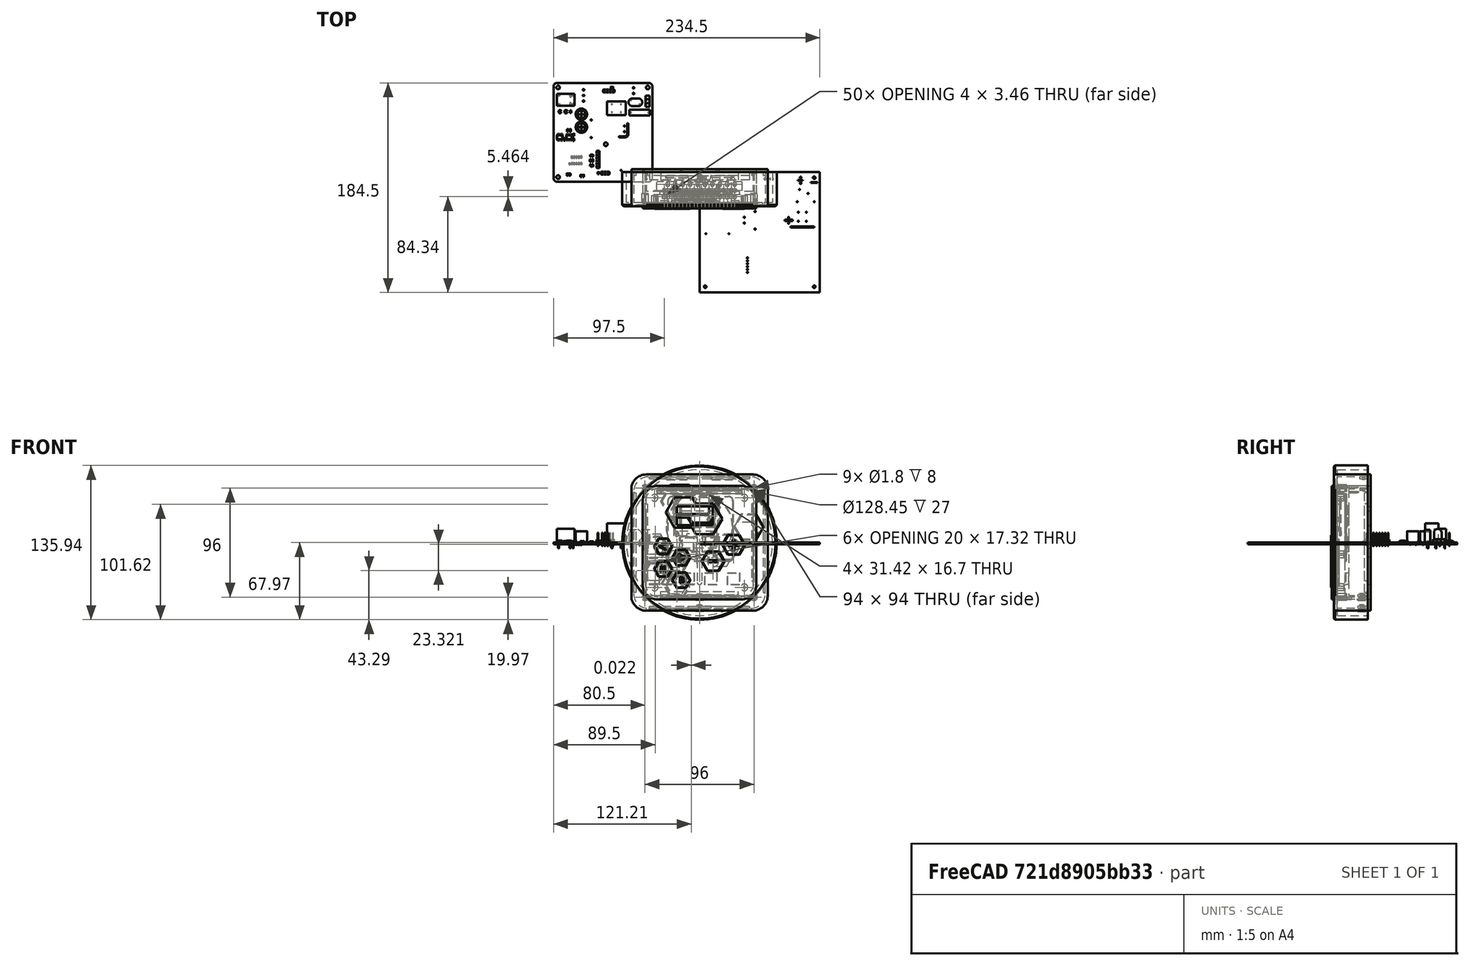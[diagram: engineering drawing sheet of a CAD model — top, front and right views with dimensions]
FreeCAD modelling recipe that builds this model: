
FCSTD DOCUMENT  (FreeCAD 0.18R4 (GitTag))
Label: esp-thermostat
License: All rights reserved
LicenseURL: http://en.wikipedia.org/wiki/All_rights_reserved
objects: Sketcher::SketchObject×72, Part::Feature×48, PartDesign::Pad×45, PartDesign::Pocket×31, PartDesign::Body×14, App::Part×13, PartDesign::Chamfer×12, Mesh::Feature×8, PartDesign::Fillet×6, Part::Part2DObjectPython×6, PartDesign::CoordinateSystem×2, PartDesign::LinearPattern×2, PartDesign::Plane×1
note: 315 computed .brp shape members not serialized (recipe doc carries the construction recipe); baked Part::Feature solids carry a one-line shape summary decoded from their .brp

FEATURE [Sketcher::SketchObject] Sketch  label="Face Sketch"
  MapMode = 5
  Placement = pos=(0,0,0) rot=(1,0,0;1.5708rad)
  Support = -> [XZ_Plane]
  expr: Constraints[21] = 31.42 / 2
  sketch-geometry (48):
    g0: LineSegment StartX=-50 StartY=50 StartZ=0 EndX=50 EndY=50 EndZ=0
    g1: LineSegment StartX=50 StartY=50 StartZ=0 EndX=50 EndY=-50 EndZ=0
    g2: LineSegment StartX=50 StartY=-50 StartZ=0 EndX=-50 EndY=-50 EndZ=0
    g3: LineSegment StartX=-50 StartY=-50 StartZ=0 EndX=-50 EndY=50 EndZ=0
    g4: LineSegment StartX=-15.71 StartY=15 StartZ=0 EndX=15.71 EndY=15 EndZ=0
    g5: LineSegment StartX=15.71 StartY=15 StartZ=0 EndX=15.71 EndY=31.7 EndZ=0
    g6: LineSegment StartX=15.71 StartY=31.7 StartZ=0 EndX=-15.71 EndY=31.7 EndZ=0
    g7: LineSegment StartX=-15.71 StartY=31.7 StartZ=0 EndX=-15.71 EndY=15 EndZ=0
    g8: LineSegment StartX=-16.71 StartY=5 StartZ=0 EndX=-2.71 EndY=5 EndZ=0
    g9: LineSegment StartX=-2.71 StartY=5 StartZ=0 EndX=-2.71 EndY=-8 EndZ=0
    g10: LineSegment StartX=2.71 StartY=5 StartZ=0 EndX=16.71 EndY=5 EndZ=0
    g11: LineSegment StartX=16.71 StartY=5 StartZ=0 EndX=16.71 EndY=2.5 EndZ=0
    g12: LineSegment StartX=4.71 StartY=-8 StartZ=0 EndX=2.71 EndY=-8 EndZ=0
    g13: LineSegment StartX=2.71 StartY=-8 StartZ=0 EndX=2.71 EndY=5 EndZ=0
    g14: LineSegment StartX=-35 StartY=-27 StartZ=0 EndX=-25 EndY=-27 EndZ=0
    g15: LineSegment StartX=-25 StartY=-27 StartZ=0 EndX=-25 EndY=-37 EndZ=0
    g16: LineSegment StartX=-25 StartY=-37 StartZ=0 EndX=-35 EndY=-37 EndZ=0
    g17: LineSegment StartX=-35 StartY=-37 StartZ=0 EndX=-35 EndY=-27 EndZ=0
    g18: LineSegment StartX=-15 StartY=-27 StartZ=0 EndX=-5 EndY=-27 EndZ=0
    g19: LineSegment StartX=-5 StartY=-27 StartZ=0 EndX=-5 EndY=-37 EndZ=0
    g20: LineSegment StartX=-5 StartY=-37 StartZ=0 EndX=-15 EndY=-37 EndZ=0
    g21: LineSegment StartX=-15 StartY=-37 StartZ=0 EndX=-15 EndY=-27 EndZ=0
    g22: LineSegment StartX=5 StartY=-27 StartZ=0 EndX=15 EndY=-27 EndZ=0
    g23: LineSegment StartX=15 StartY=-27 StartZ=0 EndX=15 EndY=-37 EndZ=0
    g24: LineSegment StartX=15 StartY=-37 StartZ=0 EndX=5 EndY=-37 EndZ=0
    g25: LineSegment StartX=5 StartY=-37 StartZ=0 EndX=5 EndY=-27 EndZ=0
    g26: LineSegment StartX=25 StartY=-27 StartZ=0 EndX=35 EndY=-27 EndZ=0
    g27: LineSegment StartX=35 StartY=-27 StartZ=0 EndX=35 EndY=-37 EndZ=0
    g28: LineSegment StartX=35 StartY=-37 StartZ=0 EndX=25 EndY=-37 EndZ=0
    g29: LineSegment StartX=25 StartY=-37 StartZ=0 EndX=25 EndY=-27 EndZ=0
    g30: LineSegment [constr] StartX=-18 StartY=39.7 StartZ=0 EndX=18 EndY=39.7 EndZ=0
    g31: LineSegment [constr] StartX=18 StartY=39.7 StartZ=0 EndX=18 EndY=6 EndZ=0
    g32: LineSegment [constr] StartX=18 StartY=6 StartZ=0 EndX=-18 EndY=6 EndZ=0
    g33: LineSegment [constr] StartX=-18 StartY=6 StartZ=0 EndX=-18 EndY=39.7 EndZ=0
    g34: LineSegment StartX=-16.71 StartY=5 StartZ=0 EndX=-16.71 EndY=2.5 EndZ=0
    g35: LineSegment StartX=-2.71 StartY=-8 StartZ=0 EndX=-4.71 EndY=-8 EndZ=0
    g36: Circle [constr] CenterX=-16.71 CenterY=2.5 CenterZ=0 NormalX=0 NormalY=0 NormalZ=1 AngleXU=0 Radius=1
    g37: Circle [constr] CenterX=-14.99 CenterY=-4.5 CenterZ=0 NormalX=0 NormalY=0 NormalZ=1 AngleXU=0 Radius=1
    g38: Circle [constr] CenterX=-4.71 CenterY=-8 CenterZ=0 NormalX=0 NormalY=0 NormalZ=1 AngleXU=0 Radius=1
    g39: BSplineCurve PolesCount=3 KnotsCount=2 Degree=2 IsPeriodic=0
    g40: GeomPoint [constr] X=-16.71 Y=2.5 Z=0
    g41: GeomPoint [constr] X=-4.71 Y=-8 Z=0
    g42: Circle [constr] CenterX=4.71 CenterY=-8 CenterZ=0 NormalX=0 NormalY=0 NormalZ=1 AngleXU=0 Radius=2
    g43: Circle [constr] CenterX=14.99 CenterY=-4.5 CenterZ=0 NormalX=0 NormalY=0 NormalZ=1 AngleXU=0 Radius=2
    g44: Circle [constr] CenterX=16.71 CenterY=2.5 CenterZ=0 NormalX=0 NormalY=0 NormalZ=1 AngleXU=0 Radius=2
    g45: BSplineCurve PolesCount=3 KnotsCount=2 Degree=2 IsPeriodic=0
    g46: GeomPoint [constr] X=4.71 Y=-8 Z=0
    g47: GeomPoint [constr] X=16.71 Y=2.5 Z=0
  constraints (133):
    c: Coincident(g0,g1)
    c: Coincident(g1,g2)
    c: Coincident(g2,g3)
    c: Coincident(g3,g0)
    c: Horizontal(g0)
    c: Horizontal(g2)
    c: Vertical(g1)
    c: Vertical(g3)
    c: Equal(g0,g1)
    c: Symmetric(g0,g1,g-1)
    c: DistanceX(g0,g0) = 100
    c: Coincident(g4,g5)
    c: Coincident(g5,g6)
    c: Coincident(g6,g7)
    c: Coincident(g7,g4)
    c: Horizontal(g4)
    c: Horizontal(g6)
    c: Vertical(g5)
    c: Vertical(g7)
    c: DistanceX(g6,g6) = 31.42
    c: DistanceY(g7,g7) = 16.7
    c: DistanceX(g6,g-1) = 15.71
    c: Coincident(g8,g9)
    c: Horizontal(g8)
    c: Vertical(g9)
    c: Coincident(g10,g11)
    c: Coincident(g12,g13)
    c: Coincident(g13,g10)
    c: Horizontal(g10)
    c: Horizontal(g12)
    c: Vertical(g11)
    c: DistanceX(g8,g8) = 14
    c: Coincident(g14,g15)
    c: Coincident(g15,g16)
    c: Coincident(g16,g17)
    c: Coincident(g17,g14)
    c: Horizontal(g14)
    c: Horizontal(g16)
    c: Vertical(g15)
    c: Vertical(g17)
    c: Coincident(g18,g19)
    c: Coincident(g19,g20)
    c: Coincident(g20,g21)
    c: Coincident(g21,g18)
    c: Horizontal(g18)
    c: Horizontal(g20)
    c: Vertical(g19)
    c: Vertical(g21)
    c: Coincident(g22,g23)
    c: Coincident(g23,g24)
    c: Coincident(g24,g25)
    c: Coincident(g25,g22)
    c: Horizontal(g22)
    c: Horizontal(g24)
    c: Vertical(g23)
    c: Vertical(g25)
    c: Coincident(g26,g27)
    c: Coincident(g27,g28)
    c: Coincident(g28,g29)
    c: Coincident(g29,g26)
    c: Horizontal(g26)
    c: Horizontal(g28)
    c: Vertical(g27)
    c: Vertical(g29)
    c: Equal(g14,g15)
    c: Equal(g15,g18)
    c: Equal(g18,g19)
    c: Equal(g19,g22)
    c: Equal(g22,g23)
    c: Equal(g23,g26)
    c: Equal(g26,g27)
    c: DistanceY(g-1,g9) = -8
    c: DistanceY(g-1,g12) = -8
    c: DistanceY(g14,g18) = 0
    c: DistanceY(g22,g18) = 0
    c: DistanceY(g22,g26) = 0
    c: DistanceX(g14,g18) = 10
    c: DistanceX(g18,g22) = 10
    c: DistanceX(g22,g26) = 10
    c: DistanceX(g18,g-1) = 5
    c: DistanceY(g22,g-1) = 27
    c: DistanceY(g-1,g4) = 15
    c: Coincident(g30,g31)
    c: Coincident(g31,g32)
    c: Coincident(g32,g33)
    c: Coincident(g33,g30)
    c: Horizontal(g30)
    c: Horizontal(g32)
    c: Vertical(g31)
    c: Vertical(g33)
    c: DistanceX(g30,g30) = 36
    c: DistanceX(g30,g6) = 2.29
    c: DistanceY(g6,g30) = 8
    c: DistanceX(g14,g14) = 10
    c: DistanceY(g9,g8) = 13
    c: Equal(g8,g10)
    c: Equal(g9,g13)
    c: Coincident(g34,g8)
    c: Vertical(g34)
    c: Coincident(g35,g9)
    c: Horizontal(g35)
    c: Equal(g34,g11)
    c: Equal(g35,g12)
    c: DistanceX(g8,g4) = 1
    c: DistanceX(g4,g10) = 1
    c: DistanceY(g31,g31) = 33.7
    c: Coincident(g39,g34)
    c: Radius(g36) = 1
    c: Equal(g36,g37)
    c: Equal(g36,g38)
    c: Coincident(g39,g35)
    c: InternalAlignment(g36,g39)
    c: InternalAlignment(g37,g39)
    c: InternalAlignment(g38,g39)
    c: InternalAlignment(g40,g39)
    c: InternalAlignment(g41,g39)
    c: DistanceX(g34,g37) = 1.72
    c: DistanceY(g35,g37) = 3.5
    c: DistanceY(g34,g34) = 2.5
    c: DistanceX(g35,g35) = 2
    c: Parallel(g13,g9)
    c: Coincident(g45,g12)
    c: Radius(g42) = 2
    c: Equal(g42,g43)
    c: Equal(g42,g44)
    c: Coincident(g45,g11)
    c: InternalAlignment(g42,g45)
    c: InternalAlignment(g43,g45)
    c: InternalAlignment(g44,g45)
    c: InternalAlignment(g46,g45)
    c: InternalAlignment(g47,g45)
    c: DistanceX(g43,g11) = 1.72
    c: DistanceY(g12,g43) = 3.5
FEATURE [PartDesign::Pad] Pad  label="Body Pad"
  Length = 20
  Length2 = 100
  Placement = pos=(0,0,0) rot=(1,0,0;1.5708rad)
  Profile = -> Sketch
  Type = 0
FEATURE [Sketcher::SketchObject] Sketch002  label="Inside Sketch"
  MapMode = 5
  Placement = pos=(0,0,0) rot=(-1,0,0;1.5708rad)
  sketch-geometry (4):
    g0: LineSegment StartX=-47 StartY=47 StartZ=0 EndX=47 EndY=47 EndZ=0
    g1: LineSegment StartX=47 StartY=47 StartZ=0 EndX=47 EndY=-47 EndZ=0
    g2: LineSegment StartX=47 StartY=-47 StartZ=0 EndX=-47 EndY=-47 EndZ=0
    g3: LineSegment StartX=-47 StartY=-47 StartZ=0 EndX=-47 EndY=47 EndZ=0
  constraints (9):
    c: Coincident(g0,g1)
    c: Coincident(g1,g2)
    c: Coincident(g2,g3)
    c: Coincident(g3,g0)
    c: Horizontal(g0)
    c: Horizontal(g2)
    c: Vertical(g1)
    c: Vertical(g3)
    c: Symmetric(g0,g1,g-1)
FEATURE [PartDesign::Pocket] Pocket001  label="Inside Pocket"
  BaseFeature = -> Pad
  Length = 5
  Length2 = 100
  Offset = -3
  Placement = pos=(0,0,0) rot=(1,0,0;1.5708rad)
  Profile = -> Sketch002
  Type = 2
FEATURE [Sketcher::SketchObject] Sketch008  label="Face Circle Sketch"
  MapMode = 5
  Placement = pos=(0,-20,0) rot=(1,0,0;1.5708rad)
  Support = -> [Pocket001]
  sketch-geometry (1):
    g0: Circle CenterX=0 CenterY=14 CenterZ=0 NormalX=0 NormalY=0 NormalZ=1 AngleXU=0 Radius=29
  constraints (3):
    c: PointOnObject(g0,g-2)
    c: Radius(g0) = 29
    c: DistanceY(g-1,g0) = 14
FEATURE [PartDesign::Pocket] Pocket  label="Face Circle Pocket"
  BaseFeature = -> Pocket001
  Length = 1
  Length2 = 100
  Placement = pos=(0,0,0) rot=(1,0,0;1.5708rad)
  Profile = -> Sketch008
  Type = 0
FEATURE [PartDesign::Fillet] Fillet  label="Edge Fillet"
  Base = -> Pocket [Face6,Face3,Face1,Face2]
  BaseFeature = -> Pocket
  Placement = pos=(0,0,0) rot=(1,0,0;1.5708rad)
  Radius = 2.6
FEATURE [PartDesign::Chamfer] Chamfer  label="Minus Button Chamfer"
  Base = -> Fillet [Edge136,Edge135,Edge134,Edge138,Edge137]
  BaseFeature = -> Fillet
  Placement = pos=(0,0,0) rot=(1,0,0;1.5708rad)
  Size = 0.5
FEATURE [PartDesign::Chamfer] Chamfer001  label="Plus Button Chamfer"
  Base = -> Chamfer [Edge8,Edge7,Edge11,Edge10,Edge9]
  BaseFeature = -> Chamfer
  Placement = pos=(0,0,0) rot=(1,0,0;1.5708rad)
  Size = 0.5
FEATURE [PartDesign::Chamfer] Chamfer002  label="Display Chamfer"
  Base = -> Chamfer001 [Edge12,Edge15,Edge14,Edge13]
  BaseFeature = -> Chamfer001
  Placement = pos=(0,0,0) rot=(1,0,0;1.5708rad)
  Size = 1.5
FEATURE [PartDesign::Chamfer] Chamfer003  label="Circle Chamfer"
  Base = -> Chamfer002 [Edge45]
  BaseFeature = -> Chamfer002
  Placement = pos=(0,0,0) rot=(1,0,0;1.5708rad)
  Size = 0.4
FEATURE [PartDesign::Chamfer] Chamfer004  label="Auxiliary Buttons Chamfer"
  Base = -> Chamfer003 [Edge37,Edge36,Edge38,Edge39,Edge28,Edge29,Edge31,Edge30,Edge26,Edge24,Edge25,Edge27,Edge34,Edge32,Edge33,Edge35]
  BaseFeature = -> Chamfer003
  Placement = pos=(0,0,0) rot=(1,0,0;1.5708rad)
  Size = 0.5
FEATURE [PartDesign::Body] Body  label="Housing"
  Group = -> [Sketch,Pad,Sketch002,Pocket001,Pocket,Sketch008,Fillet,Chamfer,Chamfer001,Chamfer002,Chamfer003,Chamfer004]
  Origin = -> Origin
  Tip = -> Chamfer004
FEATURE [Sketcher::SketchObject] Sketch010  label="Face Sketch001"
  MapMode = 5
  Placement = pos=(0,0,0) rot=(1,0,0;1.5708rad)
  Support = -> [XZ_Plane001]
  expr: Constraints[21] = 31.42 / 2
  sketch-geometry (40):
    g0: LineSegment StartX=-50 StartY=50 StartZ=0 EndX=50 EndY=50 EndZ=0
    g1: LineSegment StartX=50 StartY=50 StartZ=0 EndX=50 EndY=-50 EndZ=0
    g2: LineSegment StartX=50 StartY=-50 StartZ=0 EndX=-50 EndY=-50 EndZ=0
    g3: LineSegment StartX=-50 StartY=-50 StartZ=0 EndX=-50 EndY=50 EndZ=0
    g4: LineSegment StartX=-15.71 StartY=15 StartZ=0 EndX=15.71 EndY=15 EndZ=0
    g5: LineSegment StartX=15.71 StartY=15 StartZ=0 EndX=15.71 EndY=31.7 EndZ=0
    g6: LineSegment StartX=15.71 StartY=31.7 StartZ=0 EndX=-15.71 EndY=31.7 EndZ=0
    g7: LineSegment StartX=-15.71 StartY=31.7 StartZ=0 EndX=-15.71 EndY=15 EndZ=0
    g8: LineSegment StartX=-17.21 StartY=4 StartZ=0 EndX=-5.21 EndY=4 EndZ=0
    g9: LineSegment StartX=-5.21 StartY=4 StartZ=0 EndX=-5.21 EndY=-8 EndZ=0
    g10: LineSegment StartX=5.21 StartY=4 StartZ=0 EndX=17.21 EndY=4 EndZ=0
    g11: LineSegment StartX=17.21 StartY=4 StartZ=0 EndX=17.21 EndY=1.5 EndZ=0
    g12: LineSegment StartX=7.21 StartY=-8 StartZ=0 EndX=5.21 EndY=-8 EndZ=0
    g13: LineSegment StartX=5.21 StartY=-8 StartZ=0 EndX=5.21 EndY=4 EndZ=0
    g14: LineSegment StartX=-35 StartY=-27 StartZ=0 EndX=-25 EndY=-27 EndZ=0
    g15: LineSegment StartX=-25 StartY=-27 StartZ=0 EndX=-25 EndY=-37 EndZ=0
    g16: LineSegment StartX=-25 StartY=-37 StartZ=0 EndX=-35 EndY=-37 EndZ=0
    g17: LineSegment StartX=-35 StartY=-37 StartZ=0 EndX=-35 EndY=-27 EndZ=0
    g18: LineSegment StartX=-15 StartY=-27 StartZ=0 EndX=-5 EndY=-27 EndZ=0
    g19: LineSegment StartX=-5 StartY=-27 StartZ=0 EndX=-5 EndY=-37 EndZ=0
    g20: LineSegment StartX=-5 StartY=-37 StartZ=0 EndX=-15 EndY=-37 EndZ=0
    g21: LineSegment StartX=-15 StartY=-37 StartZ=0 EndX=-15 EndY=-27 EndZ=0
    g22: LineSegment StartX=5 StartY=-27 StartZ=0 EndX=15 EndY=-27 EndZ=0
    g23: LineSegment StartX=15 StartY=-27 StartZ=0 EndX=15 EndY=-37 EndZ=0
    g24: LineSegment StartX=15 StartY=-37 StartZ=0 EndX=5 EndY=-37 EndZ=0
    g25: LineSegment StartX=5 StartY=-37 StartZ=0 EndX=5 EndY=-27 EndZ=0
    g26: LineSegment StartX=25 StartY=-27 StartZ=0 EndX=35 EndY=-27 EndZ=0
    g27: LineSegment StartX=35 StartY=-27 StartZ=0 EndX=35 EndY=-37 EndZ=0
    g28: LineSegment StartX=35 StartY=-37 StartZ=0 EndX=25 EndY=-37 EndZ=0
    g29: LineSegment StartX=25 StartY=-37 StartZ=0 EndX=25 EndY=-27 EndZ=0
    g30: LineSegment [constr] StartX=-18 StartY=39.7 StartZ=0 EndX=18 EndY=39.7 EndZ=0
    g31: LineSegment [constr] StartX=18 StartY=39.7 StartZ=0 EndX=18 EndY=6 EndZ=0
    g32: LineSegment [constr] StartX=18 StartY=6 StartZ=0 EndX=-18 EndY=6 EndZ=0
    g33: LineSegment [constr] StartX=-18 StartY=6 StartZ=0 EndX=-18 EndY=39.7 EndZ=0
    g34: LineSegment StartX=-17.21 StartY=4 StartZ=0 EndX=-17.21 EndY=1.5 EndZ=0
    g35: LineSegment StartX=-5.21 StartY=-8 StartZ=0 EndX=-7.21 EndY=-8 EndZ=0
    g36: LineSegment StartX=-7.21 StartY=-8 StartZ=0 EndX=-17.21 EndY=-8 EndZ=0
    g37: LineSegment StartX=-17.21 StartY=1.5 StartZ=0 EndX=-17.21 EndY=-8 EndZ=0
    g38: LineSegment StartX=7.21 StartY=-8 StartZ=0 EndX=17.21 EndY=-8 EndZ=0
    g39: LineSegment StartX=17.21 StartY=1.5 StartZ=0 EndX=17.21 EndY=-8 EndZ=0
  constraints (119):
    c: Coincident(g0,g1)
    c: Coincident(g1,g2)
    c: Coincident(g2,g3)
    c: Coincident(g3,g0)
    c: Horizontal(g0)
    c: Horizontal(g2)
    c: Vertical(g1)
    c: Vertical(g3)
    c: Equal(g0,g1)
    c: Symmetric(g0,g1,g-1)
    c: DistanceX(g0,g0) = 100
    c: Coincident(g4,g5)
    c: Coincident(g5,g6)
    c: Coincident(g6,g7)
    c: Coincident(g7,g4)
    c: Horizontal(g4)
    c: Horizontal(g6)
    c: Vertical(g5)
    c: Vertical(g7)
    c: DistanceX(g6,g6) = 31.42
    c: DistanceY(g7,g7) = 16.7
    c: DistanceX(g6,g-1) = 15.71
    c: Coincident(g8,g9)
    c: Horizontal(g8)
    c: Vertical(g9)
    c: Coincident(g10,g11)
    c: Coincident(g12,g13)
    c: Coincident(g13,g10)
    c: Horizontal(g10)
    c: Horizontal(g12)
    c: Vertical(g11)
    c: DistanceX(g8,g8) = 12
    c: Coincident(g14,g15)
    c: Coincident(g15,g16)
    c: Coincident(g16,g17)
    c: Coincident(g17,g14)
    c: Horizontal(g14)
    c: Horizontal(g16)
    c: Vertical(g15)
    c: Vertical(g17)
    c: Coincident(g18,g19)
    c: Coincident(g19,g20)
    c: Coincident(g20,g21)
    c: Coincident(g21,g18)
    c: Horizontal(g18)
    c: Horizontal(g20)
    c: Vertical(g19)
    c: Vertical(g21)
    c: Coincident(g22,g23)
    c: Coincident(g23,g24)
    c: Coincident(g24,g25)
    c: Coincident(g25,g22)
    c: Horizontal(g22)
    c: Horizontal(g24)
    c: Vertical(g23)
    c: Vertical(g25)
    c: Coincident(g26,g27)
    c: Coincident(g27,g28)
    c: Coincident(g28,g29)
    c: Coincident(g29,g26)
    c: Horizontal(g26)
    c: Horizontal(g28)
    c: Vertical(g27)
    c: Vertical(g29)
    c: Equal(g14,g15)
    c: Equal(g15,g18)
    c: Equal(g18,g19)
    c: Equal(g19,g22)
    c: Equal(g22,g23)
    c: Equal(g23,g26)
    c: Equal(g26,g27)
    c: DistanceY(g-1,g9) = -8
    c: DistanceY(g-1,g12) = -8
    c: DistanceY(g14,g18) = 0
    c: DistanceY(g22,g18) = 0
    c: DistanceY(g22,g26) = 0
    c: DistanceX(g14,g18) = 10
    c: DistanceX(g18,g22) = 10
    c: DistanceX(g22,g26) = 10
    c: DistanceX(g18,g-1) = 5
    c: DistanceY(g22,g-1) = 27
    c: DistanceY(g-1,g4) = 15
    c: Coincident(g30,g31)
    c: Coincident(g31,g32)
    c: Coincident(g32,g33)
    c: Coincident(g33,g30)
    c: Horizontal(g30)
    c: Horizontal(g32)
    c: Vertical(g31)
    c: Vertical(g33)
    c: DistanceX(g30,g30) = 36
    c: DistanceX(g30,g6) = 2.29
    c: DistanceY(g6,g30) = 8
    c: DistanceX(g14,g14) = 10
    c: DistanceY(g9,g8) = 12
    c: Equal(g8,g10)
    c: Equal(g9,g13)
    c: Coincident(g34,g8)
    c: Vertical(g34)
    c: Coincident(g35,g9)
    c: Horizontal(g35)
    c: Equal(g34,g11)
    c: Equal(g35,g12)
    c: DistanceX(g8,g4) = 1.5
    c: DistanceX(g4,g10) = 1.5
    c: DistanceY(g31,g31) = 33.7
    c: DistanceY(g34,g34) = 2.5
    c: DistanceX(g35,g35) = 2
    c: Parallel(g13,g9)
    c: Coincident(g36,g35)
    c: Horizontal(g36)
    c: Coincident(g37,g34)
    c: Vertical(g37)
    c: Coincident(g36,g37)
    c: Coincident(g38,g12)
    c: Horizontal(g38)
    c: Coincident(g39,g11)
    c: Vertical(g39)
    c: Coincident(g38,g39)
FEATURE [Sketcher::SketchObject] Sketch011  label="Inside Sketch001"
  MapMode = 5
  Placement = pos=(0,0,0) rot=(-1,0,0;1.5708rad)
  sketch-geometry (4):
    g0: LineSegment StartX=-47 StartY=47 StartZ=0 EndX=47 EndY=47 EndZ=0
    g1: LineSegment StartX=47 StartY=47 StartZ=0 EndX=47 EndY=-47 EndZ=0
    g2: LineSegment StartX=47 StartY=-47 StartZ=0 EndX=-47 EndY=-47 EndZ=0
    g3: LineSegment StartX=-47 StartY=-47 StartZ=0 EndX=-47 EndY=47 EndZ=0
  constraints (9):
    c: Coincident(g0,g1)
    c: Coincident(g1,g2)
    c: Coincident(g2,g3)
    c: Coincident(g3,g0)
    c: Horizontal(g0)
    c: Horizontal(g2)
    c: Vertical(g1)
    c: Vertical(g3)
    c: Symmetric(g0,g1,g-1)
FEATURE [PartDesign::Pad] Pad001  label="Body Pad001"
  Length = 20
  Length2 = 100
  Placement = pos=(0,0,0) rot=(1,0,0;1.5708rad)
  Profile = -> Sketch010
  Type = 0
FEATURE [PartDesign::Pocket] Pocket003  label="Inside Pocket001"
  BaseFeature = -> Pad001
  Length = 5
  Length2 = 100
  Offset = -3
  Placement = pos=(0,0,0) rot=(1,0,0;1.5708rad)
  Profile = -> Sketch011
  Type = 2
FEATURE [Sketcher::SketchObject] Sketch009  label="Face Circle Sketch001"
  MapMode = 5
  Placement = pos=(0,-20,0) rot=(1,0,0;1.5708rad)
  Support = -> [Pocket003]
  expr: Constraints[16] = 55 / 2
  sketch-geometry (8):
    g0: LineSegment StartX=-23.9253 StartY=40.3727 StartZ=0 EndX=25.6028 EndY=40.3727 EndZ=0
    g1: LineSegment StartX=29.1774 StartY=36.798 StartZ=0 EndX=29.1774 EndY=-12.7301 EndZ=0
    g2: LineSegment StartX=25.6028 StartY=-16.3047 StartZ=0 EndX=-23.9253 EndY=-16.3047 EndZ=0
    g3: LineSegment StartX=-27.5 StartY=-12.7301 StartZ=0 EndX=-27.5 EndY=36.798 EndZ=0
    g4: ArcOfCircle CenterX=-23.9253 CenterY=36.798 CenterZ=0 NormalX=0 NormalY=0 NormalZ=1 AngleXU=0 Radius=3.57466 StartAngle=1.5708 EndAngle=3.14159
    g5: ArcOfCircle CenterX=25.6028 CenterY=36.798 CenterZ=0 NormalX=0 NormalY=0 NormalZ=1 AngleXU=0 Radius=3.57466 StartAngle=8e-16 EndAngle=1.5708
    g6: ArcOfCircle CenterX=25.6028 CenterY=-12.7301 CenterZ=0 NormalX=0 NormalY=0 NormalZ=1 AngleXU=0 Radius=3.57466 StartAngle=4.71239 EndAngle=6.28319
    g7: ArcOfCircle CenterX=-23.9253 CenterY=-12.7301 CenterZ=0 NormalX=0 NormalY=0 NormalZ=1 AngleXU=0 Radius=3.57466 StartAngle=3.14159 EndAngle=4.71239
  constraints (17):
    c: Horizontal(g0)
    c: Horizontal(g2)
    c: Vertical(g1)
    c: Vertical(g3)
    c: Equal(g0,g1)
    c: Tangent(g3,g4) = 1.5708
    c: Tangent(g0,g4) = 1.5708
    c: Tangent(g0,g5) = 1.5708
    c: Tangent(g1,g5) = 1.5708
    c: Tangent(g2,g6) = 1.5708
    c: Tangent(g1,g6) = 1.5708
    c: Tangent(g2,g7) = 1.5708
    c: Tangent(g3,g7) = 1.5708
    c: Equal(g7,g4)
    c: Equal(g4,g5)
    c: Equal(g5,g6)
    c: DistanceX(g3,g-1) = 27.5
FEATURE [PartDesign::Pocket] Pocket002  label="Face Circle Pocket001"
  BaseFeature = -> Pocket003
  Length = 1
  Length2 = 100
  Placement = pos=(0,0,0) rot=(1,0,0;1.5708rad)
  Profile = -> Sketch009
  Type = 0
FEATURE [PartDesign::Fillet] Fillet001  label="Edge Fillet001"
  Base = -> Pocket002 [Face6,Face3,Face1,Face2]
  BaseFeature = -> Pocket002
  Placement = pos=(0,0,0) rot=(1,0,0;1.5708rad)
  Radius = 2.6
FEATURE [PartDesign::Chamfer] Chamfer009  label="Display Chamfer001"
  Base = -> Fillet001 [Edge170,Edge171,Edge172,Edge169]
  BaseFeature = -> Fillet001
  Placement = pos=(0,0,0) rot=(1,0,0;1.5708rad)
  Size = 1.5
FEATURE [PartDesign::Chamfer] Chamfer007  label="Circle Chamfer001"
  Base = -> Chamfer009 [Edge35]
  BaseFeature = -> Chamfer009
  Placement = pos=(0,0,0) rot=(1,0,0;1.5708rad)
  Size = 0.4
FEATURE [PartDesign::Chamfer] Chamfer006  label="Auxiliary Buttons Chamfer001"
  Base = -> Chamfer007 [Edge63,Edge61,Edge62,Edge64,Edge53,Edge55,Edge56,Edge54,Edge51,Edge49,Edge50,Edge59,Edge57,Edge58,Edge60,Edge21,Edge23,Edge24,Edge26,Edge30,Edge29,Edge27,Edge32]
  BaseFeature = -> Chamfer007
  Placement = pos=(0,0,0) rot=(1,0,0;1.5708rad)
  Size = 0.5
FEATURE [PartDesign::Body] Body001  label="Housing - Rectangular Face"
  Group = -> [Sketch010,Pad001,Sketch011,Pocket003,Pocket002,Sketch009,Fillet001,Chamfer009,Chamfer007,Chamfer006]
  Origin = -> Origin001
  Tip = -> Chamfer006
FEATURE [Sketcher::SketchObject] Sketch012
  MapMode = 5
  Placement = pos=(0,0,0) rot=(1,0,0;1.5708rad)
  Support = -> [XZ_Plane002]
  sketch-geometry (47):
    g0: LineSegment StartX=-33.6497 StartY=-12.7937 StartZ=0 EndX=-28.6497 EndY=-4.1334 EndZ=0
    g1: LineSegment StartX=-28.6497 StartY=-4.1334 StartZ=0 EndX=-33.6497 EndY=4.52685 EndZ=0
    g2: LineSegment StartX=-33.6497 StartY=4.52685 StartZ=0 EndX=-43.6497 EndY=4.52685 EndZ=0
    g3: LineSegment StartX=-43.6497 StartY=4.52685 StartZ=0 EndX=-48.6497 EndY=-4.1334 EndZ=0
    g4: LineSegment StartX=-48.6497 StartY=-4.1334 StartZ=0 EndX=-43.6497 EndY=-12.7937 EndZ=0
    g5: LineSegment StartX=-43.6497 StartY=-12.7937 StartZ=0 EndX=-33.6497 EndY=-12.7937 EndZ=0
    g6: Circle [constr] CenterX=-38.6497 CenterY=-4.1334 CenterZ=0 NormalX=0 NormalY=0 NormalZ=1 AngleXU=0 Radius=10
    g7: LineSegment StartX=-14.6497 StartY=-24.4539 StartZ=0 EndX=-9.64969 EndY=-15.7937 EndZ=0
    g8: LineSegment StartX=-9.64969 StartY=-15.7937 StartZ=0 EndX=-14.6497 EndY=-7.1334 EndZ=0
    g9: LineSegment StartX=-14.6497 StartY=-7.1334 StartZ=0 EndX=-24.6497 EndY=-7.1334 EndZ=0
    g10: LineSegment StartX=-24.6497 StartY=-7.1334 StartZ=0 EndX=-29.6497 EndY=-15.7937 EndZ=0
    g11: LineSegment StartX=-29.6497 StartY=-15.7937 StartZ=0 EndX=-24.6497 EndY=-24.4539 EndZ=0
    g12: LineSegment StartX=-24.6497 StartY=-24.4539 StartZ=0 EndX=-14.6497 EndY=-24.4539 EndZ=0
    g13: Circle [constr] CenterX=-19.6497 CenterY=-15.7937 CenterZ=0 NormalX=0 NormalY=0 NormalZ=1 AngleXU=0 Radius=10
    g14: LineSegment StartX=-28.6497 StartY=-27.4539 StartZ=0 EndX=-33.6497 EndY=-18.7937 EndZ=0
    g15: LineSegment StartX=-33.6497 StartY=-18.7937 StartZ=0 EndX=-43.6497 EndY=-18.7937 EndZ=0
    g16: LineSegment StartX=-43.6497 StartY=-18.7937 StartZ=0 EndX=-48.6497 EndY=-27.4539 EndZ=0
    g17: LineSegment StartX=-48.6497 StartY=-27.4539 StartZ=0 EndX=-43.6497 EndY=-36.1142 EndZ=0
    g18: LineSegment StartX=-43.6497 StartY=-36.1142 StartZ=0 EndX=-33.6497 EndY=-36.1142 EndZ=0
    g19: LineSegment StartX=-33.6497 StartY=-36.1142 StartZ=0 EndX=-28.6497 EndY=-27.4539 EndZ=0
    g20: Circle [constr] CenterX=-38.6497 CenterY=-27.4539 CenterZ=0 NormalX=0 NormalY=0 NormalZ=1 AngleXU=0 Radius=10
    g21: LineSegment StartX=-14.6497 StartY=-47.7744 StartZ=0 EndX=-9.64969 EndY=-39.1142 EndZ=0
    g22: LineSegment StartX=-9.64969 StartY=-39.1142 StartZ=0 EndX=-14.6497 EndY=-30.4539 EndZ=0
    g23: LineSegment StartX=-14.6497 StartY=-30.4539 StartZ=0 EndX=-24.6497 EndY=-30.4539 EndZ=0
    g24: LineSegment StartX=-24.6497 StartY=-30.4539 StartZ=0 EndX=-29.6497 EndY=-39.1142 EndZ=0
    g25: LineSegment StartX=-29.6497 StartY=-39.1142 StartZ=0 EndX=-24.6497 EndY=-47.7744 EndZ=0
    g26: LineSegment StartX=-24.6497 StartY=-47.7744 StartZ=0 EndX=-14.6497 EndY=-47.7744 EndZ=0
    g27: Circle [constr] CenterX=-19.6497 CenterY=-39.1142 CenterZ=0 NormalX=0 NormalY=0 NormalZ=1 AngleXU=0 Radius=10
    g28: LineSegment StartX=-22.9778 StartY=41.8382 StartZ=0 EndX=8.44221 EndY=41.8382 EndZ=0
    g29: LineSegment StartX=8.44221 StartY=41.8382 StartZ=0 EndX=8.44221 EndY=25.1382 EndZ=0
    g30: LineSegment StartX=8.44221 StartY=25.1382 StartZ=0 EndX=-22.9778 EndY=25.1382 EndZ=0
    g31: LineSegment StartX=-22.9778 StartY=25.1382 StartZ=0 EndX=-22.9778 EndY=41.8382 EndZ=0
    g32: LineSegment StartX=28.2444 StartY=-14.4017 StartZ=0 EndX=34.2444 EndY=-4.00938 EndZ=0
    g33: LineSegment StartX=34.2444 StartY=-4.00938 StartZ=0 EndX=28.2444 EndY=6.38293 EndZ=0
    g34: LineSegment StartX=28.2444 StartY=6.38293 StartZ=0 EndX=16.2444 EndY=6.38293 EndZ=0
    g35: LineSegment StartX=16.2444 StartY=6.38293 StartZ=0 EndX=10.2444 EndY=-4.00938 EndZ=0
    g36: LineSegment StartX=10.2444 StartY=-4.00938 StartZ=0 EndX=16.2444 EndY=-14.4017 EndZ=0
    g37: LineSegment StartX=16.2444 StartY=-14.4017 StartZ=0 EndX=28.2444 EndY=-14.4017 EndZ=0
    g38: Circle [constr] CenterX=22.2444 CenterY=-4.00938 CenterZ=0 NormalX=0 NormalY=0 NormalZ=1 AngleXU=0 Radius=12
    g39: LineSegment StartX=49.2444 StartY=3.38293 StartZ=0 EndX=55.2444 EndY=13.7752 EndZ=0
    g40: LineSegment StartX=55.2444 StartY=13.7752 StartZ=0 EndX=49.2444 EndY=24.1675 EndZ=0
    g41: LineSegment StartX=49.2444 StartY=24.1675 StartZ=0 EndX=37.2444 EndY=24.1675 EndZ=0
    g42: LineSegment StartX=37.2444 StartY=24.1675 StartZ=0 EndX=31.2444 EndY=13.7752 EndZ=0
    g43: LineSegment StartX=31.2444 StartY=13.7752 StartZ=0 EndX=37.2444 EndY=3.38293 EndZ=0
    g44: LineSegment StartX=37.2444 StartY=3.38293 StartZ=0 EndX=49.2444 EndY=3.38293 EndZ=0
    g45: Circle [constr] CenterX=43.2444 CenterY=13.7752 CenterZ=0 NormalX=0 NormalY=0 NormalZ=1 AngleXU=0 Radius=12
    g46: Circle CenterX=0 CenterY=0 CenterZ=0 NormalX=0 NormalY=0 NormalZ=1 AngleXU=0 Radius=67.967
  constraints (109):
    c: Coincident(g0,g1)
    c: Coincident(g1,g2)
    c: Coincident(g2,g3)
    c: Coincident(g3,g4)
    c: Coincident(g4,g5)
    c: Coincident(g5,g0)
    c: Equal(g0, g1-g5) x5
    c: PointOnObject(g0,g6)
    c: PointOnObject(g1,g6)
    c: PointOnObject(g2,g6)
    c: PointOnObject(g3,g6)
    c: PointOnObject(g4,g6)
    c: PointOnObject(g5,g6)
    c: Parallel(g2,g-1)
    c: Radius(g6) = 10
    c: Coincident(g7,g8)
    c: Coincident(g8,g9)
    c: Coincident(g9,g10)
    c: Coincident(g10,g11)
    c: Coincident(g11,g12)
    c: Coincident(g12,g7)
    c: Equal(g7, g8-g12) x5
    c: PointOnObject(g7,g13)
    c: PointOnObject(g8,g13)
    c: PointOnObject(g9,g13)
    c: PointOnObject(g10,g13)
    c: PointOnObject(g11,g13)
    c: PointOnObject(g12,g13)
    c: Parallel(g9,g-1)
    c: Radius(g13) = 10
    c: DistanceX(g0,g9) = 4
    c: DistanceY(g9,g0) = 3
    c: Coincident(g14,g15)
    c: Coincident(g15,g16)
    c: Coincident(g16,g17)
    c: Coincident(g17,g18)
    c: Coincident(g18,g19)
    c: Coincident(g19,g14)
    c: Equal(g14, g15-g19) x5
    c: PointOnObject(g14,g20)
    c: PointOnObject(g15,g20)
    c: PointOnObject(g16,g20)
    c: PointOnObject(g17,g20)
    c: PointOnObject(g18,g20)
    c: PointOnObject(g19,g20)
    c: Parallel(g15,g-1)
    c: Radius(g20) = 10
    c: DistanceX(g14,g10) = 4
    c: DistanceY(g14,g10) = 3
    c: Coincident(g21,g22)
    c: Coincident(g22,g23)
    c: Coincident(g23,g24)
    c: Coincident(g24,g25)
    c: Coincident(g25,g26)
    c: Coincident(g26,g21)
    c: Equal(g21, g22-g26) x5
    c: PointOnObject(g21,g27)
    c: PointOnObject(g22,g27)
    c: PointOnObject(g23,g27)
    c: PointOnObject(g24,g27)
    c: PointOnObject(g25,g27)
    c: PointOnObject(g26,g27)
    c: Parallel(g23,g-1)
    c: Radius(g27) = 10
    c: DistanceX(g14,g23) = 4
    c: DistanceY(g23,g14) = 3
    c: Coincident(g28,g29)
    c: Coincident(g29,g30)
    c: Coincident(g30,g31)
    c: Coincident(g31,g28)
    c: Horizontal(g28)
    c: Horizontal(g30)
    c: Vertical(g29)
    c: Vertical(g31)
    c: DistanceX(g28,g28) = 31.42
    c: DistanceY(g31,g31) = 16.7
    c: Coincident(g32,g33)
    c: Coincident(g33,g34)
    c: Coincident(g34,g35)
    c: Coincident(g35,g36)
    c: Coincident(g36,g37)
    c: Coincident(g37,g32)
    c: Equal(g32, g33-g37) x5
    c: PointOnObject(g32,g38)
    c: PointOnObject(g33,g38)
    c: PointOnObject(g34,g38)
    c: PointOnObject(g35,g38)
    c: PointOnObject(g36,g38)
    c: PointOnObject(g37,g38)
    c: Parallel(g34,g30)
    c: Radius(g38) = 12
    c: Coincident(g39,g40)
    c: Coincident(g40,g41)
    c: Coincident(g41,g42)
    c: Coincident(g42,g43)
    c: Coincident(g43,g44)
    c: Coincident(g44,g39)
    c: Equal(g39, g40-g44) x5
    c: PointOnObject(g39,g45)
    c: PointOnObject(g40,g45)
    c: PointOnObject(g41,g45)
    c: PointOnObject(g42,g45)
    c: PointOnObject(g43,g45)
    c: PointOnObject(g44,g45)
    c: Radius(g45) = 12
    c: Parallel(g41,g30)
    c: DistanceY(g43,g33) = 3
    c: DistanceX(g33,g42) = 3
    c: Coincident(g46,g-1)
FEATURE [PartDesign::Pad] Pad002
  Length = 30
  Length2 = 100
  Placement = pos=(0,0,0) rot=(1,0,0;1.5708rad)
  Profile = -> Sketch012
  Type = 0
FEATURE [Sketcher::SketchObject] Sketch014
  MapMode = 5
  Placement = pos=(0,-30,3.3e-14) rot=(1,0,0;1.5708rad)
  sketch-geometry (26):
    g0: LineSegment [constr] StartX=-9.58917 StartY=23.011 StartZ=0 EndX=-1.82084 EndY=36.4661 EndZ=0
    g1: LineSegment [constr] StartX=-1.82084 StartY=36.4661 StartZ=0 EndX=-9.58917 EndY=49.9213 EndZ=0
    g2: LineSegment [constr] StartX=-9.58917 StartY=49.9213 StartZ=0 EndX=-25.1258 EndY=49.9213 EndZ=0
    g3: LineSegment [constr] StartX=-25.1258 StartY=49.9213 StartZ=0 EndX=-32.8942 EndY=36.4661 EndZ=0
    g4: LineSegment [constr] StartX=-32.8942 StartY=36.4661 StartZ=0 EndX=-25.1258 EndY=23.011 EndZ=0
    g5: LineSegment [constr] StartX=-25.1258 StartY=23.011 StartZ=0 EndX=-9.58917 EndY=23.011 EndZ=0
    g6: Circle [constr] CenterX=-17.3575 CenterY=36.4661 CenterZ=0 NormalX=0 NormalY=0 NormalZ=1 AngleXU=0 Radius=15.5367
    g7: LineSegment [constr] StartX=9.16631 StartY=17.4359 StartZ=0 EndX=16.9346 EndY=30.891 EndZ=0
    g8: LineSegment [constr] StartX=16.9346 StartY=30.891 StartZ=0 EndX=9.16631 EndY=44.3462 EndZ=0
    g9: LineSegment [constr] StartX=9.16631 StartY=44.3462 StartZ=0 EndX=-6.37036 EndY=44.3462 EndZ=0
    g10: LineSegment [constr] StartX=-6.37036 StartY=44.3462 StartZ=0 EndX=-14.1387 EndY=30.891 EndZ=0
    g11: LineSegment [constr] StartX=-14.1387 StartY=30.891 StartZ=0 EndX=-6.37036 EndY=17.4359 EndZ=0
    g12: LineSegment [constr] StartX=-6.37036 StartY=17.4359 StartZ=0 EndX=9.16631 EndY=17.4359 EndZ=0
    g13: Circle [constr] CenterX=1.39797 CenterY=30.891 CenterZ=0 NormalX=0 NormalY=0 NormalZ=1 AngleXU=0 Radius=15.5367
    g14: GeomPoint X=-6.37036 Y=44.3462 Z=0
    g15: GeomPoint X=-9.58917 Y=23.011 Z=0
    g16: LineSegment StartX=-25.1258 StartY=49.9213 StartZ=0 EndX=-9.58917 EndY=49.9213 EndZ=0
    g17: LineSegment StartX=-9.58917 StartY=49.9213 StartZ=0 EndX=-6.37036 EndY=44.3462 EndZ=0
    g18: LineSegment StartX=-6.37036 StartY=44.3462 StartZ=0 EndX=9.16631 EndY=44.3462 EndZ=0
    g19: LineSegment StartX=9.16631 StartY=44.3462 StartZ=0 EndX=16.9346 EndY=30.891 EndZ=0
    g20: LineSegment StartX=16.9346 StartY=30.891 StartZ=0 EndX=9.16631 EndY=17.4359 EndZ=0
    g21: LineSegment StartX=9.16631 StartY=17.4359 StartZ=0 EndX=-6.37036 EndY=17.4359 EndZ=0
    g22: LineSegment StartX=-6.37036 StartY=17.4359 StartZ=0 EndX=-9.58917 EndY=23.011 EndZ=0
    g23: LineSegment StartX=-9.58917 StartY=23.011 StartZ=0 EndX=-25.1258 EndY=23.011 EndZ=0
    g24: LineSegment StartX=-25.1258 StartY=23.011 StartZ=0 EndX=-32.8942 EndY=36.4661 EndZ=0
    g25: LineSegment StartX=-32.8942 StartY=36.4661 StartZ=0 EndX=-25.1258 EndY=49.9213 EndZ=0
  constraints (53):
    c: Coincident(g0,g1)
    c: Coincident(g1,g2)
    c: Coincident(g2,g3)
    c: Coincident(g3,g4)
    c: Coincident(g4,g5)
    c: Coincident(g5,g0)
    c: Equal(g0, g1-g5) x5
    c: PointOnObject(g0,g6)
    c: PointOnObject(g1,g6)
    c: PointOnObject(g2,g6)
    c: PointOnObject(g3,g6)
    c: PointOnObject(g4,g6)
    c: PointOnObject(g5,g6)
    c: Coincident(g7,g8)
    c: Coincident(g8,g9)
    c: Coincident(g9,g10)
    c: Coincident(g10,g11)
    c: Coincident(g11,g12)
    c: Coincident(g12,g7)
    c: Equal(g7, g8-g12) x5
    c: PointOnObject(g7,g13)
    c: PointOnObject(g8,g13)
    c: PointOnObject(g9,g13)
    c: PointOnObject(g10,g13)
    c: PointOnObject(g11,g13)
    c: PointOnObject(g12,g13)
    c: PointOnObject(g14,g1)
    c: PointOnObject(g15,g0)
    c: Coincident(g16,g2)
    c: Coincident(g16,g1)
    c: Horizontal(g16)
    c: Coincident(g17,g16)
    c: Coincident(g17,g14)
    c: Coincident(g18,g8)
    c: Horizontal(g18)
    c: Coincident(g19,g18)
    c: Coincident(g19,g7)
    c: Coincident(g20,g19)
    c: Coincident(g20,g7)
    c: Coincident(g21,g20)
    c: Coincident(g21,g11)
    c: Coincident(g22,g21)
    c: Coincident(g22,g15)
    c: Coincident(g23,g4)
    c: Coincident(g24,g23)
    c: Coincident(g24,g3)
    c: Coincident(g25,g24)
    c: Coincident(g25,g16)
    c: Parallel(g11,g22)
    c: Coincident(g14,g18)
    c: Coincident(g14,g9)
    c: Coincident(g23,g15)
    c: PointOnObject(g0,g11)
FEATURE [PartDesign::Pocket] Pocket005
  BaseFeature = -> Pad002
  Length = 1.5
  Length2 = 100
  Placement = pos=(0,0,0) rot=(1,0,0;1.5708rad)
  Profile = -> Sketch014
  Type = 0
FEATURE [PartDesign::Chamfer] Chamfer010
  Base = -> Pocket005 [Face3]
  BaseFeature = -> Pocket005
  Placement = pos=(0,0,0) rot=(1,0,0;1.5708rad)
  Size = 1
FEATURE [Sketcher::SketchObject] Sketch015
  MapMode = 5
  Placement = pos=(0,0,0) rot=(-1,0,0;1.5708rad)
  Support = -> [Chamfer010]
  sketch-geometry (1):
    g0: Circle CenterX=0 CenterY=0 CenterZ=0 NormalX=0 NormalY=0 NormalZ=1 AngleXU=0 Radius=64.225
  constraints (1):
    c: Coincident(g0,g-1)
FEATURE [PartDesign::Pocket] Pocket006
  BaseFeature = -> Chamfer010
  Length = 0
  Length2 = 100
  Offset = -3
  Placement = pos=(0,0,0) rot=(1,0,0;1.5708rad)
  Profile = -> Sketch015
  Type = 2
FEATURE [PartDesign::Body] Body002  label="Housing - v3"
  Group = -> [Sketch012,Pad002,Sketch014,Pocket005,Chamfer010,Sketch015,Pocket006]
  Origin = -> Origin002
  Tip = -> Pocket006
FEATURE [Sketcher::SketchObject] Sketch016  label="Faceplate"
  MapMode = 5
  Placement = pos=(0,0,0) rot=(1,0,0;1.5708rad)
  Support = -> [XZ_Plane003]
  sketch-geometry (54):
    g0: LineSegment StartX=-34 StartY=-10.0192 StartZ=0 EndX=-29 EndY=-1.35898 EndZ=0
    g1: LineSegment StartX=-29 StartY=-1.35898 StartZ=0 EndX=-34 EndY=7.30127 EndZ=0
    g2: LineSegment StartX=-34 StartY=7.30127 StartZ=0 EndX=-44 EndY=7.30127 EndZ=0
    g3: LineSegment StartX=-44 StartY=7.30127 StartZ=0 EndX=-49 EndY=-1.35898 EndZ=0
    g4: LineSegment StartX=-49 StartY=-1.35898 StartZ=0 EndX=-44 EndY=-10.0192 EndZ=0
    g5: LineSegment StartX=-44 StartY=-10.0192 StartZ=0 EndX=-34 EndY=-10.0192 EndZ=0
    g6: Circle [constr] CenterX=-39 CenterY=-1.35898 CenterZ=0 NormalX=0 NormalY=0 NormalZ=1 AngleXU=0 Radius=10
    g7: LineSegment StartX=-15 StartY=-21.6795 StartZ=0 EndX=-10 EndY=-13.0192 EndZ=0
    g8: LineSegment StartX=-10 StartY=-13.0192 StartZ=0 EndX=-15 EndY=-4.35898 EndZ=0
    g9: LineSegment StartX=-15 StartY=-4.35898 StartZ=0 EndX=-25 EndY=-4.35898 EndZ=0
    g10: LineSegment StartX=-25 StartY=-4.35898 StartZ=0 EndX=-30 EndY=-13.0192 EndZ=0
    g11: LineSegment StartX=-30 StartY=-13.0192 StartZ=0 EndX=-25 EndY=-21.6795 EndZ=0
    g12: LineSegment StartX=-25 StartY=-21.6795 StartZ=0 EndX=-15 EndY=-21.6795 EndZ=0
    g13: Circle [constr] CenterX=-20 CenterY=-13.0192 CenterZ=0 NormalX=0 NormalY=0 NormalZ=1 AngleXU=0 Radius=10
    g14: LineSegment StartX=-29 StartY=-24.6795 StartZ=0 EndX=-34 EndY=-16.0192 EndZ=0
    g15: LineSegment StartX=-34 StartY=-16.0192 StartZ=0 EndX=-44 EndY=-16.0192 EndZ=0
    g16: LineSegment StartX=-44 StartY=-16.0192 StartZ=0 EndX=-49 EndY=-24.6795 EndZ=0
    g17: LineSegment StartX=-49 StartY=-24.6795 StartZ=0 EndX=-44 EndY=-33.3397 EndZ=0
    g18: LineSegment StartX=-44 StartY=-33.3397 StartZ=0 EndX=-34 EndY=-33.3397 EndZ=0
    g19: LineSegment StartX=-34 StartY=-33.3397 StartZ=0 EndX=-29 EndY=-24.6795 EndZ=0
    g20: Circle [constr] CenterX=-39 CenterY=-24.6795 CenterZ=0 NormalX=0 NormalY=0 NormalZ=1 AngleXU=0 Radius=10
    g21: LineSegment StartX=-15 StartY=-45 StartZ=0 EndX=-10 EndY=-36.3397 EndZ=0
    g22: LineSegment StartX=-10 StartY=-36.3397 StartZ=0 EndX=-15 EndY=-27.6795 EndZ=0
    g23: LineSegment StartX=-15 StartY=-27.6795 StartZ=0 EndX=-25 EndY=-27.6795 EndZ=0
    g24: LineSegment StartX=-25 StartY=-27.6795 StartZ=0 EndX=-30 EndY=-36.3397 EndZ=0
    g25: LineSegment StartX=-30 StartY=-36.3397 StartZ=0 EndX=-25 EndY=-45 EndZ=0
    g26: LineSegment StartX=-25 StartY=-45 StartZ=0 EndX=-15 EndY=-45 EndZ=0
    g27: Circle [constr] CenterX=-20 CenterY=-36.3397 CenterZ=0 NormalX=0 NormalY=0 NormalZ=1 AngleXU=0 Radius=10
    g28: LineSegment StartX=-23 StartY=42 StartZ=0 EndX=8.42 EndY=42 EndZ=0
    g29: LineSegment StartX=8.42 StartY=42 StartZ=0 EndX=8.42 EndY=25.3 EndZ=0
    g30: LineSegment StartX=8.42 StartY=25.3 StartZ=0 EndX=-23 EndY=25.3 EndZ=0
    g31: LineSegment StartX=-23 StartY=25.3 StartZ=0 EndX=-23 EndY=42 EndZ=0
    g32: LineSegment StartX=24 StartY=-20.7846 StartZ=0 EndX=30 EndY=-10.3923 EndZ=0
    g33: LineSegment StartX=30 StartY=-10.3923 StartZ=0 EndX=24 EndY=0 EndZ=0
    g34: LineSegment StartX=24 StartY=0 StartZ=0 EndX=12 EndY=-7e-16 EndZ=0
    g35: LineSegment StartX=12 StartY=-7e-16 StartZ=0 EndX=6 EndY=-10.3923 EndZ=0
    g36: LineSegment StartX=6 StartY=-10.3923 StartZ=0 EndX=12 EndY=-20.7846 EndZ=0
    g37: LineSegment StartX=12 StartY=-20.7846 StartZ=0 EndX=24 EndY=-20.7846 EndZ=0
    g38: Circle [constr] CenterX=18 CenterY=-10.3923 CenterZ=0 NormalX=0 NormalY=0 NormalZ=1 AngleXU=0 Radius=12
    g39: LineSegment StartX=45 StartY=-3 StartZ=0 EndX=51 EndY=7.3923 EndZ=0
    g40: LineSegment StartX=51 StartY=7.3923 StartZ=0 EndX=45 EndY=17.7846 EndZ=0
    g41: LineSegment StartX=45 StartY=17.7846 StartZ=0 EndX=33 EndY=17.7846 EndZ=0
    g42: LineSegment StartX=33 StartY=17.7846 StartZ=0 EndX=27 EndY=7.3923 EndZ=0
    g43: LineSegment StartX=27 StartY=7.3923 StartZ=0 EndX=33 EndY=-3 EndZ=0
    g44: LineSegment StartX=33 StartY=-3 StartZ=0 EndX=45 EndY=-3 EndZ=0
    g45: Circle [constr] CenterX=39 CenterY=7.3923 CenterZ=0 NormalX=0 NormalY=0 NormalZ=1 AngleXU=0 Radius=12
    g46: LineSegment StartX=-47 StartY=60 StartZ=0 EndX=47 EndY=60 EndZ=0
    g47: LineSegment StartX=60 StartY=47 StartZ=0 EndX=60 EndY=-47 EndZ=0
    g48: LineSegment StartX=47 StartY=-60 StartZ=0 EndX=-47 EndY=-60 EndZ=0
    g49: LineSegment StartX=-60 StartY=-47 StartZ=0 EndX=-60 EndY=47 EndZ=0
    g50: ArcOfCircle CenterX=-47 CenterY=47 CenterZ=0 NormalX=0 NormalY=0 NormalZ=1 AngleXU=0 Radius=13 StartAngle=1.5708 EndAngle=3.14159
    g51: ArcOfCircle CenterX=47 CenterY=47 CenterZ=0 NormalX=0 NormalY=0 NormalZ=1 AngleXU=0 Radius=13 StartAngle=0 EndAngle=1.5708
    g52: ArcOfCircle CenterX=47 CenterY=-47 CenterZ=0 NormalX=0 NormalY=0 NormalZ=1 AngleXU=0 Radius=13 StartAngle=4.71239 EndAngle=6.28319
    g53: ArcOfCircle CenterX=-47 CenterY=-47 CenterZ=0 NormalX=0 NormalY=0 NormalZ=1 AngleXU=0 Radius=13 StartAngle=3.14159 EndAngle=4.71239
  constraints (133):
    c: Coincident(g0,g1)
    c: Coincident(g1,g2)
    c: Coincident(g2,g3)
    c: Coincident(g3,g4)
    c: Coincident(g4,g5)
    c: Coincident(g5,g0)
    c: Equal(g0, g1-g5) x5
    c: PointOnObject(g0,g6)
    c: PointOnObject(g1,g6)
    c: PointOnObject(g2,g6)
    c: PointOnObject(g3,g6)
    c: PointOnObject(g4,g6)
    c: PointOnObject(g5,g6)
    c: Parallel(g2,g-1)
    c: Radius(g6) = 10
    c: Coincident(g7,g8)
    c: Coincident(g8,g9)
    c: Coincident(g9,g10)
    c: Coincident(g10,g11)
    c: Coincident(g11,g12)
    c: Coincident(g12,g7)
    c: Equal(g7, g8-g12) x5
    c: PointOnObject(g7,g13)
    c: PointOnObject(g8,g13)
    c: PointOnObject(g9,g13)
    c: PointOnObject(g10,g13)
    c: PointOnObject(g11,g13)
    c: PointOnObject(g12,g13)
    c: Parallel(g9,g-1)
    c: Radius(g13) = 10
    c: DistanceX(g0,g9) = 4
    c: DistanceY(g9,g0) = 3
    c: Coincident(g14,g15)
    c: Coincident(g15,g16)
    c: Coincident(g16,g17)
    c: Coincident(g17,g18)
    c: Coincident(g18,g19)
    c: Coincident(g19,g14)
    c: Equal(g14, g15-g19) x5
    c: PointOnObject(g14,g20)
    c: PointOnObject(g15,g20)
    c: PointOnObject(g16,g20)
    c: PointOnObject(g17,g20)
    c: PointOnObject(g18,g20)
    c: PointOnObject(g19,g20)
    c: Parallel(g15,g-1)
    c: Radius(g20) = 10
    c: DistanceX(g14,g10) = 4
    c: DistanceY(g14,g10) = 3
    c: Coincident(g21,g22)
    c: Coincident(g22,g23)
    c: Coincident(g23,g24)
    c: Coincident(g24,g25)
    c: Coincident(g25,g26)
    c: Coincident(g26,g21)
    c: Equal(g21, g22-g26) x5
    c: PointOnObject(g21,g27)
    c: PointOnObject(g22,g27)
    c: PointOnObject(g23,g27)
    c: PointOnObject(g24,g27)
    c: PointOnObject(g25,g27)
    c: PointOnObject(g26,g27)
    c: Parallel(g23,g-1)
    c: Radius(g27) = 10
    c: DistanceX(g14,g23) = 4
    c: DistanceY(g23,g14) = 3
    c: Coincident(g28,g29)
    c: Coincident(g29,g30)
    c: Coincident(g30,g31)
    c: Coincident(g31,g28)
    c: Horizontal(g28)
    c: Horizontal(g30)
    c: Vertical(g29)
    c: Vertical(g31)
    c: DistanceX(g28,g28) = 31.42
    c: DistanceY(g31,g31) = 16.7
    c: Coincident(g32,g33)
    c: Coincident(g33,g34)
    c: Coincident(g34,g35)
    c: Coincident(g35,g36)
    c: Coincident(g36,g37)
    c: Coincident(g37,g32)
    c: Equal(g32, g33-g37) x5
    c: PointOnObject(g32,g38)
    c: PointOnObject(g33,g38)
    c: PointOnObject(g34,g38)
    c: PointOnObject(g35,g38)
    c: PointOnObject(g36,g38)
    c: PointOnObject(g37,g38)
    c: Parallel(g34,g30)
    c: Radius(g38) = 12
    c: Coincident(g39,g40)
    c: Coincident(g40,g41)
    c: Coincident(g41,g42)
    c: Coincident(g42,g43)
    c: Coincident(g43,g44)
    c: Coincident(g44,g39)
    c: Equal(g39, g40-g44) x5
    c: PointOnObject(g39,g45)
    c: PointOnObject(g40,g45)
    c: PointOnObject(g41,g45)
    c: PointOnObject(g42,g45)
    c: PointOnObject(g43,g45)
    c: PointOnObject(g44,g45)
    c: Radius(g45) = 12
    c: Parallel(g41,g30)
    c: DistanceY(g43,g33) = 3
    c: DistanceX(g33,g42) = 3
    c: Horizontal(g46)
    c: Horizontal(g48)
    c: Vertical(g47)
    c: Vertical(g49)
    c: Equal(g46,g47)
    c: Tangent(g49,g50) = 1.5708
    c: Tangent(g46,g50) = 1.5708
    c: Tangent(g46,g51) = 1.5708
    c: Tangent(g47,g51) = 1.5708
    c: Tangent(g47,g52) = 1.5708
    c: Tangent(g48,g52) = 1.5708
    c: Tangent(g49,g53) = 1.5708
    c: Tangent(g48,g53) = 1.5708
    c: Equal(g53,g50)
    c: Equal(g50,g51)
    c: Equal(g51,g52)
    c: Symmetric(g50,g52,g-1)
    c: Radius(g50) = 13
    c: DistanceY(g48,g46) = 120
    c: DistanceX(g49,g28) = 37
    c: DistanceY(g28,g46) = 18
    c: DistanceX(g34,g46) = 35
    c: DistanceY(g34,g46) = 60
    c: DistanceX(g49,g17) = 16
    c: DistanceY(g48,g25) = 15
FEATURE [PartDesign::Pad] Pad003
  Length = 30
  Length2 = 100
  Placement = pos=(0,0,0) rot=(1,0,0;1.5708rad)
  Profile = -> Sketch016
  Type = 0
FEATURE [Sketcher::SketchObject] Sketch017  label="Display hollow"
  MapMode = 5
  Placement = pos=(0,-30,3.3e-14) rot=(1,0,0;1.5708rad)
  sketch-geometry (26):
    g0: LineSegment [constr] StartX=-9.59 StartY=23.012 StartZ=0 EndX=-1.82 EndY=36.47 EndZ=0
    g1: LineSegment [constr] StartX=-1.82 StartY=36.47 StartZ=0 EndX=-9.59 EndY=49.928 EndZ=0
    g2: LineSegment [constr] StartX=-9.59 StartY=49.928 StartZ=0 EndX=-25.13 EndY=49.928 EndZ=0
    g3: LineSegment [constr] StartX=-25.13 StartY=49.928 StartZ=0 EndX=-32.9 EndY=36.47 EndZ=0
    g4: LineSegment [constr] StartX=-32.9 StartY=36.47 StartZ=0 EndX=-25.13 EndY=23.012 EndZ=0
    g5: LineSegment [constr] StartX=-25.13 StartY=23.012 StartZ=0 EndX=-9.59 EndY=23.012 EndZ=0
    g6: Circle [constr] CenterX=-17.36 CenterY=36.47 CenterZ=0 NormalX=0 NormalY=0 NormalZ=1 AngleXU=0 Radius=15.54
    g7: LineSegment [constr] StartX=9.17 StartY=17.4348 StartZ=0 EndX=16.94 EndY=30.8928 EndZ=0
    g8: LineSegment [constr] StartX=16.94 StartY=30.8928 StartZ=0 EndX=9.17 EndY=44.3508 EndZ=0
    g9: LineSegment [constr] StartX=9.17 StartY=44.3508 StartZ=0 EndX=-6.37 EndY=44.3508 EndZ=0
    g10: LineSegment [constr] StartX=-6.37 StartY=44.3508 StartZ=0 EndX=-14.14 EndY=30.8928 EndZ=0
    g11: LineSegment [constr] StartX=-14.14 StartY=30.8928 StartZ=0 EndX=-6.37 EndY=17.4348 EndZ=0
    g12: LineSegment [constr] StartX=-6.37 StartY=17.4348 StartZ=0 EndX=9.17 EndY=17.4348 EndZ=0
    g13: Circle [constr] CenterX=1.4 CenterY=30.8928 CenterZ=0 NormalX=0 NormalY=0 NormalZ=1 AngleXU=0 Radius=15.54
    g14: GeomPoint X=-6.37 Y=44.3508 Z=0
    g15: GeomPoint X=-9.59 Y=23.012 Z=0
    g16: LineSegment StartX=-25.13 StartY=49.928 StartZ=0 EndX=-9.59 EndY=49.928 EndZ=0
    g17: LineSegment StartX=-9.59 StartY=49.928 StartZ=0 EndX=-6.37 EndY=44.3508 EndZ=0
    g18: LineSegment StartX=-6.37 StartY=44.3508 StartZ=0 EndX=9.17 EndY=44.3508 EndZ=0
    g19: LineSegment StartX=9.17 StartY=44.3508 StartZ=0 EndX=16.94 EndY=30.8928 EndZ=0
    g20: LineSegment StartX=16.94 StartY=30.8928 StartZ=0 EndX=9.17 EndY=17.4348 EndZ=0
    g21: LineSegment StartX=9.17 StartY=17.4348 StartZ=0 EndX=-6.37 EndY=17.4348 EndZ=0
    g22: LineSegment StartX=-6.37 StartY=17.4348 StartZ=0 EndX=-9.59 EndY=23.012 EndZ=0
    g23: LineSegment StartX=-9.59 StartY=23.012 StartZ=0 EndX=-25.13 EndY=23.012 EndZ=0
    g24: LineSegment StartX=-25.13 StartY=23.012 StartZ=0 EndX=-32.9 EndY=36.47 EndZ=0
    g25: LineSegment StartX=-32.9 StartY=36.47 StartZ=0 EndX=-25.13 EndY=49.928 EndZ=0
  constraints (57):
    c: Coincident(g0,g1)
    c: Coincident(g1,g2)
    c: Coincident(g2,g3)
    c: Coincident(g3,g4)
    c: Coincident(g4,g5)
    c: Coincident(g5,g0)
    c: Equal(g0, g1-g5) x5
    c: PointOnObject(g0,g6)
    c: PointOnObject(g1,g6)
    c: PointOnObject(g2,g6)
    c: PointOnObject(g3,g6)
    c: PointOnObject(g4,g6)
    c: PointOnObject(g5,g6)
    c: Coincident(g7,g8)
    c: Coincident(g8,g9)
    c: Coincident(g9,g10)
    c: Coincident(g10,g11)
    c: Coincident(g11,g12)
    c: Coincident(g12,g7)
    c: Equal(g7, g8-g12) x5
    c: PointOnObject(g7,g13)
    c: PointOnObject(g8,g13)
    c: PointOnObject(g9,g13)
    c: PointOnObject(g10,g13)
    c: PointOnObject(g11,g13)
    c: PointOnObject(g12,g13)
    c: PointOnObject(g14,g1)
    c: PointOnObject(g15,g0)
    c: Coincident(g16,g2)
    c: Coincident(g16,g1)
    c: Horizontal(g16)
    c: Coincident(g17,g16)
    c: Coincident(g17,g14)
    c: Coincident(g18,g8)
    c: Horizontal(g18)
    c: Coincident(g19,g18)
    c: Coincident(g19,g7)
    c: Coincident(g20,g19)
    c: Coincident(g20,g7)
    c: Coincident(g21,g20)
    c: Coincident(g21,g11)
    c: Coincident(g22,g21)
    c: Coincident(g22,g15)
    c: Coincident(g23,g4)
    c: Coincident(g24,g23)
    c: Coincident(g24,g3)
    c: Coincident(g25,g24)
    c: Coincident(g25,g16)
    c: Parallel(g11,g22)
    c: Coincident(g14,g18)
    c: Coincident(g14,g9)
    c: Coincident(g23,g15)
    c: PointOnObject(g0,g11)
    c: DistanceX(g-1,g13) = 1.4
    c: DistanceY(g-1,g6) = 36.47
    c: DistanceX(g6,g13) = 18.76
    c: DistanceX(g18,g18) = 15.54
FEATURE [PartDesign::Pocket] Pocket007
  BaseFeature = -> Pad003
  Length = 1
  Length2 = 100
  Placement = pos=(0,0,0) rot=(1,0,0;1.5708rad)
  Profile = -> Sketch017
  Type = 0
FEATURE [Sketcher::SketchObject] Sketch019  label="Wall"
  ExternalGeometry = -> [Pocket007]
  MapMode = 5
  Placement = pos=(0,0,0) rot=(-1,0,0;1.5708rad)
  Support = -> [Pocket007]
  sketch-geometry (8):
    g0: LineSegment StartX=-45 StartY=58 StartZ=0 EndX=45 EndY=58 EndZ=0
    g1: LineSegment StartX=58 StartY=45 StartZ=0 EndX=58 EndY=-45 EndZ=0
    g2: LineSegment StartX=45 StartY=-58 StartZ=0 EndX=-45 EndY=-58 EndZ=0
    g3: LineSegment StartX=-58 StartY=-45 StartZ=0 EndX=-58 EndY=45 EndZ=0
    g4: ArcOfCircle CenterX=45 CenterY=45 CenterZ=0 NormalX=0 NormalY=0 NormalZ=1 AngleXU=0 Radius=13 StartAngle=0 EndAngle=1.5708
    g5: ArcOfCircle CenterX=-45 CenterY=45 CenterZ=0 NormalX=0 NormalY=0 NormalZ=1 AngleXU=0 Radius=13 StartAngle=1.5708 EndAngle=3.14159
    g6: ArcOfCircle CenterX=-45 CenterY=-45 CenterZ=0 NormalX=0 NormalY=0 NormalZ=1 AngleXU=0 Radius=13 StartAngle=3.14159 EndAngle=4.71239
    g7: ArcOfCircle CenterX=45 CenterY=-45 CenterZ=0 NormalX=0 NormalY=0 NormalZ=1 AngleXU=0 Radius=13 StartAngle=4.71239 EndAngle=6.28319
  constraints (20):
    c: Horizontal(g0)
    c: Horizontal(g2)
    c: Vertical(g1)
    c: Vertical(g3)
    c: Tangent(g0,g4) = 1.5708
    c: Tangent(g1,g4) = 1.5708
    c: Tangent(g0,g5) = 1.5708
    c: Tangent(g3,g5) = 1.5708
    c: Tangent(g3,g6) = 1.5708
    c: Tangent(g2,g6) = 1.5708
    c: Tangent(g1,g7) = 1.5708
    c: Tangent(g2,g7) = 1.5708
    c: Equal(g7,g4)
    c: Equal(g4,g5)
    c: Equal(g5,g6)
    c: Radius(g5) = 13
    c: DistanceX(g-3,g3) = 2
    c: DistanceY(g0,g-4) = 2
    c: DistanceX(g1,g-5) = 2
    c: DistanceY(g-6,g2) = 2
FEATURE [PartDesign::Pocket] Pocket008  label="Internal pocket"
  BaseFeature = -> Pocket007
  Length = 27
  Length2 = 100
  Placement = pos=(0,0,0) rot=(1,0,0;1.5708rad)
  Profile = -> Sketch019
  Type = 0
FEATURE [Sketcher::SketchObject] Sketch020
  ExternalGeometry = -> [Pocket008,Sketch016]
  MapMode = 5
  Placement = pos=(0,-27,1.19e-14) rot=(-1,0,0;1.5708rad)
  Support = -> [Pocket008]
  sketch-geometry (22):
    g0: Circle CenterX=-48 CenterY=48 CenterZ=0 NormalX=0 NormalY=0 NormalZ=1 AngleXU=0 Radius=0.9
    g1: Circle CenterX=-48 CenterY=48 CenterZ=0 NormalX=0 NormalY=0 NormalZ=1 AngleXU=0 Radius=3
    g2: Circle CenterX=48 CenterY=48 CenterZ=0 NormalX=0 NormalY=0 NormalZ=1 AngleXU=0 Radius=0.9
    g3: Circle CenterX=48 CenterY=48 CenterZ=0 NormalX=0 NormalY=0 NormalZ=1 AngleXU=0 Radius=3
    g4: Circle CenterX=-48 CenterY=-48 CenterZ=0 NormalX=0 NormalY=0 NormalZ=1 AngleXU=0 Radius=0.9
    g5: Circle CenterX=-48 CenterY=-48 CenterZ=0 NormalX=0 NormalY=0 NormalZ=1 AngleXU=0 Radius=3
    g6: Circle CenterX=48 CenterY=-48 CenterZ=0 NormalX=0 NormalY=0 NormalZ=1 AngleXU=0 Radius=0.9
    g7: Circle CenterX=48 CenterY=-48 CenterZ=0 NormalX=0 NormalY=0 NormalZ=1 AngleXU=0 Radius=3
    g8: LineSegment [constr] StartX=-48 StartY=48 StartZ=0 EndX=48 EndY=48 EndZ=0
    g9: LineSegment [constr] StartX=48 StartY=48 StartZ=0 EndX=48 EndY=-48 EndZ=0
    g10: LineSegment [constr] StartX=48 StartY=-48 StartZ=0 EndX=-48 EndY=-48 EndZ=0
    g11: LineSegment [constr] StartX=-48 StartY=-48 StartZ=0 EndX=-48 EndY=48 EndZ=0
    g12: LineSegment [constr] StartX=53 StartY=-53 StartZ=0 EndX=-53 EndY=-53 EndZ=0
    g13: LineSegment [constr] StartX=-53 StartY=-53 StartZ=0 EndX=-53 EndY=53 EndZ=0
    g14: LineSegment [constr] StartX=-53 StartY=53 StartZ=0 EndX=53 EndY=53 EndZ=0
    g15: LineSegment [constr] StartX=53 StartY=53 StartZ=0 EndX=53 EndY=-53 EndZ=0
    g16: Circle [constr] CenterX=-20 CenterY=36.3397 CenterZ=0 NormalX=0 NormalY=0 NormalZ=1 AngleXU=0 Radius=10
    g17: Circle [constr] CenterX=-39 CenterY=24.6795 CenterZ=0 NormalX=0 NormalY=0 NormalZ=1 AngleXU=0 Radius=10
    g18: Circle [constr] CenterX=-20 CenterY=13.0192 CenterZ=0 NormalX=0 NormalY=0 NormalZ=1 AngleXU=0 Radius=10
    g19: Circle [constr] CenterX=-39 CenterY=1.35898 CenterZ=0 NormalX=0 NormalY=0 NormalZ=1 AngleXU=0 Radius=10
    g20: Circle [constr] CenterX=18 CenterY=10.3923 CenterZ=0 NormalX=0 NormalY=0 NormalZ=1 AngleXU=0 Radius=12
    g21: Circle [constr] CenterX=39 CenterY=-7.3923 CenterZ=0 NormalX=0 NormalY=0 NormalZ=1 AngleXU=0 Radius=12
  constraints (76):
    c: Coincident(g1,g0)
    c: Coincident(g5,g4)
    c: Coincident(g7,g6)
    c: Equal(g4,g6)
    c: Equal(g6,g2)
    c: Equal(g2,g0)
    c: Equal(g1,g3)
    c: Equal(g3,g7)
    c: Equal(g7,g5)
    c: Radius(g0) = 0.9
    c: Radius(g1) = 3
    c: Coincident(g8,g9)
    c: Coincident(g9,g10)
    c: Coincident(g10,g11)
    c: Coincident(g11,g8)
    c: Horizontal(g8)
    c: Horizontal(g10)
    c: Vertical(g9)
    c: Vertical(g11)
    c: Coincident(g8,g0)
    c: Coincident(g9,g6)
    c: Coincident(g8,g2)
    c: Coincident(g3,g2)
    c: Coincident(g4,g10)
    c: Symmetric(g0,g6,g-1)
    c: DistanceY(g2,g-3) = 10
    c: DistanceX(g2,g-5) = 10
    c: DistanceX(g10,g10) = 96
    c: DistanceY(g4,g0) = 96
    c: Coincident(g12,g13)
    c: Coincident(g13,g14)
    c: Coincident(g14,g15)
    c: Coincident(g15,g12)
    c: Horizontal(g12)
    c: Horizontal(g14)
    c: Vertical(g13)
    c: Vertical(g15)
    c: Symmetric(g12,g13,g-1)
    c: DistanceX(g12,g12) = 106
    c: DistanceY(g15,g15) = 106
    c: DistanceX(g6,g12) = 5
    c: DistanceX(g4,g12) = 101
    c: PointOnObject(g-7,g16)
    c: PointOnObject(g-8,g16)
    c: PointOnObject(g-9,g16)
    c: PointOnObject(g-10,g17)
    c: PointOnObject(g-11,g17)
    c: PointOnObject(g-12,g17)
    c: PointOnObject(g-13,g18)
    c: PointOnObject(g-14,g18)
    c: PointOnObject(g-15,g18)
    c: PointOnObject(g-16,g19)
    c: PointOnObject(g-17,g19)
    c: PointOnObject(g-18,g19)
    c: PointOnObject(g-19,g20)
    c: PointOnObject(g-20,g20)
    c: PointOnObject(g-21,g20)
    c: PointOnObject(g-22,g21)
    c: PointOnObject(g-23,g21)
    c: PointOnObject(g-24,g21)
    c: DistanceX(g21,g12) = 14
    c: DistanceY(g12,g21) = 45.6077
    c: DistanceX(g20,g12) = 35
    c: DistanceY(g12,g20) = 63.3923
    c: DistanceX(g18,g12) = 73
    c: DistanceY(g12,g18) = 66.0192
    c: DistanceX(g19,g12) = 92
    c: DistanceY(g12,g19) = 54.359
    c: DistanceX(g16,g12) = 73
    c: DistanceY(g12,g16) = 89.3397
    c: DistanceX(g17,g12) = 92
    c: DistanceY(g12,g17) = 77.6795
    c: DistanceX(g-25,g12) = 44.58
    c: DistanceX(g-26,g12) = 76
    c: DistanceY(g12,g-25) = 11
    c: DistanceY(g12,g-28) = 27.7
FEATURE [PartDesign::Pad] Pad004  label="PCB screw holes"
  BaseFeature = -> Pocket008
  Length = 8
  Length2 = 100
  Placement = pos=(0,0,0) rot=(1,0,0;1.5708rad)
  Profile = -> Sketch020
  Type = 0
FEATURE [Sketcher::SketchObject] Sketch021
  ExternalGeometry = -> [Pad004]
  MapMode = 5
  Placement = pos=(0,-27,1.19e-14) rot=(-1,0,0;1.5708rad)
  Support = -> [Pad004]
  sketch-geometry (8):
    g0: Circle CenterX=-23 CenterY=-20.3 CenterZ=0 NormalX=0 NormalY=0 NormalZ=1 AngleXU=0 Radius=0.9
    g1: Circle CenterX=-23 CenterY=-20.3 CenterZ=0 NormalX=0 NormalY=0 NormalZ=1 AngleXU=0 Radius=1.8
    g2: Circle CenterX=-23 CenterY=-46.5 CenterZ=0 NormalX=0 NormalY=0 NormalZ=1 AngleXU=0 Radius=0.9
    g3: Circle CenterX=-23 CenterY=-46.5 CenterZ=0 NormalX=0 NormalY=0 NormalZ=1 AngleXU=0 Radius=1.8
    g4: Circle CenterX=8.42 CenterY=-46.5 CenterZ=0 NormalX=0 NormalY=0 NormalZ=1 AngleXU=0 Radius=0.9
    g5: Circle CenterX=8.42 CenterY=-46.5 CenterZ=0 NormalX=0 NormalY=0 NormalZ=1 AngleXU=0 Radius=1.8
    g6: Circle CenterX=8.42 CenterY=-20.3 CenterZ=0 NormalX=0 NormalY=0 NormalZ=1 AngleXU=0 Radius=0.9
    g7: Circle CenterX=8.42 CenterY=-20.3 CenterZ=0 NormalX=0 NormalY=0 NormalZ=1 AngleXU=0 Radius=1.8
  constraints (20):
    c: Coincident(g1,g0)
    c: Radius(g0) = 0.9
    c: Radius(g1) = 1.8
    c: Coincident(g3,g2)
    c: Coincident(g5,g4)
    c: Coincident(g7,g6)
    c: Equal(g0,g6)
    c: Equal(g6,g2)
    c: Equal(g2,g4)
    c: Equal(g1,g7)
    c: Equal(g7,g3)
    c: Equal(g3,g5)
    c: DistanceX(g2,g-4) = 0
    c: DistanceX(g4,g-4) = 0
    c: DistanceY(g2,g-4) = 4.5
    c: DistanceY(g4,g-4) = 4.5
    c: DistanceX(g0,g-3) = 0
    c: DistanceX(g6,g-3) = 0
    c: DistanceY(g-3,g0) = 5
    c: DistanceY(g-3,g6) = 5
FEATURE [PartDesign::Pad] Pad005  label="Display screw holes"
  BaseFeature = -> Pad004
  Length = 2
  Length2 = 100
  Placement = pos=(0,0,0) rot=(1,0,0;1.5708rad)
  Profile = -> Sketch021
  Type = 0
FEATURE [Sketcher::SketchObject] Sketch022
  ExternalGeometry = -> [Pad005]
  MapMode = 5
  Placement = pos=(1.65e-14,-25,3.41e-14) rot=(-1,0,0;1.5708rad)
  Support = -> [Pad005]
  sketch-geometry (4):
    g0: Circle CenterX=-23 CenterY=-46.5 CenterZ=0 NormalX=0 NormalY=0 NormalZ=1 AngleXU=0 Radius=0.9
    g1: Circle CenterX=8.42 CenterY=-20.3 CenterZ=0 NormalX=0 NormalY=0 NormalZ=1 AngleXU=0 Radius=0.9
    g2: Circle CenterX=-23 CenterY=-20.3 CenterZ=0 NormalX=0 NormalY=0 NormalZ=1 AngleXU=0 Radius=0.9
    g3: Circle CenterX=8.42 CenterY=-46.5 CenterZ=0 NormalX=0 NormalY=0 NormalZ=1 AngleXU=0 Radius=0.9
  constraints (8):
    c: Coincident(g0,g-3)
    c: Coincident(g1,g-4)
    c: Coincident(g2,g-6)
    c: Coincident(g3,g-5)
    c: Equal(g0,g-3)
    c: Equal(g-3,g1)
    c: Equal(g1,g3)
    c: Equal(g3,g2)
FEATURE [PartDesign::Pocket] Pocket009  label="Display screw deep holes"
  BaseFeature = -> Pad005
  Length = 2.4
  Length2 = 100
  Placement = pos=(0,0,0) rot=(1,0,0;1.5708rad)
  Profile = -> Sketch022
  Type = 0
FEATURE [App::Part] TopV
  Origin = -> Origin010
FEATURE [App::Part] BotV
  Origin = -> Origin011
FEATURE [App::Part] Step_Virtual_Models
  Group = -> [TopV,BotV]
  Origin = -> Origin009
FEATURE [App::Part] Bot
  Origin = -> Origin005
FEATURE [App::Part] Top
  Origin = -> Origin008
FEATURE [App::Part] Step_Models
  Group = -> [Top,Bot]
  Origin = -> Origin006
FEATURE [PartDesign::CoordinateSystem] Local_CS
  AttacherType = Attacher::AttachEngine3D
FEATURE [Sketcher::SketchObject] PCB_Sketch
  sketch-geometry (32):
    g0: LineSegment StartX=17.1 StartY=-13.8 StartZ=0 EndX=17.1 EndY=-11.1 EndZ=0
    g1: LineSegment StartX=16.6 StartY=-13.8 StartZ=0 EndX=17.1 EndY=-13.8 EndZ=0
    g2: LineSegment StartX=16.6 StartY=-11.1 StartZ=0 EndX=16.6 EndY=-13.8 EndZ=0
    g3: LineSegment StartX=17.1 StartY=-11.1 StartZ=0 EndX=16.6 EndY=-11.1 EndZ=0
    g4: LineSegment StartX=16.6 StartY=-21.3 StartZ=0 EndX=17.1 EndY=-21.3 EndZ=0
    g5: LineSegment StartX=16.6 StartY=-18.6 StartZ=0 EndX=16.6 EndY=-21.3 EndZ=0
    g6: LineSegment StartX=17.1 StartY=-18.6 StartZ=0 EndX=16.6 EndY=-18.6 EndZ=0
    g7: LineSegment StartX=17.1 StartY=-21.3 StartZ=0 EndX=17.1 EndY=-18.6 EndZ=0
    g8: LineSegment StartX=3 StartY=-10 StartZ=0 EndX=3 EndY=-9 EndZ=0
    g9: LineSegment StartX=7 StartY=-10 StartZ=0 EndX=3 EndY=-10 EndZ=0
    g10: LineSegment StartX=7 StartY=-9 StartZ=0 EndX=7 EndY=-10 EndZ=0
    g11: LineSegment StartX=3 StartY=-9 StartZ=0 EndX=7 EndY=-9 EndZ=0
    g12: LineSegment StartX=98 StartY=-9.6 StartZ=0 EndX=98 EndY=-9 EndZ=0
    g13: LineSegment StartX=104 StartY=-9.6 StartZ=0 EndX=98 EndY=-9.6 EndZ=0
    g14: LineSegment StartX=104 StartY=-9 StartZ=0 EndX=104 EndY=-9.6 EndZ=0
    g15: LineSegment StartX=98 StartY=-9 StartZ=0 EndX=104 EndY=-9 EndZ=0
    g16: LineSegment StartX=86.6 StartY=-7 StartZ=0 EndX=86.6 EndY=-7.6 EndZ=0
    g17: LineSegment StartX=91.1 StartY=-7 StartZ=0 EndX=86.6 EndY=-7 EndZ=0
    g18: LineSegment StartX=91.1 StartY=-7.6 StartZ=0 EndX=91.1 EndY=-7 EndZ=0
    g19: LineSegment StartX=86.6 StartY=-7.6 StartZ=0 EndX=91.1 EndY=-7.6 EndZ=0
    g20: LineSegment StartX=75 StartY=-43 StartZ=0 EndX=75 EndY=-42 EndZ=0
    g21: LineSegment StartX=82 StartY=-43 StartZ=0 EndX=75 EndY=-43 EndZ=0
    g22: LineSegment StartX=82 StartY=-42 StartZ=0 EndX=82 EndY=-43 EndZ=0
    g23: LineSegment StartX=75 StartY=-42 StartZ=0 EndX=82 EndY=-42 EndZ=0
    g24: LineSegment StartX=80 StartY=-48 StartZ=0 EndX=80 EndY=-49 EndZ=0
    g25: LineSegment StartX=101 StartY=-48 StartZ=0 EndX=80 EndY=-48 EndZ=0
    g26: LineSegment StartX=101 StartY=-49 StartZ=0 EndX=101 EndY=-48 EndZ=0
    g27: LineSegment StartX=80 StartY=-49 StartZ=0 EndX=101 EndY=-49 EndZ=0
    g28: LineSegment StartX=0 StartY=0 StartZ=0 EndX=0 EndY=-106 EndZ=0
    g29: LineSegment StartX=0 StartY=-106 StartZ=0 EndX=106 EndY=-106 EndZ=0
    g30: LineSegment StartX=106 StartY=0 StartZ=0 EndX=106 EndY=-106 EndZ=0
    g31: LineSegment StartX=0 StartY=0 StartZ=0 EndX=106 EndY=0 EndZ=0
  constraints (32):
    c: Coincident(g28,g29)
    c: Coincident(g31,g28)
    c: Coincident(g8,g9)
    c: Coincident(g11,g8)
    c: Coincident(g10,g9)
    c: Coincident(g11,g10)
    c: Coincident(g4,g5)
    c: Coincident(g5,g6)
    c: Coincident(g1,g2)
    c: Coincident(g2,g3)
    c: Coincident(g4,g7)
    c: Coincident(g6,g7)
    c: Coincident(g1,g0)
    c: Coincident(g3,g0)
    c: Coincident(g21,g20)
    c: Coincident(g20,g23)
    c: Coincident(g24,g27)
    c: Coincident(g24,g25)
    c: Coincident(g21,g22)
    c: Coincident(g22,g23)
    c: Coincident(g19,g16)
    c: Coincident(g16,g17)
    c: Coincident(g18,g19)
    c: Coincident(g17,g18)
    c: Coincident(g12,g13)
    c: Coincident(g12,g15)
    c: Coincident(g26,g27)
    c: Coincident(g25,g26)
    c: Coincident(g13,g14)
    c: Coincident(g15,g14)
    c: Coincident(g29,g30)
    c: Coincident(g30,g31)
FEATURE [Part::Feature] Pcb
  Placement = pos=(-20,20,0) rot=(0,0,1;0rad)
  shape: bbox 106 x 106 x 1.6 mm, 75 faces (baked)
FEATURE [Part::Feature] botTracks
  Placement = pos=(-20,20,-1.61) rot=(0,0,1;0rad)
  shape: bbox 104.8 x 104.8 x 0.04 mm, 153 faces, 0 solids (baked)
FEATURE [Part::Feature] topTracks
  Placement = pos=(-20,20,0.01) rot=(0,0,1;0rad)
  shape: bbox 104.8 x 104.8 x 0.04 mm, 255 faces, 0 solids (baked)
FEATURE [App::Part] Board_Geoms
  Group = -> [Local_CS,Pcb,PCB_Sketch,topTracks,botTracks]
  Origin = -> Origin007
FEATURE [App::Part] Board  label="Test1"
  Group = -> [Board_Geoms,Step_Models,Step_Virtual_Models]
  Origin = -> Origin004
  Placement = pos=(53,-17,53) rot=(0,0.707107,0.707107;3.14159rad)
FEATURE [Sketcher::SketchObject] Sketch023
  MapMode = 5
  Placement = pos=(0,0,0) rot=(1,0,0;1.5708rad)
  Support = -> [XZ_Plane012]
  sketch-geometry (8):
    g0: LineSegment StartX=-9.6 StartY=0 StartZ=0 EndX=-4.8 EndY=-8.31384 EndZ=0
    g1: LineSegment StartX=-4.8 StartY=-8.31384 StartZ=0 EndX=4.8 EndY=-8.31384 EndZ=0
    g2: LineSegment StartX=4.8 StartY=-8.31384 StartZ=0 EndX=9.6 EndY=0 EndZ=0
    g3: LineSegment StartX=9.6 StartY=0 StartZ=0 EndX=4.8 EndY=8.31384 EndZ=0
    g4: LineSegment StartX=4.8 StartY=8.31384 StartZ=0 EndX=-4.8 EndY=8.31384 EndZ=0
    g5: LineSegment StartX=-4.8 StartY=8.31384 StartZ=0 EndX=-9.6 EndY=0 EndZ=0
    g6: Circle [constr] CenterX=0 CenterY=0 CenterZ=0 NormalX=0 NormalY=0 NormalZ=1 AngleXU=0 Radius=9.6
    g7: LineSegment [constr] StartX=-9.6 StartY=0 StartZ=0 EndX=9.6 EndY=0 EndZ=0
  constraints (19):
    c: Coincident(g0,g1)
    c: Coincident(g1,g2)
    c: Coincident(g2,g3)
    c: Coincident(g3,g4)
    c: Coincident(g4,g5)
    c: Coincident(g5,g0)
    c: Equal(g0, g1-g5) x5
    c: PointOnObject(g0,g6)
    c: PointOnObject(g1,g6)
    c: PointOnObject(g2,g6)
    c: PointOnObject(g3,g6)
    c: PointOnObject(g4,g6)
    c: PointOnObject(g5,g6)
    c: Radius(g6) = 9.6
    c: Coincident(g7,g0)
    c: Coincident(g7,g2)
    c: Horizontal(g7)
    c: Coincident(g6,g-1)
    c: Distance(g0,g2) = 16.6277
FEATURE [PartDesign::Pad] Pad006
  Length = 4
  Length2 = 100
  Placement = pos=(0,0,0) rot=(1,0,0;1.5708rad)
  Profile = -> Sketch023
  Type = 0
FEATURE [Part::Part2DObjectPython] ShapeString  # Draft 2D object (typed FeaturePython)
  FontFile = <path>
  Placement = pos=(-6.37,-33,-8.65) rot=(1,0,0;1.5708rad)
  Size = 10
  String = +
  Tracking = 0
FEATURE [PartDesign::Pocket] Pocket010
  BaseFeature = -> Pad006
  Length = 0
  Length2 = 100
  Offset = 0.5
  Placement = pos=(0,0,0) rot=(1,0,0;1.5708rad)
  Profile = -> ShapeString
  Type = 3
  UpToFace = -> Pad006 [Face8]
FEATURE [Sketcher::SketchObject] Sketch024
  ExternalGeometry = -> [Pocket010]
  MapMode = 5
  Placement = pos=(0,0,0) rot=(-1,0,0;1.5708rad)
  Support = -> [Pocket010]
  sketch-geometry (7):
    g0: LineSegment StartX=5.3 StartY=-9.17987 StartZ=0 EndX=10.6 EndY=0 EndZ=0
    g1: LineSegment StartX=10.6 StartY=0 StartZ=0 EndX=5.3 EndY=9.17987 EndZ=0
    g2: LineSegment StartX=5.3 StartY=9.17987 StartZ=0 EndX=-5.3 EndY=9.17987 EndZ=0
    g3: LineSegment StartX=-5.3 StartY=9.17987 StartZ=0 EndX=-10.6 EndY=-2.0872e-12 EndZ=0
    g4: LineSegment StartX=-10.6 StartY=-2.0865e-12 StartZ=0 EndX=-5.3 EndY=-9.17987 EndZ=0
    g5: LineSegment StartX=-5.3 StartY=-9.17987 StartZ=0 EndX=5.3 EndY=-9.17987 EndZ=0
    g6: Circle [constr] CenterX=0 CenterY=0 CenterZ=0 NormalX=0 NormalY=0 NormalZ=1 AngleXU=0 Radius=10.6
  constraints (16):
    c: Coincident(g0,g1)
    c: Coincident(g1,g2)
    c: Coincident(g2,g3)
    c: Coincident(g3,g4)
    c: Coincident(g4,g5)
    c: Coincident(g5,g0)
    c: Equal(g0, g1-g5) x5
    c: PointOnObject(g0,g6)
    c: PointOnObject(g1,g6)
    c: PointOnObject(g2,g6)
    c: PointOnObject(g3,g6)
    c: PointOnObject(g4,g6)
    c: PointOnObject(g5,g6)
    c: Coincident(g6,g-1)
    c: DistanceX(g-3,g0) = 1
    c: PointOnObject(g0,g-1)
FEATURE [PartDesign::Pad] Pad007
  BaseFeature = -> Pocket010
  Length = 0.5
  Length2 = 100
  Placement = pos=(0,0,0) rot=(1,0,0;1.5708rad)
  Profile = -> Sketch024
  Type = 0
FEATURE [Sketcher::SketchObject] Sketch025
  MapMode = 5
  Placement = pos=(0,0.5,0) rot=(-1,0,0;1.5708rad)
  Support = -> [Pad007]
  sketch-geometry (1):
    g0: Circle CenterX=0 CenterY=0 CenterZ=0 NormalX=0 NormalY=0 NormalZ=1 AngleXU=0 Radius=5
  constraints (2):
    c: Coincident(g0,g-1)
    c: Radius(g0) = 5
FEATURE [PartDesign::Pad] Pad008
  BaseFeature = -> Pad007
  Length = 2.5
  Length2 = 100
  Placement = pos=(0,0,0) rot=(1,0,0;1.5708rad)
  Profile = -> Sketch025
  Type = 0
FEATURE [PartDesign::Body] Body004  label="Plus button"
  Group = -> [Sketch023,Pad006,Pocket010,Sketch024,Pad007,Sketch025,Pad008]
  Origin = -> Origin012
  Placement = pos=(30,-28.5,-2) rot=(0,0,1;0rad)
  Tip = -> Pad008
FEATURE [Sketcher::SketchObject] Sketch026
  MapMode = 5
  Placement = pos=(0,0,0) rot=(1,0,0;1.5708rad)
  Support = -> [XZ_Plane013]
  sketch-geometry (8):
    g0: LineSegment StartX=-9.6 StartY=-5e-16 StartZ=0 EndX=-4.8 EndY=-8.31384 EndZ=0
    g1: LineSegment StartX=-4.8 StartY=-8.31384 StartZ=0 EndX=4.8 EndY=-8.31384 EndZ=0
    g2: LineSegment StartX=4.8 StartY=-8.31384 StartZ=0 EndX=9.6 EndY=0 EndZ=0
    g3: LineSegment StartX=9.6 StartY=-5e-16 StartZ=0 EndX=4.8 EndY=8.31384 EndZ=0
    g4: LineSegment StartX=4.8 StartY=8.31384 StartZ=0 EndX=-4.8 EndY=8.31384 EndZ=0
    g5: LineSegment StartX=-4.8 StartY=8.31384 StartZ=0 EndX=-9.6 EndY=0 EndZ=0
    g6: Circle [constr] CenterX=0 CenterY=0 CenterZ=0 NormalX=0 NormalY=0 NormalZ=1 AngleXU=0 Radius=9.6
    g7: LineSegment [constr] StartX=-9.6 StartY=-5e-16 StartZ=0 EndX=9.6 EndY=-5e-16 EndZ=0
  constraints (18):
    c: Coincident(g0,g1)
    c: Coincident(g1,g2)
    c: Coincident(g2,g3)
    c: Coincident(g3,g4)
    c: Coincident(g4,g5)
    c: Coincident(g5,g0)
    c: Equal(g0, g1-g5) x5
    c: PointOnObject(g0,g6)
    c: PointOnObject(g1,g6)
    c: PointOnObject(g2,g6)
    c: PointOnObject(g3,g6)
    c: PointOnObject(g4,g6)
    c: PointOnObject(g5,g6)
    c: Radius(g6) = 9.6
    c: Coincident(g7,g0)
    c: Coincident(g7,g2)
    c: Horizontal(g7)
    c: Coincident(g6,g-1)
FEATURE [PartDesign::Pad] Pad009
  Length = 4
  Length2 = 100
  Placement = pos=(0,0,0) rot=(1,0,0;1.5708rad)
  Profile = -> Sketch026
  Type = 0
FEATURE [Part::Part2DObjectPython] ShapeString001  # Draft 2D object (typed FeaturePython)
  FontFile = <path>
  Placement = pos=(-5.15,-33,-7.9) rot=(1,0,0;1.5708rad)
  Size = 10
  String = -
  Tracking = 0
FEATURE [PartDesign::Pocket] Pocket011
  BaseFeature = -> Pad009
  Length = 0
  Length2 = 100
  Offset = 0.5
  Placement = pos=(0,0,0) rot=(1,0,0;1.5708rad)
  Profile = -> ShapeString001
  Type = 3
  UpToFace = -> Pad009 [Face8]
FEATURE [Sketcher::SketchObject] Sketch027
  ExternalGeometry = -> [Pocket011]
  MapMode = 5
  Placement = pos=(0,0,0) rot=(-1,0,0;1.5708rad)
  Support = -> [Pocket011]
  sketch-geometry (7):
    g0: LineSegment StartX=5.3 StartY=-9.17987 StartZ=0 EndX=10.6 EndY=0 EndZ=0
    g1: LineSegment StartX=10.6 StartY=0 StartZ=0 EndX=5.3 EndY=9.17987 EndZ=0
    g2: LineSegment StartX=5.3 StartY=9.17987 StartZ=0 EndX=-5.3 EndY=9.17987 EndZ=0
    g3: LineSegment StartX=-5.3 StartY=9.17987 StartZ=0 EndX=-10.6 EndY=-2.0854e-12 EndZ=0
    g4: LineSegment StartX=-10.6 StartY=-2.0855e-12 StartZ=0 EndX=-5.3 EndY=-9.17987 EndZ=0
    g5: LineSegment StartX=-5.3 StartY=-9.17987 StartZ=0 EndX=5.3 EndY=-9.17987 EndZ=0
    g6: Circle [constr] CenterX=0 CenterY=0 CenterZ=0 NormalX=0 NormalY=0 NormalZ=1 AngleXU=0 Radius=10.6
  constraints (16):
    c: Coincident(g0,g1)
    c: Coincident(g1,g2)
    c: Coincident(g2,g3)
    c: Coincident(g3,g4)
    c: Coincident(g4,g5)
    c: Coincident(g5,g0)
    c: Equal(g0, g1-g5) x5
    c: PointOnObject(g0,g6)
    c: PointOnObject(g1,g6)
    c: PointOnObject(g2,g6)
    c: PointOnObject(g3,g6)
    c: PointOnObject(g4,g6)
    c: PointOnObject(g5,g6)
    c: Coincident(g6,g-1)
    c: DistanceX(g-3,g0) = 1
    c: PointOnObject(g0,g-1)
FEATURE [PartDesign::Pad] Pad011
  BaseFeature = -> Pocket011
  Length = 0.5
  Length2 = 100
  Placement = pos=(0,0,0) rot=(1,0,0;1.5708rad)
  Profile = -> Sketch027
  Type = 0
FEATURE [Sketcher::SketchObject] Sketch028
  MapMode = 5
  Placement = pos=(0,0.5,0) rot=(-1,0,0;1.5708rad)
  Support = -> [Pad011]
  sketch-geometry (1):
    g0: Circle CenterX=0 CenterY=0 CenterZ=0 NormalX=0 NormalY=0 NormalZ=1 AngleXU=0 Radius=5
  constraints (2):
    c: Coincident(g0,g-1)
    c: Radius(g0) = 5
FEATURE [PartDesign::Pad] Pad010
  BaseFeature = -> Pad011
  Length = 2.5
  Length2 = 100
  Placement = pos=(0,0,0) rot=(1,0,0;1.5708rad)
  Profile = -> Sketch028
  Type = 0
FEATURE [PartDesign::Body] Body005  label="Minus button"
  Group = -> [Sketch026,Pad009,Pocket011,Sketch027,Pad011,Sketch028,Pad010]
  Origin = -> Origin013
  Placement = pos=(12,-28.5,-16.35) rot=(0,0,1;0rad)
  Tip = -> Pad010
FEATURE [Part::Part2DObjectPython] ShapeString002  # Draft 2D object (typed FeaturePython)
  FontFile = <path>
  Placement = pos=(-4.25,-33,-5.1) rot=(1,0,0;1.5708rad)
  Size = 6
  String = <
  Tracking = 0
FEATURE [Sketcher::SketchObject] Sketch029
  MapMode = 5
  Placement = pos=(0,0,0) rot=(1,0,0;1.5708rad)
  Support = -> [XZ_Plane014]
  sketch-geometry (8):
    g0: LineSegment StartX=-7.6 StartY=-2e-16 StartZ=0 EndX=-3.8 EndY=-6.58179 EndZ=0
    g1: LineSegment StartX=-3.8 StartY=-6.58179 StartZ=0 EndX=3.8 EndY=-6.58179 EndZ=0
    g2: LineSegment StartX=3.8 StartY=-6.58179 StartZ=0 EndX=7.6 EndY=0 EndZ=0
    g3: LineSegment StartX=7.6 StartY=-2e-16 StartZ=0 EndX=3.8 EndY=6.58179 EndZ=0
    g4: LineSegment StartX=3.8 StartY=6.58179 StartZ=0 EndX=-3.8 EndY=6.58179 EndZ=0
    g5: LineSegment StartX=-3.8 StartY=6.58179 StartZ=0 EndX=-7.6 EndY=0 EndZ=0
    g6: Circle [constr] CenterX=0 CenterY=0 CenterZ=0 NormalX=0 NormalY=0 NormalZ=1 AngleXU=0 Radius=7.6
    g7: LineSegment [constr] StartX=-7.6 StartY=-2e-16 StartZ=0 EndX=7.6 EndY=-2e-16 EndZ=0
  constraints (18):
    c: Coincident(g0,g1)
    c: Coincident(g1,g2)
    c: Coincident(g2,g3)
    c: Coincident(g3,g4)
    c: Coincident(g4,g5)
    c: Coincident(g5,g0)
    c: Equal(g0, g1-g5) x5
    c: PointOnObject(g0,g6)
    c: PointOnObject(g1,g6)
    c: PointOnObject(g2,g6)
    c: PointOnObject(g3,g6)
    c: PointOnObject(g4,g6)
    c: PointOnObject(g5,g6)
    c: Radius(g6) = 7.6
    c: Coincident(g7,g0)
    c: Coincident(g7,g2)
    c: Horizontal(g7)
    c: Coincident(g6,g-1)
FEATURE [PartDesign::Pad] Pad014
  Length = 4
  Length2 = 100
  Placement = pos=(0,0,0) rot=(1,0,0;1.5708rad)
  Profile = -> Sketch029
  Type = 0
FEATURE [PartDesign::Pocket] Pocket012
  BaseFeature = -> Pad014
  Length = 0
  Length2 = 100
  Offset = 0.5
  Placement = pos=(0,0,0) rot=(1,0,0;1.5708rad)
  Profile = -> ShapeString002
  Type = 3
  UpToFace = -> Pad014 [Face8]
FEATURE [Sketcher::SketchObject] Sketch030
  ExternalGeometry = -> [Pocket012]
  MapMode = 5
  Placement = pos=(0,0,0) rot=(-1,0,0;1.5708rad)
  Support = -> [Pocket012]
  sketch-geometry (7):
    g0: LineSegment StartX=4.3 StartY=-7.44782 StartZ=0 EndX=8.6 EndY=0 EndZ=0
    g1: LineSegment StartX=8.6 StartY=0 StartZ=0 EndX=4.3 EndY=7.44782 EndZ=0
    g2: LineSegment StartX=4.3 StartY=7.44782 StartZ=0 EndX=-4.3 EndY=7.44782 EndZ=0
    g3: LineSegment StartX=-4.3 StartY=7.44782 StartZ=0 EndX=-8.6 EndY=-3.8884e-12 EndZ=0
    g4: LineSegment StartX=-8.6 StartY=-3.888e-12 StartZ=0 EndX=-4.3 EndY=-7.44782 EndZ=0
    g5: LineSegment StartX=-4.3 StartY=-7.44782 StartZ=0 EndX=4.3 EndY=-7.44782 EndZ=0
    g6: Circle [constr] CenterX=0 CenterY=0 CenterZ=0 NormalX=0 NormalY=0 NormalZ=1 AngleXU=0 Radius=8.6
  constraints (16):
    c: Coincident(g0,g1)
    c: Coincident(g1,g2)
    c: Coincident(g2,g3)
    c: Coincident(g3,g4)
    c: Coincident(g4,g5)
    c: Coincident(g5,g0)
    c: Equal(g0, g1-g5) x5
    c: PointOnObject(g0,g6)
    c: PointOnObject(g1,g6)
    c: PointOnObject(g2,g6)
    c: PointOnObject(g3,g6)
    c: PointOnObject(g4,g6)
    c: PointOnObject(g5,g6)
    c: Coincident(g6,g-1)
    c: DistanceX(g-3,g0) = 1
    c: PointOnObject(g0,g-1)
FEATURE [PartDesign::Pad] Pad012
  BaseFeature = -> Pocket012
  Length = 0.5
  Length2 = 100
  Placement = pos=(0,0,0) rot=(1,0,0;1.5708rad)
  Profile = -> Sketch030
  Type = 0
FEATURE [Sketcher::SketchObject] Sketch031
  MapMode = 5
  Placement = pos=(0,0.5,0) rot=(-1,0,0;1.5708rad)
  Support = -> [Pad012]
  sketch-geometry (1):
    g0: Circle CenterX=0 CenterY=0 CenterZ=0 NormalX=0 NormalY=0 NormalZ=1 AngleXU=0 Radius=5
  constraints (2):
    c: Coincident(g0,g-1)
    c: Radius(g0) = 5
FEATURE [PartDesign::Pad] Pad013
  BaseFeature = -> Pad012
  Length = 2.5
  Length2 = 100
  Placement = pos=(0,0,0) rot=(1,0,0;1.5708rad)
  Profile = -> Sketch031
  Type = 0
FEATURE [PartDesign::Body] Body006  label="Left button"
  Group = -> [Sketch029,Pad014,Pocket012,Sketch030,Pad012,Sketch031,Pad013]
  Origin = -> Origin014
  Placement = pos=(-32,-28.5,-3.3) rot=(0,0,1;0rad)
  Tip = -> Pad013
FEATURE [Part::Part2DObjectPython] ShapeString003  # Draft 2D object (typed FeaturePython)
  FontFile = <path>
  Placement = pos=(-4.25,-33,-5.1) rot=(1,0,0;1.5708rad)
  Size = 6
  String = <
  Tracking = 0
FEATURE [Sketcher::SketchObject] Sketch033
  MapMode = 5
  Placement = pos=(0,0,0) rot=(1,0,0;1.5708rad)
  Support = -> [XZ_Plane015]
  sketch-geometry (8):
    g0: LineSegment StartX=-7.6 StartY=8e-16 StartZ=0 EndX=-3.8 EndY=-6.58179 EndZ=0
    g1: LineSegment StartX=-3.8 StartY=-6.58179 StartZ=0 EndX=3.8 EndY=-6.58179 EndZ=0
    g2: LineSegment StartX=3.8 StartY=-6.58179 StartZ=0 EndX=7.6 EndY=9e-16 EndZ=0
    g3: LineSegment StartX=7.6 StartY=8e-16 StartZ=0 EndX=3.8 EndY=6.58179 EndZ=0
    g4: LineSegment StartX=3.8 StartY=6.58179 StartZ=0 EndX=-3.8 EndY=6.58179 EndZ=0
    g5: LineSegment StartX=-3.8 StartY=6.58179 StartZ=0 EndX=-7.6 EndY=9e-16 EndZ=0
    g6: Circle [constr] CenterX=0 CenterY=0 CenterZ=0 NormalX=0 NormalY=0 NormalZ=1 AngleXU=0 Radius=7.6
    g7: LineSegment [constr] StartX=-7.6 StartY=8e-16 StartZ=0 EndX=7.6 EndY=8e-16 EndZ=0
  constraints (18):
    c: Coincident(g0,g1)
    c: Coincident(g1,g2)
    c: Coincident(g2,g3)
    c: Coincident(g3,g4)
    c: Coincident(g4,g5)
    c: Coincident(g5,g0)
    c: Equal(g0, g1-g5) x5
    c: PointOnObject(g0,g6)
    c: PointOnObject(g1,g6)
    c: PointOnObject(g2,g6)
    c: PointOnObject(g3,g6)
    c: PointOnObject(g4,g6)
    c: PointOnObject(g5,g6)
    c: Radius(g6) = 7.6
    c: Coincident(g7,g0)
    c: Coincident(g7,g2)
    c: Horizontal(g7)
    c: Coincident(g6,g-1)
FEATURE [PartDesign::Pad] Pad015
  Length = 4
  Length2 = 100
  Placement = pos=(0,0,0) rot=(1,0,0;1.5708rad)
  Profile = -> Sketch033
  Type = 0
FEATURE [PartDesign::Pocket] Pocket013
  BaseFeature = -> Pad015
  Length = 0
  Length2 = 100
  Offset = 0.5
  Placement = pos=(0,0,0) rot=(1,0,0;1.5708rad)
  Profile = -> ShapeString003
  Type = 3
  UpToFace = -> Pad015 [Face8]
FEATURE [Sketcher::SketchObject] Sketch034
  ExternalGeometry = -> [Pocket013]
  MapMode = 5
  Placement = pos=(0,0,0) rot=(-1,0,0;1.5708rad)
  Support = -> [Pocket013]
  sketch-geometry (7):
    g0: LineSegment StartX=4.3 StartY=-7.44782 StartZ=0 EndX=8.6 EndY=9e-16 EndZ=0
    g1: LineSegment StartX=8.6 StartY=0 StartZ=0 EndX=4.3 EndY=7.44782 EndZ=0
    g2: LineSegment StartX=4.3 StartY=7.44782 StartZ=0 EndX=-4.3 EndY=7.44782 EndZ=0
    g3: LineSegment StartX=-4.3 StartY=7.44782 StartZ=0 EndX=-8.6 EndY=-3.8876e-12 EndZ=0
    g4: LineSegment StartX=-8.6 StartY=-3.8875e-12 StartZ=0 EndX=-4.3 EndY=-7.44782 EndZ=0
    g5: LineSegment StartX=-4.3 StartY=-7.44782 StartZ=0 EndX=4.3 EndY=-7.44782 EndZ=0
    g6: Circle [constr] CenterX=0 CenterY=0 CenterZ=0 NormalX=0 NormalY=0 NormalZ=1 AngleXU=0 Radius=8.6
  constraints (16):
    c: Coincident(g0,g1)
    c: Coincident(g1,g2)
    c: Coincident(g2,g3)
    c: Coincident(g3,g4)
    c: Coincident(g4,g5)
    c: Coincident(g5,g0)
    c: Equal(g0, g1-g5) x5
    c: PointOnObject(g0,g6)
    c: PointOnObject(g1,g6)
    c: PointOnObject(g2,g6)
    c: PointOnObject(g3,g6)
    c: PointOnObject(g4,g6)
    c: PointOnObject(g5,g6)
    c: Coincident(g6,g-1)
    c: DistanceX(g-3,g0) = 1
    c: PointOnObject(g0,g-1)
FEATURE [PartDesign::Pad] Pad017
  BaseFeature = -> Pocket013
  Length = 0.5
  Length2 = 100
  Placement = pos=(0,0,0) rot=(1,0,0;1.5708rad)
  Profile = -> Sketch034
  Type = 0
FEATURE [Sketcher::SketchObject] Sketch032
  MapMode = 5
  Placement = pos=(0,0.5,0) rot=(-1,0,0;1.5708rad)
  Support = -> [Pad017]
  sketch-geometry (1):
    g0: Circle CenterX=0 CenterY=0 CenterZ=0 NormalX=0 NormalY=0 NormalZ=1 AngleXU=0 Radius=5
  constraints (2):
    c: Coincident(g0,g-1)
    c: Radius(g0) = 5
FEATURE [PartDesign::Pad] Pad016
  BaseFeature = -> Pad017
  Length = 2.5
  Length2 = 100
  Placement = pos=(0,0,0) rot=(1,0,0;1.5708rad)
  Profile = -> Sketch032
  Type = 0
FEATURE [PartDesign::Body] Body007  label="Right button"
  Group = -> [Sketch033,Pad015,Pocket013,Sketch034,Pad017,Sketch032,Pad016]
  Origin = -> Origin015
  Placement = pos=(-16,-28.5,-13.2) rot=(0,1,0;3.14159rad)
  Tip = -> Pad016
FEATURE [Part::Part2DObjectPython] ShapeString004  # Draft 2D object (typed FeaturePython)
  FontFile = <path>
  Placement = pos=(-3.02,-33,-2.6) rot=(1,0,0;1.5708rad)
  Size = 3
  String = M
  Tracking = 0
FEATURE [Sketcher::SketchObject] Sketch036
  MapMode = 5
  Placement = pos=(0,0,0) rot=(1,0,0;1.5708rad)
  Support = -> [XZ_Plane016]
  sketch-geometry (8):
    g0: LineSegment StartX=-7.6 StartY=-2e-16 StartZ=0 EndX=-3.8 EndY=-6.58179 EndZ=0
    g1: LineSegment StartX=-3.8 StartY=-6.58179 StartZ=0 EndX=3.8 EndY=-6.58179 EndZ=0
    g2: LineSegment StartX=3.8 StartY=-6.58179 StartZ=0 EndX=7.6 EndY=0 EndZ=0
    g3: LineSegment StartX=7.6 StartY=-2e-16 StartZ=0 EndX=3.8 EndY=6.58179 EndZ=0
    g4: LineSegment StartX=3.8 StartY=6.58179 StartZ=0 EndX=-3.8 EndY=6.58179 EndZ=0
    g5: LineSegment StartX=-3.8 StartY=6.58179 StartZ=0 EndX=-7.6 EndY=0 EndZ=0
    g6: Circle [constr] CenterX=0 CenterY=0 CenterZ=0 NormalX=0 NormalY=0 NormalZ=1 AngleXU=0 Radius=7.6
    g7: LineSegment [constr] StartX=-7.6 StartY=-2e-16 StartZ=0 EndX=7.6 EndY=-2e-16 EndZ=0
  constraints (18):
    c: Coincident(g0,g1)
    c: Coincident(g1,g2)
    c: Coincident(g2,g3)
    c: Coincident(g3,g4)
    c: Coincident(g4,g5)
    c: Coincident(g5,g0)
    c: Equal(g0, g1-g5) x5
    c: PointOnObject(g0,g6)
    c: PointOnObject(g1,g6)
    c: PointOnObject(g2,g6)
    c: PointOnObject(g3,g6)
    c: PointOnObject(g4,g6)
    c: PointOnObject(g5,g6)
    c: Radius(g6) = 7.6
    c: Coincident(g7,g0)
    c: Coincident(g7,g2)
    c: Horizontal(g7)
    c: Coincident(g6,g-1)
FEATURE [PartDesign::Pad] Pad018
  Length = 4
  Length2 = 100
  Placement = pos=(0,0,0) rot=(1,0,0;1.5708rad)
  Profile = -> Sketch036
  Type = 0
FEATURE [PartDesign::Pocket] Pocket014
  BaseFeature = -> Pad018
  Length = 0
  Length2 = 100
  Offset = 0.5
  Placement = pos=(0,0,0) rot=(1,0,0;1.5708rad)
  Profile = -> ShapeString004
  Type = 3
  UpToFace = -> Pad018 [Face8]
FEATURE [Sketcher::SketchObject] Sketch037
  ExternalGeometry = -> [Pocket014]
  MapMode = 5
  Placement = pos=(0,0,0) rot=(-1,0,0;1.5708rad)
  Support = -> [Pocket014]
  sketch-geometry (7):
    g0: LineSegment StartX=4.3 StartY=-7.44782 StartZ=0 EndX=8.6 EndY=0 EndZ=0
    g1: LineSegment StartX=8.6 StartY=0 StartZ=0 EndX=4.3 EndY=7.44782 EndZ=0
    g2: LineSegment StartX=4.3 StartY=7.44782 StartZ=0 EndX=-4.3 EndY=7.44782 EndZ=0
    g3: LineSegment StartX=-4.3 StartY=7.44782 StartZ=0 EndX=-8.6 EndY=-3.8867e-12 EndZ=0
    g4: LineSegment StartX=-8.6 StartY=-3.8869e-12 StartZ=0 EndX=-4.3 EndY=-7.44782 EndZ=0
    g5: LineSegment StartX=-4.3 StartY=-7.44782 StartZ=0 EndX=4.3 EndY=-7.44782 EndZ=0
    g6: Circle [constr] CenterX=0 CenterY=0 CenterZ=0 NormalX=0 NormalY=0 NormalZ=1 AngleXU=0 Radius=8.6
  constraints (16):
    c: Coincident(g0,g1)
    c: Coincident(g1,g2)
    c: Coincident(g2,g3)
    c: Coincident(g3,g4)
    c: Coincident(g4,g5)
    c: Coincident(g5,g0)
    c: Equal(g0, g1-g5) x5
    c: PointOnObject(g0,g6)
    c: PointOnObject(g1,g6)
    c: PointOnObject(g2,g6)
    c: PointOnObject(g3,g6)
    c: PointOnObject(g4,g6)
    c: PointOnObject(g5,g6)
    c: Coincident(g6,g-1)
    c: DistanceX(g-3,g0) = 1
    c: PointOnObject(g0,g-1)
FEATURE [PartDesign::Pad] Pad020
  BaseFeature = -> Pocket014
  Length = 0.5
  Length2 = 100
  Placement = pos=(0,0,0) rot=(1,0,0;1.5708rad)
  Profile = -> Sketch037
  Type = 0
FEATURE [Sketcher::SketchObject] Sketch035
  MapMode = 5
  Placement = pos=(0,0.5,0) rot=(-1,0,0;1.5708rad)
  Support = -> [Pad020]
  sketch-geometry (1):
    g0: Circle CenterX=0 CenterY=0 CenterZ=0 NormalX=0 NormalY=0 NormalZ=1 AngleXU=0 Radius=5
  constraints (2):
    c: Coincident(g0,g-1)
    c: Radius(g0) = 5
FEATURE [PartDesign::Pad] Pad019
  BaseFeature = -> Pad020
  Length = 2.5
  Length2 = 100
  Placement = pos=(0,0,0) rot=(1,0,0;1.5708rad)
  Profile = -> Sketch035
  Type = 0
FEATURE [PartDesign::Body] Body008  label="Menu button"
  Group = -> [Sketch036,Pad018,Pocket014,Sketch037,Pad020,Sketch035,Pad019]
  Origin = -> Origin016
  Placement = pos=(-32,-28.5,-23.15) rot=(0,0,1;0rad)
  Tip = -> Pad019
FEATURE [Part::Part2DObjectPython] ShapeString005  # Draft 2D object (typed FeaturePython)
  FontFile = <path>
  Placement = pos=(-2.1,-33,-2.75) rot=(1,0,0;1.5708rad)
  Size = 3
  String = B
  Tracking = 0
FEATURE [Sketcher::SketchObject] Sketch038
  MapMode = 5
  Placement = pos=(0,0,0) rot=(1,0,0;1.5708rad)
  Support = -> [XZ_Plane017]
  sketch-geometry (8):
    g0: LineSegment StartX=-7.6 StartY=9e-16 StartZ=0 EndX=-3.8 EndY=-6.58179 EndZ=0
    g1: LineSegment StartX=-3.8 StartY=-6.58179 StartZ=0 EndX=3.8 EndY=-6.58179 EndZ=0
    g2: LineSegment StartX=3.8 StartY=-6.58179 StartZ=0 EndX=7.6 EndY=9e-16 EndZ=0
    g3: LineSegment StartX=7.6 StartY=9e-16 StartZ=0 EndX=3.8 EndY=6.58179 EndZ=0
    g4: LineSegment StartX=3.8 StartY=6.58179 StartZ=0 EndX=-3.8 EndY=6.58179 EndZ=0
    g5: LineSegment StartX=-3.8 StartY=6.58179 StartZ=0 EndX=-7.6 EndY=9e-16 EndZ=0
    g6: Circle [constr] CenterX=0 CenterY=0 CenterZ=0 NormalX=0 NormalY=0 NormalZ=1 AngleXU=0 Radius=7.6
    g7: LineSegment [constr] StartX=-7.6 StartY=9e-16 StartZ=0 EndX=7.6 EndY=9e-16 EndZ=0
  constraints (18):
    c: Coincident(g0,g1)
    c: Coincident(g1,g2)
    c: Coincident(g2,g3)
    c: Coincident(g3,g4)
    c: Coincident(g4,g5)
    c: Coincident(g5,g0)
    c: Equal(g0, g1-g5) x5
    c: PointOnObject(g0,g6)
    c: PointOnObject(g1,g6)
    c: PointOnObject(g2,g6)
    c: PointOnObject(g3,g6)
    c: PointOnObject(g4,g6)
    c: PointOnObject(g5,g6)
    c: Radius(g6) = 7.6
    c: Coincident(g7,g0)
    c: Coincident(g7,g2)
    c: Horizontal(g7)
    c: Coincident(g6,g-1)
FEATURE [PartDesign::Pad] Pad021
  Length = 4
  Length2 = 100
  Placement = pos=(0,0,0) rot=(1,0,0;1.5708rad)
  Profile = -> Sketch038
  Type = 0
FEATURE [PartDesign::Pocket] Pocket015
  BaseFeature = -> Pad021
  Length = 0
  Length2 = 100
  Offset = 0.5
  Placement = pos=(0,0,0) rot=(1,0,0;1.5708rad)
  Profile = -> ShapeString005
  Type = 3
  UpToFace = -> Pad021 [Face8]
FEATURE [Sketcher::SketchObject] Sketch039
  ExternalGeometry = -> [Pocket015]
  MapMode = 5
  Placement = pos=(0,0,0) rot=(-1,0,0;1.5708rad)
  Support = -> [Pocket015]
  sketch-geometry (7):
    g0: LineSegment StartX=4.3 StartY=-7.44782 StartZ=0 EndX=8.6 EndY=0 EndZ=0
    g1: LineSegment StartX=8.6 StartY=0 StartZ=0 EndX=4.3 EndY=7.44782 EndZ=0
    g2: LineSegment StartX=4.3 StartY=7.44782 StartZ=0 EndX=-4.3 EndY=7.44782 EndZ=0
    g3: LineSegment StartX=-4.3 StartY=7.44782 StartZ=0 EndX=-8.6 EndY=-3.8884e-12 EndZ=0
    g4: LineSegment StartX=-8.6 StartY=-3.8886e-12 StartZ=0 EndX=-4.3 EndY=-7.44782 EndZ=0
    g5: LineSegment StartX=-4.3 StartY=-7.44782 StartZ=0 EndX=4.3 EndY=-7.44782 EndZ=0
    g6: Circle [constr] CenterX=0 CenterY=0 CenterZ=0 NormalX=0 NormalY=0 NormalZ=1 AngleXU=0 Radius=8.6
  constraints (16):
    c: Coincident(g0,g1)
    c: Coincident(g1,g2)
    c: Coincident(g2,g3)
    c: Coincident(g3,g4)
    c: Coincident(g4,g5)
    c: Coincident(g5,g0)
    c: Equal(g0, g1-g5) x5
    c: PointOnObject(g0,g6)
    c: PointOnObject(g1,g6)
    c: PointOnObject(g2,g6)
    c: PointOnObject(g3,g6)
    c: PointOnObject(g4,g6)
    c: PointOnObject(g5,g6)
    c: Coincident(g6,g-1)
    c: DistanceX(g-3,g0) = 1
    c: PointOnObject(g0,g-1)
FEATURE [PartDesign::Pad] Pad023
  BaseFeature = -> Pocket015
  Length = 0.5
  Length2 = 100
  Placement = pos=(0,0,0) rot=(1,0,0;1.5708rad)
  Profile = -> Sketch039
  Type = 0
FEATURE [Sketcher::SketchObject] Sketch040
  MapMode = 5
  Placement = pos=(0,0.5,0) rot=(-1,0,0;1.5708rad)
  Support = -> [Pad023]
  sketch-geometry (1):
    g0: Circle CenterX=0 CenterY=0 CenterZ=0 NormalX=0 NormalY=0 NormalZ=1 AngleXU=0 Radius=5
  constraints (2):
    c: Coincident(g0,g-1)
    c: Radius(g0) = 5
FEATURE [PartDesign::Pad] Pad022
  BaseFeature = -> Pad023
  Length = 2.5
  Length2 = 100
  Placement = pos=(0,0,0) rot=(1,0,0;1.5708rad)
  Profile = -> Sketch040
  Type = 0
FEATURE [PartDesign::Body] Body009  label="Boost button"
  Group = -> [Sketch038,Pad021,Pocket015,Sketch039,Pad023,Sketch040,Pad022]
  Origin = -> Origin017
  Placement = pos=(-16,-28.5,-33.05) rot=(0,1,0;0rad)
  Tip = -> Pad022
FEATURE [Sketcher::SketchObject] Sketch041
  MapMode = 5
  Placement = pos=(0,0,0) rot=(1,0,0;1.5708rad)
  Support = -> [XZ_Plane018]
  expr: Constraints[11] = 3.4 / 2
  sketch-geometry (13):
    g0: LineSegment StartX=-18 StartY=17 StartZ=0 EndX=18 EndY=17 EndZ=0
    g1: LineSegment StartX=18 StartY=17 StartZ=0 EndX=18 EndY=-17 EndZ=0
    g2: LineSegment StartX=18 StartY=-17 StartZ=0 EndX=-18 EndY=-17 EndZ=0
    g3: LineSegment StartX=-18 StartY=-17 StartZ=0 EndX=-18 EndY=17 EndZ=0
    g4: Circle CenterX=-15.6 CenterY=14 CenterZ=0 NormalX=0 NormalY=0 NormalZ=1 AngleXU=0 Radius=1.7
    g5: Circle CenterX=15.6 CenterY=14 CenterZ=0 NormalX=0 NormalY=0 NormalZ=1 AngleXU=0 Radius=1.7
    g6: Circle CenterX=-15.6 CenterY=-14.8 CenterZ=0 NormalX=0 NormalY=0 NormalZ=1 AngleXU=0 Radius=1.7
    g7: Circle CenterX=15.6 CenterY=-14.8 CenterZ=0 NormalX=0 NormalY=0 NormalZ=1 AngleXU=0 Radius=1.7
    g8: Circle CenterX=-3.4 CenterY=15.2 CenterZ=0 NormalX=0 NormalY=0 NormalZ=1 AngleXU=0 Radius=0.5
    g9: Circle CenterX=-0.86 CenterY=15.2 CenterZ=0 NormalX=0 NormalY=0 NormalZ=1 AngleXU=0 Radius=0.5
    g10: Circle CenterX=1.68 CenterY=15.2 CenterZ=0 NormalX=0 NormalY=0 NormalZ=1 AngleXU=0 Radius=0.5
    g11: Circle CenterX=4.22 CenterY=15.2 CenterZ=0 NormalX=0 NormalY=0 NormalZ=1 AngleXU=0 Radius=0.5
    g12: LineSegment [constr] StartX=-3.4 StartY=15.2 StartZ=0 EndX=4.22 EndY=15.2 EndZ=0
  constraints (37):
    c: Coincident(g0,g1)
    c: Coincident(g1,g2)
    c: Coincident(g2,g3)
    c: Coincident(g3,g0)
    c: Horizontal(g0)
    c: Horizontal(g2)
    c: Vertical(g1)
    c: Vertical(g3)
    c: Symmetric(g0,g1,g-1)
    c: DistanceX(g0,g0) = 36
    c: DistanceY(g1,g1) = 34
    c: Radius(g4) = 1.7
    c: Equal(g4,g5)
    c: Equal(g5,g6)
    c: Equal(g6,g7)
    c: DistanceX(g0,g4) = 2.4
    c: DistanceY(g4,g0) = 3
    c: DistanceX(g5,g0) = 2.4
    c: DistanceY(g5,g0) = 3
    c: DistanceX(g2,g6) = 2.4
    c: DistanceY(g6,g0) = 31.8
    c: DistanceY(g7,g0) = 31.8
    c: DistanceX(g7,g1) = 2.4
    c: Horizontal(g12)
    c: PointOnObject(g9,g12)
    c: PointOnObject(g10,g12)
    c: DistanceX(g8,g9) = 2.54
    c: DistanceX(g9,g10) = 2.54
    c: DistanceX(g10,g11) = 2.54
    c: DistanceX(g0,g8) = 14.6
    c: DistanceY(g8,g0) = 1.8
    c: Radius(g8) = 0.5
    c: Equal(g8,g9)
    c: Equal(g9,g10)
    c: Equal(g10,g11)
    c: Coincident(g12,g8)
    c: Coincident(g11,g12)
FEATURE [PartDesign::Pad] Pad024
  Length = 1.2
  Length2 = 100
  Placement = pos=(0,0,0) rot=(1,0,0;1.5708rad)
  Profile = -> Sketch041
  Type = 0
FEATURE [Sketcher::SketchObject] Sketch042
  ExternalGeometry = -> [Pad024]
  MapMode = 5
  Placement = pos=(0,-1.2,1e-15) rot=(1,0,0;1.5708rad)
  Support = -> [Pad024]
  expr: Constraints[11] = 14.2 / 2
  sketch-geometry (4):
    g0: LineSegment StartX=-7.1 StartY=-15.3 StartZ=0 EndX=7.1 EndY=-15.3 EndZ=0
    g1: LineSegment StartX=7.1 StartY=-15.3 StartZ=0 EndX=7.1 EndY=-17 EndZ=0
    g2: LineSegment StartX=7.1 StartY=-17 StartZ=0 EndX=-7.1 EndY=-17 EndZ=0
    g3: LineSegment StartX=-7.1 StartY=-17 StartZ=0 EndX=-7.1 EndY=-15.3 EndZ=0
  constraints (12):
    c: Coincident(g0,g1)
    c: Coincident(g1,g2)
    c: Coincident(g2,g3)
    c: Coincident(g3,g0)
    c: Horizontal(g0)
    c: Horizontal(g2)
    c: Vertical(g1)
    c: Vertical(g3)
    c: DistanceX(g0,g0) = 14.2
    c: DistanceY(g1,g1) = 1.7
    c: PointOnObject(g2,g-3)
    c: DistanceX(g0,g-1) = 7.1
FEATURE [PartDesign::Pocket] Pocket016
  BaseFeature = -> Pad024
  Length = 5
  Length2 = 100
  Placement = pos=(0,0,0) rot=(1,0,0;1.5708rad)
  Profile = -> Sketch042
  Type = 1
FEATURE [Sketcher::SketchObject] Sketch043
  ExternalGeometry = -> [Pocket016]
  MapMode = 5
  Placement = pos=(0,-1.2,5e-16) rot=(1,0,0;1.5708rad)
  Support = -> [Pocket016]
  expr: Constraints[11] = 34.6 / 2
  sketch-geometry (4):
    g0: LineSegment StartX=-17.3 StartY=10.85 StartZ=0 EndX=17.3 EndY=10.85 EndZ=0
    g1: LineSegment StartX=17.3 StartY=10.85 StartZ=0 EndX=17.3 EndY=-9.15 EndZ=0
    g2: LineSegment StartX=17.3 StartY=-9.15 StartZ=0 EndX=-17.3 EndY=-9.15 EndZ=0
    g3: LineSegment StartX=-17.3 StartY=-9.15 StartZ=0 EndX=-17.3 EndY=10.85 EndZ=0
  constraints (12):
    c: Coincident(g0,g1)
    c: Coincident(g1,g2)
    c: Coincident(g2,g3)
    c: Coincident(g3,g0)
    c: Horizontal(g0)
    c: Horizontal(g2)
    c: Vertical(g1)
    c: Vertical(g3)
    c: DistanceX(g0,g0) = 34.6
    c: DistanceY(g1,g1) = 20
    c: DistanceY(g0,g-3) = 6.15
    c: DistanceX(g0,g-1) = 17.3
FEATURE [PartDesign::Pad] Pad025
  BaseFeature = -> Pocket016
  Length = 2
  Length2 = 100
  Placement = pos=(0,0,0) rot=(1,0,0;1.5708rad)
  Profile = -> Sketch043
  Type = 0
FEATURE [Sketcher::SketchObject] Sketch044
  ExternalGeometry = -> [Pad025]
  MapMode = 5
  Placement = pos=(0,-1.4e-14,-9.15) rot=(1,0,0;3.14159rad)
  Support = -> [Pad025]
  sketch-geometry (4):
    g0: LineSegment StartX=-17.3 StartY=3.2 StartZ=0 EndX=17.3 EndY=3.2 EndZ=0
    g1: LineSegment StartX=17.3 StartY=3.2 StartZ=0 EndX=17.3 EndY=2.5 EndZ=0
    g2: LineSegment StartX=17.3 StartY=2.5 StartZ=0 EndX=-17.3 EndY=2.5 EndZ=0
    g3: LineSegment StartX=-17.3 StartY=2.5 StartZ=0 EndX=-17.3 EndY=3.2 EndZ=0
  constraints (10):
    c: Coincident(g0,g1)
    c: Coincident(g1,g2)
    c: Coincident(g2,g3)
    c: Coincident(g3,g0)
    c: Horizontal(g2)
    c: Vertical(g1)
    c: Vertical(g3)
    c: Coincident(g0,g-3)
    c: Coincident(g0,g-3)
    c: DistanceY(g1,g1) = 0.7
FEATURE [PartDesign::Pad] Pad026
  BaseFeature = -> Pad025
  Length = 3.7
  Length2 = 100
  Placement = pos=(0,0,0) rot=(1,0,0;1.5708rad)
  Profile = -> Sketch044
  Type = 0
FEATURE [PartDesign::Body] Body010  label="Display dummy"
  Group = -> [Sketch041,Pad024,Sketch042,Pocket016,Sketch043,Pad025,Sketch044,Pad026]
  Origin = -> Origin018
  Placement = pos=(-4.3,-23.78,22.9) rot=(0,0,1;0rad)
  Tip = -> Pad026
FEATURE [Sketcher::SketchObject] Sketch045
  MapMode = 5
  Placement = pos=(0,0,0) rot=(1,0,0;1.5708rad)
  Support = -> [XZ_Plane019]
  sketch-geometry (8):
    g0: LineSegment StartX=47 StartY=60 StartZ=0 EndX=-47 EndY=60 EndZ=0
    g1: LineSegment StartX=-60 StartY=47 StartZ=0 EndX=-60 EndY=-47 EndZ=0
    g2: LineSegment StartX=-47 StartY=-60 StartZ=0 EndX=47 EndY=-60 EndZ=0
    g3: LineSegment StartX=60 StartY=-47 StartZ=0 EndX=60 EndY=47 EndZ=0
    g4: ArcOfCircle CenterX=-47 CenterY=47 CenterZ=0 NormalX=0 NormalY=0 NormalZ=1 AngleXU=0 Radius=13 StartAngle=1.5708 EndAngle=3.14159
    g5: ArcOfCircle CenterX=47 CenterY=47 CenterZ=0 NormalX=0 NormalY=0 NormalZ=1 AngleXU=0 Radius=13 StartAngle=9.63649e-11 EndAngle=1.5708
    g6: ArcOfCircle CenterX=-47 CenterY=-47 CenterZ=0 NormalX=0 NormalY=0 NormalZ=1 AngleXU=0 Radius=13 StartAngle=3.14159 EndAngle=4.71239
    g7: ArcOfCircle CenterX=47 CenterY=-47 CenterZ=0 NormalX=0 NormalY=0 NormalZ=1 AngleXU=0 Radius=13 StartAngle=4.71239 EndAngle=6.28319
  constraints (19):
    c: Horizontal(g0)
    c: Horizontal(g2)
    c: Vertical(g1)
    c: Vertical(g3)
    c: Equal(g0,g3)
    c: Tangent(g0,g4) = -1.5708
    c: Tangent(g1,g4) = -1.5708
    c: Tangent(g0,g5) = -1.5708
    c: Tangent(g3,g5) = -1.5708
    c: Tangent(g1,g6) = -1.5708
    c: Tangent(g2,g6) = -1.5708
    c: Tangent(g2,g7) = -1.5708
    c: Tangent(g3,g7) = -1.5708
    c: Radius(g4) = 13
    c: Equal(g4,g6)
    c: Equal(g6,g7)
    c: Equal(g7,g5)
    c: Symmetric(g1,g3,g-1)
    c: DistanceY(g2,g0) = 120
FEATURE [PartDesign::Pad] Pad027
  Length = 2.5
  Length2 = 100
  Placement = pos=(0,0,0) rot=(1,0,0;1.5708rad)
  Profile = -> Sketch045
  Reversed = true
  Type = 0
FEATURE [Sketcher::SketchObject] Sketch046  label="Tongues"
  ExternalGeometry = -> [Pad027]
  MapMode = 5
  Placement = pos=(0,0,0) rot=(1,0,0;1.5708rad)
  Support = -> [Pad027]
  sketch-geometry (16):
    g0: LineSegment StartX=-44 StartY=57.95 StartZ=0 EndX=44 EndY=57.95 EndZ=0
    g1: LineSegment StartX=44 StartY=57.95 StartZ=0 EndX=44 EndY=55.95 EndZ=0
    g2: LineSegment StartX=44 StartY=55.95 StartZ=0 EndX=-44 EndY=55.95 EndZ=0
    g3: LineSegment StartX=-44 StartY=55.95 StartZ=0 EndX=-44 EndY=57.95 EndZ=0
    g4: LineSegment StartX=-44 StartY=-55.95 StartZ=0 EndX=44 EndY=-55.95 EndZ=0
    g5: LineSegment StartX=44 StartY=-55.95 StartZ=0 EndX=44 EndY=-57.95 EndZ=0
    g6: LineSegment StartX=44 StartY=-57.95 StartZ=0 EndX=-44 EndY=-57.95 EndZ=0
    g7: LineSegment StartX=-44 StartY=-57.95 StartZ=0 EndX=-44 EndY=-55.95 EndZ=0
    g8: LineSegment StartX=57.95 StartY=44 StartZ=0 EndX=55.95 EndY=44 EndZ=0
    g9: LineSegment StartX=55.95 StartY=44 StartZ=0 EndX=55.95 EndY=-44 EndZ=0
    g10: LineSegment StartX=55.95 StartY=-44 StartZ=0 EndX=57.95 EndY=-44 EndZ=0
    g11: LineSegment StartX=57.95 StartY=-44 StartZ=0 EndX=57.95 EndY=44 EndZ=0
    g12: LineSegment StartX=-57.95 StartY=44 StartZ=0 EndX=-55.95 EndY=44 EndZ=0
    g13: LineSegment StartX=-55.95 StartY=44 StartZ=0 EndX=-55.95 EndY=-44 EndZ=0
    g14: LineSegment StartX=-55.95 StartY=-44 StartZ=0 EndX=-57.95 EndY=-44 EndZ=0
    g15: LineSegment StartX=-57.95 StartY=-44 StartZ=0 EndX=-57.95 EndY=44 EndZ=0
  constraints (48):
    c: Coincident(g0,g1)
    c: Coincident(g1,g2)
    c: Coincident(g2,g3)
    c: Coincident(g3,g0)
    c: Horizontal(g0)
    c: Horizontal(g2)
    c: Vertical(g1)
    c: Vertical(g3)
    c: Coincident(g4,g5)
    c: Coincident(g5,g6)
    c: Coincident(g6,g7)
    c: Coincident(g7,g4)
    c: Horizontal(g4)
    c: Horizontal(g6)
    c: Vertical(g5)
    c: Vertical(g7)
    c: Coincident(g8,g9)
    c: Coincident(g9,g10)
    c: Coincident(g10,g11)
    c: Coincident(g11,g8)
    c: Horizontal(g8)
    c: Horizontal(g10)
    c: Vertical(g9)
    c: Vertical(g11)
    c: Coincident(g12,g13)
    c: Coincident(g13,g14)
    c: Coincident(g14,g15)
    c: Coincident(g15,g12)
    c: Horizontal(g12)
    c: Horizontal(g14)
    c: Vertical(g13)
    c: Vertical(g15)
    c: DistanceX(g-3,g0) = 3
    c: DistanceX(g0,g-3) = 3
    c: DistanceY(g0,g-3) = 2.05
    c: DistanceY(g3,g3) = 2
    c: DistanceX(g12,g12) = 2
    c: DistanceY(g12,g-4) = 3
    c: DistanceY(g-4,g14) = 3
    c: DistanceX(g-4,g12) = 2.05
    c: DistanceY(g7,g7) = 2
    c: DistanceX(g-6,g6) = 3
    c: DistanceX(g5,g-6) = 3
    c: DistanceY(g-6,g6) = 2.05
    c: DistanceX(g8,g8) = 2
    c: DistanceY(g8,g-5) = 3
    c: DistanceX(g8,g-5) = 2.05
    c: DistanceY(g10,g-5) = -3
FEATURE [PartDesign::Pad] Pad028
  BaseFeature = -> Pad027
  Length = 3
  Length2 = 100
  Placement = pos=(0,0,0) rot=(1,0,0;1.5708rad)
  Profile = -> Sketch046
  Type = 0
FEATURE [Sketcher::SketchObject] Sketch047
  ExternalGeometry = -> [Pad028]
  MapMode = 5
  Placement = pos=(0,-3,2e-15) rot=(1,0,0;1.5708rad)
  Support = -> [Pad028]
  sketch-geometry (4):
    g0: LineSegment StartX=-44 StartY=57.95 StartZ=0 EndX=44 EndY=57.95 EndZ=0
    g1: LineSegment StartX=44 StartY=57.95 StartZ=0 EndX=44 EndY=55.95 EndZ=0
    g2: LineSegment StartX=44 StartY=55.95 StartZ=0 EndX=-44 EndY=55.95 EndZ=0
    g3: LineSegment StartX=-44 StartY=55.95 StartZ=0 EndX=-44 EndY=57.95 EndZ=0
  constraints (10):
    c: Coincident(g0,g1)
    c: Coincident(g1,g2)
    c: Coincident(g2,g3)
    c: Coincident(g3,g0)
    c: Horizontal(g0)
    c: Horizontal(g2)
    c: Vertical(g1)
    c: Vertical(g3)
    c: Coincident(g0,g-3)
    c: Coincident(g1,g-4)
FEATURE [PartDesign::Pad] Pad029
  BaseFeature = -> Pad028
  Length = 4
  Length2 = 100
  Placement = pos=(0,0,0) rot=(1,0,0;1.5708rad)
  Profile = -> Sketch047
  Type = 0
FEATURE [Sketcher::SketchObject] Sketch048
  ExternalGeometry = -> [Pad029]
  MapMode = 5
  Placement = pos=(0,3.2e-14,57.95) rot=(0,0,1;3.14159rad)
  Support = -> [Pad029]
  sketch-geometry (8):
    g0: LineSegment StartX=-30 StartY=5.05 StartZ=0 EndX=-10 EndY=5.05 EndZ=0
    g1: LineSegment StartX=-10 StartY=5.05 StartZ=0 EndX=-10 EndY=3 EndZ=0
    g2: LineSegment StartX=-10 StartY=3 StartZ=0 EndX=-30 EndY=3 EndZ=0
    g3: LineSegment StartX=-30 StartY=3 StartZ=0 EndX=-30 EndY=5.05 EndZ=0
    g4: LineSegment StartX=10 StartY=5.05 StartZ=0 EndX=30 EndY=5.05 EndZ=0
    g5: LineSegment StartX=30 StartY=5.05 StartZ=0 EndX=30 EndY=3 EndZ=0
    g6: LineSegment StartX=30 StartY=3 StartZ=0 EndX=10 EndY=3 EndZ=0
    g7: LineSegment StartX=10 StartY=3 StartZ=0 EndX=10 EndY=5.05 EndZ=0
  constraints (25):
    c: Coincident(g0,g1)
    c: Coincident(g1,g2)
    c: Coincident(g2,g3)
    c: Coincident(g3,g0)
    c: Horizontal(g0)
    c: Horizontal(g2)
    c: Vertical(g1)
    c: Vertical(g3)
    c: PointOnObject(g1,g-3)
    c: Coincident(g4,g5)
    c: Coincident(g5,g6)
    c: Coincident(g6,g7)
    c: Coincident(g7,g4)
    c: Horizontal(g4)
    c: Horizontal(g6)
    c: Vertical(g5)
    c: Vertical(g7)
    c: PointOnObject(g5,g-3)
    c: Equal(g0,g4)
    c: DistanceX(g0,g0) = 20
    c: DistanceX(g1,g-1) = 10
    c: DistanceX(g-1,g6) = 10
    c: DistanceY(g3,g3) = 2.05
    c: Equal(g3,g7)
    c: DistanceY(g-1,g1) = 3
FEATURE [PartDesign::Pocket] Pocket017  label="Top latches"
  BaseFeature = -> Pad029
  Length = 2
  Length2 = 100
  Placement = pos=(0,0,0) rot=(1,0,0;1.5708rad)
  Profile = -> Sketch048
  Type = 0
FEATURE [Sketcher::SketchObject] Sketch049
  ExternalGeometry = -> [Pocket017]
  MapMode = 5
  Placement = pos=(0,-3,2e-15) rot=(1,0,0;1.5708rad)
  Support = -> [Pocket017]
  sketch-geometry (4):
    g0: LineSegment StartX=-10 StartY=-55.95 StartZ=0 EndX=10 EndY=-55.95 EndZ=0
    g1: LineSegment StartX=10 StartY=-55.95 StartZ=0 EndX=10 EndY=-57.95 EndZ=0
    g2: LineSegment StartX=10 StartY=-57.95 StartZ=0 EndX=-10 EndY=-57.95 EndZ=0
    g3: LineSegment StartX=-10 StartY=-57.95 StartZ=0 EndX=-10 EndY=-55.95 EndZ=0
  constraints (12):
    c: Coincident(g0,g1)
    c: Coincident(g1,g2)
    c: Coincident(g2,g3)
    c: Coincident(g3,g0)
    c: Horizontal(g0)
    c: Horizontal(g2)
    c: Vertical(g1)
    c: Vertical(g3)
    c: PointOnObject(g0,g-3)
    c: PointOnObject(g1,g-4)
    c: DistanceX(g0,g0) = 20
    c: DistanceX(g0,g-1) = 10
FEATURE [PartDesign::Pad] Pad030
  BaseFeature = -> Pocket017
  Length = 6
  Length2 = 100
  Placement = pos=(0,0,0) rot=(1,0,0;1.5708rad)
  Profile = -> Sketch049
  Type = 0
FEATURE [PartDesign::Fillet] Fillet002
  Base = -> Pad030 [Edge117,Edge118]
  BaseFeature = -> Pad030
  Placement = pos=(0,0,0) rot=(1,0,0;1.5708rad)
  Radius = 5
FEATURE [Sketcher::SketchObject] Sketch050  label="Backplate bottom screw hole"
  MapMode = 5
  Placement = pos=(0,-4.82e-14,-57.95) rot=(1,0,0;3.14159rad)
  Support = -> [Fillet002]
  sketch-geometry (1):
    g0: Circle CenterX=0 CenterY=5.5 CenterZ=0 NormalX=0 NormalY=0 NormalZ=1 AngleXU=0 Radius=1
  constraints (3):
    c: PointOnObject(g0,g-2)
    c: DistanceY(g-1,g0) = 5.5
    c: Radius(g0) = 1
FEATURE [Sketcher::SketchObject] Sketch052
  MapMode = 5
  Placement = pos=(0,-1.33e-14,-60) rot=(1,0,0;3.14159rad)
  Support = -> [Pocket009]
  sketch-geometry (1):
    g0: Circle CenterX=0 CenterY=5.5 CenterZ=0 NormalX=0 NormalY=0 NormalZ=1 AngleXU=0 Radius=1.3
  constraints (3):
    c: PointOnObject(g0,g-2)
    c: DistanceY(g-1,g0) = 5.5
    c: Radius(g0) = 1.3
FEATURE [PartDesign::Pocket] Pocket019  label="Bottom screw hole"
  BaseFeature = -> Pocket009
  Length = 2
  Length2 = 100
  Placement = pos=(0,0,0) rot=(1,0,0;1.5708rad)
  Profile = -> Sketch052
  Type = 0
FEATURE [Sketcher::SketchObject] Sketch053
  ExternalGeometry = -> [Pocket019]
  MapMode = 5
  Placement = pos=(0,-1.33e-14,-60) rot=(1,0,0;3.14159rad)
  Support = -> [Pocket019]
  sketch-geometry (1):
    g0: Circle CenterX=0 CenterY=5.5 CenterZ=0 NormalX=0 NormalY=0 NormalZ=1 AngleXU=0 Radius=3
  constraints (2):
    c: Coincident(g0,g-3)
    c: Radius(g0) = 3
FEATURE [PartDesign::Pocket] Pocket020  label="Bottom screw hollow"
  BaseFeature = -> Pocket019
  Length = 1
  Length2 = 100
  Placement = pos=(0,0,0) rot=(1,0,0;1.5708rad)
  Profile = -> Sketch053
  Type = 0
FEATURE [Sketcher::SketchObject] Sketch054
  ExternalGeometry = -> [Pocket020]
  MapMode = 5
  Placement = pos=(0,-1.33e-14,-60) rot=(1,0,0;3.14159rad)
  Support = -> [Pocket020]
  sketch-geometry (2):
    g0: Circle CenterX=0 CenterY=5.5 CenterZ=0 NormalX=0 NormalY=0 NormalZ=1 AngleXU=0 Radius=3
    g1: Circle CenterX=0 CenterY=5.5 CenterZ=0 NormalX=0 NormalY=0 NormalZ=1 AngleXU=0 Radius=3.5
  constraints (4):
    c: Coincident(g0,g-3)
    c: Coincident(g1,g0)
    c: Radius(g1) = 3.5
    c: Radius(g0) = 3
FEATURE [PartDesign::Pad] Pad032  label="Bottom screw ring"
  BaseFeature = -> Pocket020
  Length = 1
  Length2 = 100
  Placement = pos=(0,0,0) rot=(1,0,0;1.5708rad)
  Profile = -> Sketch054
  Type = 0
FEATURE [Sketcher::SketchObject] Sketch055
  MapMode = 5
  Placement = pos=(0,1.93e-14,58) rot=(1,0,0;3.14159rad)
  Support = -> [Pad032]
  sketch-geometry (8):
    g0: LineSegment StartX=11 StartY=3 StartZ=0 EndX=29 EndY=3 EndZ=0
    g1: LineSegment StartX=29 StartY=3 StartZ=0 EndX=29 EndY=5 EndZ=0
    g2: LineSegment StartX=29 StartY=5 StartZ=0 EndX=11 EndY=5 EndZ=0
    g3: LineSegment StartX=11 StartY=5 StartZ=0 EndX=11 EndY=3 EndZ=0
    g4: LineSegment StartX=-29 StartY=3 StartZ=0 EndX=-11 EndY=3 EndZ=0
    g5: LineSegment StartX=-11 StartY=3 StartZ=0 EndX=-11 EndY=5 EndZ=0
    g6: LineSegment StartX=-11 StartY=5 StartZ=0 EndX=-29 EndY=5 EndZ=0
    g7: LineSegment StartX=-29 StartY=5 StartZ=0 EndX=-29 EndY=3 EndZ=0
  constraints (24):
    c: Coincident(g0,g1)
    c: Coincident(g1,g2)
    c: Coincident(g2,g3)
    c: Coincident(g3,g0)
    c: Horizontal(g0)
    c: Horizontal(g2)
    c: Vertical(g1)
    c: Vertical(g3)
    c: Coincident(g4,g5)
    c: Coincident(g5,g6)
    c: Coincident(g6,g7)
    c: Coincident(g7,g4)
    c: Horizontal(g4)
    c: Horizontal(g6)
    c: Vertical(g5)
    c: Vertical(g7)
    c: Equal(g5,g3)
    c: DistanceY(g5,g5) = 2
    c: DistanceX(g5,g-1) = 11
    c: DistanceX(g-1,g2) = 11
    c: DistanceY(g-1,g4) = 3
    c: DistanceY(g-1,g0) = 3
    c: Equal(g6,g2)
    c: DistanceX(g6,g6) = 18
FEATURE [PartDesign::Pad] Pad033  label="Top latching tongues"
  BaseFeature = -> Pad032
  Length = 2.5
  Length2 = 100
  Placement = pos=(0,0,0) rot=(1,0,0;1.5708rad)
  Profile = -> Sketch055
  Type = 0
FEATURE [PartDesign::Body] Body003  label="Housing - v4"
  Group = -> [Sketch016,Pad003,Pocket007,Sketch019,Pocket008,Sketch020,Pad004,Sketch021,Pad005,Sketch022,Pocket009,Sketch052,Pocket019,Sketch053,Pocket020,Sketch054,Pad032,Sketch055,Pad033]
  Origin = -> Origin003
  Tip = -> Pad033
FEATURE [Sketcher::SketchObject] Sketch071
  MapMode = 5
  Placement = pos=(0,0,0) rot=(1,0,0;1.5708rad)
  Support = -> [XZ_Plane021]
  sketch-geometry (8):
    g0: LineSegment StartX=37 StartY=50 StartZ=0 EndX=-37 EndY=50 EndZ=0
    g1: LineSegment StartX=-50 StartY=37 StartZ=0 EndX=-50 EndY=-37 EndZ=0
    g2: LineSegment StartX=-37 StartY=-50 StartZ=0 EndX=37 EndY=-50 EndZ=0
    g3: LineSegment StartX=50 StartY=-37 StartZ=0 EndX=50 EndY=37 EndZ=0
    g4: ArcOfCircle CenterX=-37 CenterY=37 CenterZ=0 NormalX=0 NormalY=0 NormalZ=1 AngleXU=0 Radius=13 StartAngle=1.5708 EndAngle=3.14159
    g5: ArcOfCircle CenterX=37 CenterY=37 CenterZ=0 NormalX=0 NormalY=0 NormalZ=1 AngleXU=0 Radius=13 StartAngle=3.33172e-11 EndAngle=1.5708
    g6: ArcOfCircle CenterX=-37 CenterY=-37 CenterZ=0 NormalX=0 NormalY=0 NormalZ=1 AngleXU=0 Radius=13 StartAngle=3.14159 EndAngle=4.71239
    g7: ArcOfCircle CenterX=37 CenterY=-37 CenterZ=0 NormalX=0 NormalY=0 NormalZ=1 AngleXU=0 Radius=13 StartAngle=4.71239 EndAngle=6.28319
  constraints (19):
    c: Horizontal(g0)
    c: Horizontal(g2)
    c: Vertical(g1)
    c: Vertical(g3)
    c: Equal(g0,g3)
    c: Tangent(g0,g4) = -1.5708
    c: Tangent(g1,g4) = -1.5708
    c: Tangent(g0,g5) = -1.5708
    c: Tangent(g3,g5) = -1.5708
    c: Tangent(g1,g6) = -1.5708
    c: Tangent(g2,g6) = -1.5708
    c: Tangent(g2,g7) = -1.5708
    c: Tangent(g3,g7) = -1.5708
    c: Radius(g4) = 13
    c: Equal(g4,g6)
    c: Equal(g6,g7)
    c: Equal(g7,g5)
    c: Symmetric(g1,g3,g-1)
    c: DistanceY(g2,g0) = 100
FEATURE [PartDesign::Pad] Pad042
  Length = 2.5
  Length2 = 100
  Placement = pos=(0,0,0) rot=(1,0,0;1.5708rad)
  Profile = -> Sketch071
  Reversed = true
  Type = 0
FEATURE [Sketcher::SketchObject] Sketch070  label="Tongues001"
  ExternalGeometry = -> [Pad042]
  MapMode = 5
  Placement = pos=(0,0,0) rot=(1,0,0;1.5708rad)
  Support = -> [Pad042]
  sketch-geometry (16):
    g0: LineSegment StartX=-34 StartY=47.95 StartZ=0 EndX=34 EndY=47.95 EndZ=0
    g1: LineSegment StartX=34 StartY=47.95 StartZ=0 EndX=34 EndY=45.95 EndZ=0
    g2: LineSegment StartX=34 StartY=45.95 StartZ=0 EndX=-34 EndY=45.95 EndZ=0
    g3: LineSegment StartX=-34 StartY=45.95 StartZ=0 EndX=-34 EndY=47.95 EndZ=0
    g4: LineSegment StartX=-34 StartY=-45.95 StartZ=0 EndX=34 EndY=-45.95 EndZ=0
    g5: LineSegment StartX=34 StartY=-45.95 StartZ=0 EndX=34 EndY=-47.95 EndZ=0
    g6: LineSegment StartX=34 StartY=-47.95 StartZ=0 EndX=-34 EndY=-47.95 EndZ=0
    g7: LineSegment StartX=-34 StartY=-47.95 StartZ=0 EndX=-34 EndY=-45.95 EndZ=0
    g8: LineSegment StartX=47.95 StartY=34 StartZ=0 EndX=45.95 EndY=34 EndZ=0
    g9: LineSegment StartX=45.95 StartY=34 StartZ=0 EndX=45.95 EndY=-34 EndZ=0
    g10: LineSegment StartX=45.95 StartY=-34 StartZ=0 EndX=47.95 EndY=-34 EndZ=0
    g11: LineSegment StartX=47.95 StartY=-34 StartZ=0 EndX=47.95 EndY=34 EndZ=0
    g12: LineSegment StartX=-47.95 StartY=34 StartZ=0 EndX=-45.95 EndY=34 EndZ=0
    g13: LineSegment StartX=-45.95 StartY=34 StartZ=0 EndX=-45.95 EndY=-34 EndZ=0
    g14: LineSegment StartX=-45.95 StartY=-34 StartZ=0 EndX=-47.95 EndY=-34 EndZ=0
    g15: LineSegment StartX=-47.95 StartY=-34 StartZ=0 EndX=-47.95 EndY=34 EndZ=0
  constraints (48):
    c: Coincident(g0,g1)
    c: Coincident(g1,g2)
    c: Coincident(g2,g3)
    c: Coincident(g3,g0)
    c: Horizontal(g0)
    c: Horizontal(g2)
    c: Vertical(g1)
    c: Vertical(g3)
    c: Coincident(g4,g5)
    c: Coincident(g5,g6)
    c: Coincident(g6,g7)
    c: Coincident(g7,g4)
    c: Horizontal(g4)
    c: Horizontal(g6)
    c: Vertical(g5)
    c: Vertical(g7)
    c: Coincident(g8,g9)
    c: Coincident(g9,g10)
    c: Coincident(g10,g11)
    c: Coincident(g11,g8)
    c: Horizontal(g8)
    c: Horizontal(g10)
    c: Vertical(g9)
    c: Vertical(g11)
    c: Coincident(g12,g13)
    c: Coincident(g13,g14)
    c: Coincident(g14,g15)
    c: Coincident(g15,g12)
    c: Horizontal(g12)
    c: Horizontal(g14)
    c: Vertical(g13)
    c: Vertical(g15)
    c: DistanceX(g-3,g0) = 3
    c: DistanceX(g0,g-3) = 3
    c: DistanceY(g0,g-3) = 2.05
    c: DistanceY(g3,g3) = 2
    c: DistanceX(g12,g12) = 2
    c: DistanceY(g12,g-4) = 3
    c: DistanceY(g-4,g14) = 3
    c: DistanceX(g-4,g12) = 2.05
    c: DistanceY(g7,g7) = 2
    c: DistanceX(g-6,g6) = 3
    c: DistanceX(g5,g-6) = 3
    c: DistanceY(g-6,g6) = 2.05
    c: DistanceX(g8,g8) = 2
    c: DistanceY(g8,g-5) = 3
    c: DistanceX(g8,g-5) = 2.05
    c: DistanceY(g10,g-5) = -3
FEATURE [PartDesign::Pad] Pad039
  BaseFeature = -> Pad042
  Length = 3
  Length2 = 100
  Placement = pos=(0,0,0) rot=(1,0,0;1.5708rad)
  Profile = -> Sketch070
  Type = 0
FEATURE [Sketcher::SketchObject] Sketch069
  ExternalGeometry = -> [Pad039]
  MapMode = 5
  Placement = pos=(0,-3,0) rot=(1,0,0;1.5708rad)
  Support = -> [Pad039]
  sketch-geometry (4):
    g0: LineSegment StartX=-34 StartY=47.95 StartZ=0 EndX=34 EndY=47.95 EndZ=0
    g1: LineSegment StartX=34 StartY=47.95 StartZ=0 EndX=34 EndY=45.95 EndZ=0
    g2: LineSegment StartX=34 StartY=45.95 StartZ=0 EndX=-34 EndY=45.95 EndZ=0
    g3: LineSegment StartX=-34 StartY=45.95 StartZ=0 EndX=-34 EndY=47.95 EndZ=0
  constraints (10):
    c: Coincident(g0,g1)
    c: Coincident(g1,g2)
    c: Coincident(g2,g3)
    c: Coincident(g3,g0)
    c: Horizontal(g0)
    c: Horizontal(g2)
    c: Vertical(g1)
    c: Vertical(g3)
    c: Coincident(g0,g-3)
    c: Coincident(g1,g-4)
FEATURE [PartDesign::Pad] Pad043
  BaseFeature = -> Pad039
  Length = 4
  Length2 = 100
  Placement = pos=(0,0,0) rot=(1,0,0;1.5708rad)
  Profile = -> Sketch069
  Type = 0
FEATURE [Sketcher::SketchObject] Sketch067
  ExternalGeometry = -> [Pad043]
  MapMode = 5
  Placement = pos=(0,1.06e-14,47.95) rot=(0,0,1;3.14159rad)
  Support = -> [Pad043]
  sketch-geometry (8):
    g0: LineSegment StartX=-30 StartY=5.05 StartZ=0 EndX=-10 EndY=5.05 EndZ=0
    g1: LineSegment StartX=-10 StartY=5.05 StartZ=0 EndX=-10 EndY=3 EndZ=0
    g2: LineSegment StartX=-10 StartY=3 StartZ=0 EndX=-30 EndY=3 EndZ=0
    g3: LineSegment StartX=-30 StartY=3 StartZ=0 EndX=-30 EndY=5.05 EndZ=0
    g4: LineSegment StartX=10 StartY=3 StartZ=0 EndX=30 EndY=3 EndZ=0
    g5: LineSegment StartX=30 StartY=3 StartZ=0 EndX=30 EndY=5.05 EndZ=0
    g6: LineSegment StartX=30 StartY=5.05 StartZ=0 EndX=10 EndY=5.05 EndZ=0
    g7: LineSegment StartX=10 StartY=5.05 StartZ=0 EndX=10 EndY=3 EndZ=0
  constraints (25):
    c: Coincident(g0,g1)
    c: Coincident(g1,g2)
    c: Coincident(g2,g3)
    c: Coincident(g3,g0)
    c: Horizontal(g0)
    c: Horizontal(g2)
    c: Vertical(g1)
    c: Vertical(g3)
    c: PointOnObject(g1,g-3)
    c: Coincident(g4,g5)
    c: Coincident(g5,g6)
    c: Coincident(g6,g7)
    c: Coincident(g7,g4)
    c: Horizontal(g4)
    c: Horizontal(g6)
    c: Vertical(g5)
    c: Vertical(g7)
    c: Equal(g0,g4)
    c: DistanceX(g0,g0) = 20
    c: DistanceX(g1,g-1) = 10
    c: DistanceX(g-1,g6) = 10
    c: DistanceY(g3,g3) = 2.05
    c: Equal(g3,g7)
    c: DistanceY(g-1,g1) = 3
    c: PointOnObject(g4,g-3)
FEATURE [PartDesign::Pocket] Pocket026  label="Top latches001"
  BaseFeature = -> Pad043
  Length = 2
  Length2 = 100
  Placement = pos=(0,0,0) rot=(1,0,0;1.5708rad)
  Profile = -> Sketch067
  Type = 0
FEATURE [Sketcher::SketchObject] Sketch072
  ExternalGeometry = -> [Pad039]
  MapMode = 5
  Placement = pos=(0,-3,0) rot=(1,0,0;1.5708rad)
  Support = -> [Pocket026]
  sketch-geometry (4):
    g0: LineSegment StartX=-10 StartY=-45.95 StartZ=0 EndX=10 EndY=-45.95 EndZ=0
    g1: LineSegment StartX=10 StartY=-45.95 StartZ=0 EndX=10 EndY=-47.95 EndZ=0
    g2: LineSegment StartX=10 StartY=-47.95 StartZ=0 EndX=-10 EndY=-47.95 EndZ=0
    g3: LineSegment StartX=-10 StartY=-47.95 StartZ=0 EndX=-10 EndY=-45.95 EndZ=0
  constraints (12):
    c: Coincident(g0,g1)
    c: Coincident(g1,g2)
    c: Coincident(g2,g3)
    c: Coincident(g3,g0)
    c: Horizontal(g0)
    c: Horizontal(g2)
    c: Vertical(g1)
    c: Vertical(g3)
    c: DistanceX(g0,g0) = 20
    c: DistanceX(g0,g-1) = 10
    c: PointOnObject(g0,g-3)
    c: PointOnObject(g1,g-4)
FEATURE [PartDesign::Pad] Pad040
  BaseFeature = -> Pocket026
  Length = 6
  Length2 = 100
  Placement = pos=(0,0,0) rot=(1,0,0;1.5708rad)
  Profile = -> Sketch072
  Type = 0
FEATURE [PartDesign::Fillet] Fillet003
  Base = -> Pad040 [Edge121,Edge122]
  BaseFeature = -> Pad040
  Placement = pos=(0,0,0) rot=(1,0,0;1.5708rad)
  Radius = 5
FEATURE [Sketcher::SketchObject] Sketch073
  MapMode = 5
  Placement = pos=(0,-1.06e-14,-47.95) rot=(1,0,0;3.14159rad)
  Support = -> [Fillet003]
  sketch-geometry (1):
    g0: Circle CenterX=0 CenterY=5.5 CenterZ=0 NormalX=0 NormalY=0 NormalZ=1 AngleXU=0 Radius=1
  constraints (3):
    c: PointOnObject(g0,g-2)
    c: Radius(g0) = 1
    c: DistanceY(g-1,g0) = 5.5
FEATURE [PartDesign::Pocket] Pocket027
  BaseFeature = -> Fillet003
  Length = 2
  Length2 = 100
  Placement = pos=(0,0,0) rot=(1,0,0;1.5708rad)
  Profile = -> Sketch073
  Type = 0
FEATURE [Sketcher::SketchObject] Sketch074
  ExternalGeometry = -> [Pocket027]
  MapMode = 5
  Placement = pos=(0,-1.02e-14,-45.95) rot=(0,0,1;3.14159rad)
  Support = -> [Pocket027]
  sketch-geometry (2):
    g0: Circle CenterX=0 CenterY=5.5 CenterZ=0 NormalX=0 NormalY=0 NormalZ=1 AngleXU=0 Radius=2
    g1: Circle CenterX=0 CenterY=5.5 CenterZ=0 NormalX=0 NormalY=0 NormalZ=1 AngleXU=0 Radius=1
  constraints (4):
    c: Coincident(g0,g-3)
    c: Radius(g0) = 2
    c: Coincident(g1,g0)
    c: Radius(g1) = 1
FEATURE [PartDesign::Pad] Pad044
  BaseFeature = -> Pocket027
  Length = 1
  Length2 = 100
  Placement = pos=(0,0,0) rot=(1,0,0;1.5708rad)
  Profile = -> Sketch074
  Type = 0
FEATURE [Sketcher::SketchObject] Sketch061  label="FaceplateSketch"
  MapMode = 5
  Placement = pos=(0,0,0) rot=(1,0,0;1.5708rad)
  Support = -> [XZ_Plane020]
  sketch-geometry (54):
    g0: LineSegment StartX=-28 StartY=-10.2154 StartZ=0 EndX=-24 EndY=-3.28719 EndZ=0
    g1: LineSegment StartX=-24 StartY=-3.28719 StartZ=0 EndX=-28 EndY=3.64102 EndZ=0
    g2: LineSegment StartX=-28 StartY=3.64102 StartZ=0 EndX=-36 EndY=3.64102 EndZ=0
    g3: LineSegment StartX=-36 StartY=3.64102 StartZ=0 EndX=-40 EndY=-3.28719 EndZ=0
    g4: LineSegment StartX=-40 StartY=-3.28719 StartZ=0 EndX=-36 EndY=-10.2154 EndZ=0
    g5: LineSegment StartX=-36 StartY=-10.2154 StartZ=0 EndX=-28 EndY=-10.2154 EndZ=0
    g6: Circle [constr] CenterX=-32 CenterY=-3.28719 CenterZ=0 NormalX=0 NormalY=0 NormalZ=1 AngleXU=0 Radius=8
    g7: LineSegment StartX=-12 StartY=-20.1436 StartZ=0 EndX=-8 EndY=-13.2154 EndZ=0
    g8: LineSegment StartX=-8 StartY=-13.2154 StartZ=0 EndX=-12 EndY=-6.28719 EndZ=0
    g9: LineSegment StartX=-12 StartY=-6.28719 StartZ=0 EndX=-20 EndY=-6.28719 EndZ=0
    g10: LineSegment StartX=-20 StartY=-6.28719 StartZ=0 EndX=-24 EndY=-13.2154 EndZ=0
    g11: LineSegment StartX=-24 StartY=-13.2154 StartZ=0 EndX=-20 EndY=-20.1436 EndZ=0
    g12: LineSegment StartX=-20 StartY=-20.1436 StartZ=0 EndX=-12 EndY=-20.1436 EndZ=0
    g13: Circle [constr] CenterX=-16 CenterY=-13.2154 CenterZ=0 NormalX=0 NormalY=0 NormalZ=1 AngleXU=0 Radius=8
    g14: LineSegment StartX=-24 StartY=-23.1436 StartZ=0 EndX=-28 EndY=-16.2154 EndZ=0
    g15: LineSegment StartX=-28 StartY=-16.2154 StartZ=0 EndX=-36 EndY=-16.2154 EndZ=0
    g16: LineSegment StartX=-36 StartY=-16.2154 StartZ=0 EndX=-40 EndY=-23.1436 EndZ=0
    g17: LineSegment StartX=-40 StartY=-23.1436 StartZ=0 EndX=-36 EndY=-30.0718 EndZ=0
    g18: LineSegment StartX=-36 StartY=-30.0718 StartZ=0 EndX=-28 EndY=-30.0718 EndZ=0
    g19: LineSegment StartX=-28 StartY=-30.0718 StartZ=0 EndX=-24 EndY=-23.1436 EndZ=0
    g20: Circle [constr] CenterX=-32 CenterY=-23.1436 CenterZ=0 NormalX=0 NormalY=0 NormalZ=1 AngleXU=0 Radius=8
    g21: LineSegment StartX=-12 StartY=-40 StartZ=0 EndX=-8 EndY=-33.0718 EndZ=0
    g22: LineSegment StartX=-8 StartY=-33.0718 StartZ=0 EndX=-12 EndY=-26.1436 EndZ=0
    g23: LineSegment StartX=-12 StartY=-26.1436 StartZ=0 EndX=-20 EndY=-26.1436 EndZ=0
    g24: LineSegment StartX=-20 StartY=-26.1436 StartZ=0 EndX=-24 EndY=-33.0718 EndZ=0
    g25: LineSegment StartX=-24 StartY=-33.0718 StartZ=0 EndX=-20 EndY=-40 EndZ=0
    g26: LineSegment StartX=-20 StartY=-40 StartZ=0 EndX=-12 EndY=-40 EndZ=0
    g27: Circle [constr] CenterX=-16 CenterY=-33.0718 CenterZ=0 NormalX=0 NormalY=0 NormalZ=1 AngleXU=0 Radius=8
    g28: LineSegment StartX=-20 StartY=32 StartZ=0 EndX=11.42 EndY=32 EndZ=0
    g29: LineSegment StartX=11.42 StartY=32 StartZ=0 EndX=11.42 EndY=15.3 EndZ=0
    g30: LineSegment StartX=11.42 StartY=15.3 StartZ=0 EndX=-20 EndY=15.3 EndZ=0
    g31: LineSegment StartX=-20 StartY=15.3 StartZ=0 EndX=-20 EndY=32 EndZ=0
    g32: LineSegment StartX=17 StartY=-25 StartZ=0 EndX=22 EndY=-16.3397 EndZ=0
    g33: LineSegment StartX=22 StartY=-16.3397 StartZ=0 EndX=17 EndY=-7.67949 EndZ=0
    g34: LineSegment StartX=17 StartY=-7.67949 StartZ=0 EndX=7 EndY=-7.67949 EndZ=0
    g35: LineSegment StartX=7 StartY=-7.67949 StartZ=0 EndX=2 EndY=-16.3397 EndZ=0
    g36: LineSegment StartX=2 StartY=-16.3397 StartZ=0 EndX=7 EndY=-25 EndZ=0
    g37: LineSegment StartX=7 StartY=-25 StartZ=0 EndX=17 EndY=-25 EndZ=0
    g38: Circle [constr] CenterX=12 CenterY=-16.3397 CenterZ=0 NormalX=0 NormalY=0 NormalZ=1 AngleXU=0 Radius=10
    g39: LineSegment StartX=35 StartY=-10.6795 StartZ=0 EndX=40 EndY=-2.01924 EndZ=0
    g40: LineSegment StartX=40 StartY=-2.01924 StartZ=0 EndX=35 EndY=6.64102 EndZ=0
    g41: LineSegment StartX=35 StartY=6.64102 StartZ=0 EndX=25 EndY=6.64102 EndZ=0
    g42: LineSegment StartX=25 StartY=6.64102 StartZ=0 EndX=20 EndY=-2.01924 EndZ=0
    g43: LineSegment StartX=20 StartY=-2.01924 StartZ=0 EndX=25 EndY=-10.6795 EndZ=0
    g44: LineSegment StartX=25 StartY=-10.6795 StartZ=0 EndX=35 EndY=-10.6795 EndZ=0
    g45: Circle [constr] CenterX=30 CenterY=-2.01924 CenterZ=0 NormalX=0 NormalY=0 NormalZ=1 AngleXU=0 Radius=10
    g46: LineSegment StartX=-37 StartY=50 StartZ=0 EndX=37 EndY=50 EndZ=0
    g47: LineSegment StartX=50 StartY=37 StartZ=0 EndX=50 EndY=-37 EndZ=0
    g48: LineSegment StartX=37 StartY=-50 StartZ=0 EndX=-37 EndY=-50 EndZ=0
    g49: LineSegment StartX=-50 StartY=-37 StartZ=0 EndX=-50 EndY=37 EndZ=0
    g50: ArcOfCircle CenterX=-37 CenterY=37 CenterZ=0 NormalX=0 NormalY=0 NormalZ=1 AngleXU=0 Radius=13 StartAngle=1.5708 EndAngle=3.14159
    g51: ArcOfCircle CenterX=37 CenterY=37 CenterZ=0 NormalX=0 NormalY=0 NormalZ=1 AngleXU=0 Radius=13 StartAngle=0 EndAngle=1.5708
    g52: ArcOfCircle CenterX=37 CenterY=-37 CenterZ=0 NormalX=0 NormalY=0 NormalZ=1 AngleXU=0 Radius=13 StartAngle=4.71239 EndAngle=6.28319
    g53: ArcOfCircle CenterX=-37 CenterY=-37 CenterZ=0 NormalX=0 NormalY=0 NormalZ=1 AngleXU=0 Radius=13 StartAngle=3.14159 EndAngle=4.71239
  constraints (133):
    c: Coincident(g0,g1)
    c: Coincident(g1,g2)
    c: Coincident(g2,g3)
    c: Coincident(g3,g4)
    c: Coincident(g4,g5)
    c: Coincident(g5,g0)
    c: Equal(g0, g1-g5) x5
    c: PointOnObject(g0,g6)
    c: PointOnObject(g1,g6)
    c: PointOnObject(g2,g6)
    c: PointOnObject(g3,g6)
    c: PointOnObject(g4,g6)
    c: PointOnObject(g5,g6)
    c: Parallel(g2,g-1)
    c: Radius(g6) = 8
    c: Coincident(g7,g8)
    c: Coincident(g8,g9)
    c: Coincident(g9,g10)
    c: Coincident(g10,g11)
    c: Coincident(g11,g12)
    c: Coincident(g12,g7)
    c: Equal(g7, g8-g12) x5
    c: PointOnObject(g7,g13)
    c: PointOnObject(g8,g13)
    c: PointOnObject(g9,g13)
    c: PointOnObject(g10,g13)
    c: PointOnObject(g11,g13)
    c: PointOnObject(g12,g13)
    c: Parallel(g9,g-1)
    c: Radius(g13) = 8
    c: DistanceX(g0,g9) = 4
    c: DistanceY(g9,g0) = 3
    c: Coincident(g14,g15)
    c: Coincident(g15,g16)
    c: Coincident(g16,g17)
    c: Coincident(g17,g18)
    c: Coincident(g18,g19)
    c: Coincident(g19,g14)
    c: Equal(g14, g15-g19) x5
    c: PointOnObject(g14,g20)
    c: PointOnObject(g15,g20)
    c: PointOnObject(g16,g20)
    c: PointOnObject(g17,g20)
    c: PointOnObject(g18,g20)
    c: PointOnObject(g19,g20)
    c: Parallel(g15,g-1)
    c: Radius(g20) = 8
    c: DistanceX(g14,g10) = 4
    c: DistanceY(g14,g10) = 3
    c: Coincident(g21,g22)
    c: Coincident(g22,g23)
    c: Coincident(g23,g24)
    c: Coincident(g24,g25)
    c: Coincident(g25,g26)
    c: Coincident(g26,g21)
    c: Equal(g21, g22-g26) x5
    c: PointOnObject(g21,g27)
    c: PointOnObject(g22,g27)
    c: PointOnObject(g23,g27)
    c: PointOnObject(g24,g27)
    c: PointOnObject(g25,g27)
    c: PointOnObject(g26,g27)
    c: Parallel(g23,g-1)
    c: Radius(g27) = 8
    c: DistanceX(g14,g23) = 4
    c: DistanceY(g23,g14) = 3
    c: Coincident(g28,g29)
    c: Coincident(g29,g30)
    c: Coincident(g30,g31)
    c: Coincident(g31,g28)
    c: Horizontal(g28)
    c: Horizontal(g30)
    c: Vertical(g29)
    c: Vertical(g31)
    c: DistanceX(g28,g28) = 31.42
    c: DistanceY(g31,g31) = 16.7
    c: Coincident(g32,g33)
    c: Coincident(g33,g34)
    c: Coincident(g34,g35)
    c: Coincident(g35,g36)
    c: Coincident(g36,g37)
    c: Coincident(g37,g32)
    c: Equal(g32, g33-g37) x5
    c: PointOnObject(g32,g38)
    c: PointOnObject(g33,g38)
    c: PointOnObject(g34,g38)
    c: PointOnObject(g35,g38)
    c: PointOnObject(g36,g38)
    c: PointOnObject(g37,g38)
    c: Parallel(g34,g30)
    c: Radius(g38) = 10
    c: Coincident(g39,g40)
    c: Coincident(g40,g41)
    c: Coincident(g41,g42)
    c: Coincident(g42,g43)
    c: Coincident(g43,g44)
    c: Coincident(g44,g39)
    c: Equal(g39, g40-g44) x5
    c: PointOnObject(g39,g45)
    c: PointOnObject(g40,g45)
    c: PointOnObject(g41,g45)
    c: PointOnObject(g42,g45)
    c: PointOnObject(g43,g45)
    c: PointOnObject(g44,g45)
    c: Radius(g45) = 10
    c: Parallel(g41,g30)
    c: DistanceY(g43,g33) = 3
    c: DistanceX(g33,g42) = 3
    c: Horizontal(g46)
    c: Horizontal(g48)
    c: Vertical(g47)
    c: Vertical(g49)
    c: Equal(g46,g47)
    c: Tangent(g49,g50) = 1.5708
    c: Tangent(g46,g50) = 1.5708
    c: Tangent(g46,g51) = 1.5708
    c: Tangent(g47,g51) = 1.5708
    c: Tangent(g47,g52) = 1.5708
    c: Tangent(g48,g52) = 1.5708
    c: Tangent(g49,g53) = 1.5708
    c: Tangent(g48,g53) = 1.5708
    c: Equal(g53,g50)
    c: Equal(g50,g51)
    c: Equal(g51,g52)
    c: Symmetric(g50,g52,g-1)
    c: Radius(g50) = 13
    c: DistanceY(g48,g46) = 100
    c: DistanceX(g49,g28) = 30
    c: DistanceY(g28,g46) = 18
    c: DistanceY(g48,g25) = 10
    c: DistanceX(g49,g16) = 10
    c: DistanceX(g39,g47) = 10
    c: DistanceY(g48,g36) = 25
FEATURE [PartDesign::Pad] Pad034  label="FaceplatePad"
  Length = 32
  Length2 = 100
  Placement = pos=(0,0,0) rot=(1,0,0;1.5708rad)
  Profile = -> Sketch061
  Type = 0
FEATURE [Sketcher::SketchObject] Sketch063  label="DisplayHollowSketch"
  MapMode = 5
  Placement = pos=(0,-32,1e-16) rot=(1,0,0;1.5708rad)
  Support = -> [Pad034]
  sketch-geometry (26):
    g0: LineSegment [constr] StartX=-6.49 StartY=13.012 StartZ=0 EndX=1.28 EndY=26.47 EndZ=0
    g1: LineSegment [constr] StartX=1.28 StartY=26.47 StartZ=0 EndX=-6.49 EndY=39.928 EndZ=0
    g2: LineSegment [constr] StartX=-6.49 StartY=39.928 StartZ=0 EndX=-22.03 EndY=39.928 EndZ=0
    g3: LineSegment [constr] StartX=-22.03 StartY=39.928 StartZ=0 EndX=-29.8 EndY=26.47 EndZ=0
    g4: LineSegment [constr] StartX=-29.8 StartY=26.47 StartZ=0 EndX=-22.03 EndY=13.012 EndZ=0
    g5: LineSegment [constr] StartX=-22.03 StartY=13.012 StartZ=0 EndX=-6.49 EndY=13.012 EndZ=0
    g6: Circle [constr] CenterX=-14.26 CenterY=26.47 CenterZ=0 NormalX=0 NormalY=0 NormalZ=1 AngleXU=0 Radius=15.54
    g7: LineSegment [constr] StartX=12.27 StartY=7.43476 StartZ=0 EndX=20.04 EndY=20.8928 EndZ=0
    g8: LineSegment [constr] StartX=20.04 StartY=20.8928 StartZ=0 EndX=12.27 EndY=34.3508 EndZ=0
    g9: LineSegment [constr] StartX=12.27 StartY=34.3508 StartZ=0 EndX=-3.27 EndY=34.3508 EndZ=0
    g10: LineSegment [constr] StartX=-3.27 StartY=34.3508 StartZ=0 EndX=-11.04 EndY=20.8928 EndZ=0
    g11: LineSegment [constr] StartX=-11.04 StartY=20.8928 StartZ=0 EndX=-3.27 EndY=7.43476 EndZ=0
    g12: LineSegment [constr] StartX=-3.27 StartY=7.43476 StartZ=0 EndX=12.27 EndY=7.43476 EndZ=0
    g13: Circle [constr] CenterX=4.5 CenterY=20.8928 CenterZ=0 NormalX=0 NormalY=0 NormalZ=1 AngleXU=0 Radius=15.54
    g14: GeomPoint X=-3.27 Y=34.3508 Z=0
    g15: GeomPoint X=-6.49 Y=13.012 Z=0
    g16: LineSegment StartX=-22.03 StartY=39.928 StartZ=0 EndX=-6.49 EndY=39.928 EndZ=0
    g17: LineSegment StartX=-6.49 StartY=39.928 StartZ=0 EndX=-3.27 EndY=34.3508 EndZ=0
    g18: LineSegment StartX=-3.27 StartY=34.3508 StartZ=0 EndX=12.27 EndY=34.3508 EndZ=0
    g19: LineSegment StartX=12.27 StartY=34.3508 StartZ=0 EndX=20.04 EndY=20.8928 EndZ=0
    g20: LineSegment StartX=20.04 StartY=20.8928 StartZ=0 EndX=12.27 EndY=7.43476 EndZ=0
    g21: LineSegment StartX=12.27 StartY=7.43476 StartZ=0 EndX=-3.27 EndY=7.43476 EndZ=0
    g22: LineSegment StartX=-3.27 StartY=7.43476 StartZ=0 EndX=-6.49 EndY=13.012 EndZ=0
    g23: LineSegment StartX=-6.49 StartY=13.012 StartZ=0 EndX=-22.03 EndY=13.012 EndZ=0
    g24: LineSegment StartX=-22.03 StartY=13.012 StartZ=0 EndX=-29.8 EndY=26.47 EndZ=0
    g25: LineSegment StartX=-29.8 StartY=26.47 StartZ=0 EndX=-22.03 EndY=39.928 EndZ=0
  constraints (57):
    c: Coincident(g0,g1)
    c: Coincident(g1,g2)
    c: Coincident(g2,g3)
    c: Coincident(g3,g4)
    c: Coincident(g4,g5)
    c: Coincident(g5,g0)
    c: Equal(g0, g1-g5) x5
    c: PointOnObject(g0,g6)
    c: PointOnObject(g1,g6)
    c: PointOnObject(g2,g6)
    c: PointOnObject(g3,g6)
    c: PointOnObject(g4,g6)
    c: PointOnObject(g5,g6)
    c: Coincident(g7,g8)
    c: Coincident(g8,g9)
    c: Coincident(g9,g10)
    c: Coincident(g10,g11)
    c: Coincident(g11,g12)
    c: Coincident(g12,g7)
    c: Equal(g7, g8-g12) x5
    c: PointOnObject(g7,g13)
    c: PointOnObject(g8,g13)
    c: PointOnObject(g9,g13)
    c: PointOnObject(g10,g13)
    c: PointOnObject(g11,g13)
    c: PointOnObject(g12,g13)
    c: PointOnObject(g14,g1)
    c: PointOnObject(g15,g0)
    c: Coincident(g16,g2)
    c: Coincident(g16,g1)
    c: Horizontal(g16)
    c: Coincident(g17,g16)
    c: Coincident(g17,g14)
    c: Coincident(g18,g8)
    c: Horizontal(g18)
    c: Coincident(g19,g18)
    c: Coincident(g19,g7)
    c: Coincident(g20,g19)
    c: Coincident(g20,g7)
    c: Coincident(g21,g20)
    c: Coincident(g21,g11)
    c: Coincident(g22,g21)
    c: Coincident(g22,g15)
    c: Coincident(g23,g4)
    c: Coincident(g24,g23)
    c: Coincident(g24,g3)
    c: Coincident(g25,g24)
    c: Coincident(g25,g16)
    c: Parallel(g11,g22)
    c: Coincident(g14,g18)
    c: Coincident(g14,g9)
    c: Coincident(g23,g15)
    c: PointOnObject(g0,g11)
    c: DistanceX(g-1,g13) = 4.5
    c: DistanceY(g-1,g6) = 26.47
    c: DistanceX(g6,g13) = 18.76
    c: DistanceX(g18,g18) = 15.54
FEATURE [PartDesign::Pocket] Pocket025  label="DisplayHollowPocket"
  BaseFeature = -> Pad034
  Length = 1
  Length2 = 100
  Placement = pos=(0,0,0) rot=(1,0,0;1.5708rad)
  Profile = -> Sketch063
  Type = 0
FEATURE [Sketcher::SketchObject] Sketch062  label="WallSketch"
  ExternalGeometry = -> [Pocket025]
  MapMode = 5
  Placement = pos=(0,0,0) rot=(-1,0,0;1.5708rad)
  Support = -> [Pocket025]
  sketch-geometry (8):
    g0: LineSegment StartX=-35 StartY=48 StartZ=0 EndX=35 EndY=48 EndZ=0
    g1: LineSegment StartX=48 StartY=35 StartZ=0 EndX=48 EndY=-35 EndZ=0
    g2: LineSegment StartX=35 StartY=-48 StartZ=0 EndX=-35 EndY=-48 EndZ=0
    g3: LineSegment StartX=-48 StartY=-35 StartZ=0 EndX=-48 EndY=35 EndZ=0
    g4: ArcOfCircle CenterX=35 CenterY=35 CenterZ=0 NormalX=0 NormalY=0 NormalZ=1 AngleXU=0 Radius=13 StartAngle=0 EndAngle=1.5708
    g5: ArcOfCircle CenterX=-35 CenterY=35 CenterZ=0 NormalX=0 NormalY=0 NormalZ=1 AngleXU=0 Radius=13 StartAngle=1.5708 EndAngle=3.14159
    g6: ArcOfCircle CenterX=-35 CenterY=-35 CenterZ=0 NormalX=0 NormalY=0 NormalZ=1 AngleXU=0 Radius=13 StartAngle=3.14159 EndAngle=4.71239
    g7: ArcOfCircle CenterX=35 CenterY=-35 CenterZ=0 NormalX=0 NormalY=0 NormalZ=1 AngleXU=0 Radius=13 StartAngle=4.71239 EndAngle=6.28319
  constraints (21):
    c: Horizontal(g0)
    c: Horizontal(g2)
    c: Vertical(g1)
    c: Vertical(g3)
    c: Tangent(g0,g4) = 1.5708
    c: Tangent(g1,g4) = 1.5708
    c: Tangent(g0,g5) = 1.5708
    c: Tangent(g3,g5) = 1.5708
    c: Tangent(g3,g6) = 1.5708
    c: Tangent(g2,g6) = 1.5708
    c: Tangent(g1,g7) = 1.5708
    c: Tangent(g2,g7) = 1.5708
    c: Equal(g7,g4)
    c: Equal(g4,g5)
    c: Equal(g5,g6)
    c: Radius(g5) = 13
    c: DistanceX(g-3,g3) = 2
    c: DistanceY(g0,g-4) = 2
    c: DistanceX(g1,g-5) = 2
    c: DistanceY(g-6,g2) = 2
    c: DistanceX(g3,g1) = 96
FEATURE [PartDesign::Pocket] Pocket024  label="WallPocket"
  BaseFeature = -> Pocket025
  Length = 29
  Length2 = 100
  Placement = pos=(0,0,0) rot=(1,0,0;1.5708rad)
  Profile = -> Sketch062
  Type = 0
FEATURE [Sketcher::SketchObject] Sketch060  label="BottomScrewHoleSketch"
  MapMode = 5
  Placement = pos=(0,-1.11e-14,-50) rot=(1,0,0;3.14159rad)
  Support = -> [Pocket024]
  sketch-geometry (1):
    g0: Circle CenterX=0 CenterY=5.5 CenterZ=0 NormalX=0 NormalY=0 NormalZ=1 AngleXU=0 Radius=1.3
  constraints (3):
    c: PointOnObject(g0,g-2)
    c: DistanceY(g-1,g0) = 5.5
    c: Radius(g0) = 1.3
FEATURE [PartDesign::Pocket] Pocket021  label="BottomScrewHolePocket"
  BaseFeature = -> Pocket024
  Length = 2
  Length2 = 100
  Placement = pos=(0,0,0) rot=(1,0,0;1.5708rad)
  Profile = -> Sketch060
  Type = 0
FEATURE [Sketcher::SketchObject] Sketch057  label="BottomScrewHollowSketch"
  ExternalGeometry = -> [Pocket021]
  MapMode = 5
  Placement = pos=(0,-1.11e-14,-50) rot=(1,0,0;3.14159rad)
  Support = -> [Pocket021]
  sketch-geometry (1):
    g0: Circle CenterX=0 CenterY=5.5 CenterZ=0 NormalX=0 NormalY=0 NormalZ=1 AngleXU=0 Radius=3
  constraints (2):
    c: Coincident(g0,g-3)
    c: Radius(g0) = 3
FEATURE [PartDesign::Pocket] Pocket023  label="BottomScrewHollowPocket"
  BaseFeature = -> Pocket021
  Length = 1
  Length2 = 100
  Placement = pos=(0,0,0) rot=(1,0,0;1.5708rad)
  Profile = -> Sketch057
  Type = 0
FEATURE [Sketcher::SketchObject] Sketch065  label="PcbScrewHolesSketch"
  ExternalGeometry = -> [Sketch061]
  MapMode = 5
  Placement = pos=(0,-29,1e-16) rot=(-1,0,0;1.5708rad)
  Support = -> [Pocket024]
  sketch-geometry (24):
    g0: Circle CenterX=-39.5 CenterY=39.5 CenterZ=0 NormalX=0 NormalY=0 NormalZ=1 AngleXU=0 Radius=0.9
    g1: Circle CenterX=-39.5 CenterY=39.5 CenterZ=0 NormalX=0 NormalY=0 NormalZ=1 AngleXU=0 Radius=3
    g2: Circle CenterX=39.5 CenterY=39.5 CenterZ=0 NormalX=0 NormalY=0 NormalZ=1 AngleXU=0 Radius=0.9
    g3: Circle CenterX=39.5 CenterY=39.5 CenterZ=0 NormalX=0 NormalY=0 NormalZ=1 AngleXU=0 Radius=3
    g4: Circle CenterX=-39.5 CenterY=-39.5 CenterZ=0 NormalX=0 NormalY=0 NormalZ=1 AngleXU=0 Radius=0.9
    g5: Circle CenterX=-39.5 CenterY=-39.5 CenterZ=0 NormalX=0 NormalY=0 NormalZ=1 AngleXU=0 Radius=3
    g6: Circle CenterX=39.5 CenterY=-39.5 CenterZ=0 NormalX=0 NormalY=0 NormalZ=1 AngleXU=0 Radius=0.9
    g7: Circle CenterX=39.5 CenterY=-39.5 CenterZ=0 NormalX=0 NormalY=0 NormalZ=1 AngleXU=0 Radius=3
    g8: LineSegment [constr] StartX=-39.5 StartY=39.5 StartZ=0 EndX=39.5 EndY=39.5 EndZ=0
    g9: LineSegment [constr] StartX=39.5 StartY=39.5 StartZ=0 EndX=39.5 EndY=-39.5 EndZ=0
    g10: LineSegment [constr] StartX=39.5 StartY=-39.5 StartZ=0 EndX=-39.5 EndY=-39.5 EndZ=0
    g11: LineSegment [constr] StartX=-39.5 StartY=-39.5 StartZ=0 EndX=-39.5 EndY=39.5 EndZ=0
    g12: Circle [constr] CenterX=-16 CenterY=33.0718 CenterZ=0 NormalX=0 NormalY=0 NormalZ=1 AngleXU=0 Radius=8
    g13: Circle [constr] CenterX=-32 CenterY=23.1436 CenterZ=0 NormalX=0 NormalY=0 NormalZ=1 AngleXU=0 Radius=8
    g14: Circle [constr] CenterX=-16 CenterY=13.2154 CenterZ=0 NormalX=0 NormalY=0 NormalZ=1 AngleXU=0 Radius=8
    g15: Circle [constr] CenterX=-32 CenterY=3.28719 CenterZ=0 NormalX=0 NormalY=0 NormalZ=1 AngleXU=0 Radius=8
    g16: Circle [constr] CenterX=12 CenterY=16.3397 CenterZ=0 NormalX=0 NormalY=0 NormalZ=1 AngleXU=0 Radius=10
    g17: Circle [constr] CenterX=30 CenterY=2.01924 CenterZ=0 NormalX=0 NormalY=0 NormalZ=1 AngleXU=0 Radius=10
    g18: LineSegment [constr] StartX=43.5 StartY=-43.5 StartZ=0 EndX=-43.5 EndY=-43.5 EndZ=0
    g19: LineSegment [constr] StartX=-43.5 StartY=-43.5 StartZ=0 EndX=-43.5 EndY=43.5 EndZ=0
    g20: LineSegment [constr] StartX=-43.5 StartY=43.5 StartZ=0 EndX=43.5 EndY=43.5 EndZ=0
    g21: LineSegment [constr] StartX=43.5 StartY=43.5 StartZ=0 EndX=43.5 EndY=-43.5 EndZ=0
    g22: Circle CenterX=-2.5 CenterY=10.5 CenterZ=0 NormalX=0 NormalY=0 NormalZ=1 AngleXU=0 Radius=0.9
    g23: Circle CenterX=-2.5 CenterY=10.5 CenterZ=0 NormalX=0 NormalY=0 NormalZ=1 AngleXU=0 Radius=3
  constraints (75):
    c: Coincident(g1,g0)
    c: Coincident(g5,g4)
    c: Coincident(g7,g6)
    c: Equal(g4,g6)
    c: Equal(g6,g2)
    c: Equal(g2,g0)
    c: Equal(g1,g3)
    c: Equal(g3,g7)
    c: Equal(g7,g5)
    c: Radius(g0) = 0.9
    c: Radius(g1) = 3
    c: Coincident(g8,g9)
    c: Coincident(g9,g10)
    c: Coincident(g10,g11)
    c: Coincident(g11,g8)
    c: Horizontal(g8)
    c: Horizontal(g10)
    c: Vertical(g9)
    c: Vertical(g11)
    c: Coincident(g8,g0)
    c: Coincident(g9,g6)
    c: Coincident(g8,g2)
    c: Coincident(g3,g2)
    c: Coincident(g4,g10)
    c: Symmetric(g0,g6,g-1)
    c: PointOnObject(g-3,g12)
    c: PointOnObject(g-4,g12)
    c: PointOnObject(g-5,g12)
    c: PointOnObject(g-6,g13)
    c: PointOnObject(g-7,g13)
    c: PointOnObject(g-8,g13)
    c: PointOnObject(g-9,g14)
    c: PointOnObject(g-10,g14)
    c: PointOnObject(g-11,g14)
    c: PointOnObject(g-12,g15)
    c: PointOnObject(g-13,g15)
    c: PointOnObject(g-14,g15)
    c: PointOnObject(g-15,g16)
    c: PointOnObject(g-16,g16)
    c: PointOnObject(g-17,g16)
    c: PointOnObject(g-18,g17)
    c: PointOnObject(g-19,g17)
    c: PointOnObject(g-20,g17)
    c: Coincident(g18,g19)
    c: Coincident(g19,g20)
    c: Coincident(g20,g21)
    c: Coincident(g21,g18)
    c: Horizontal(g18)
    c: Horizontal(g20)
    c: Vertical(g19)
    c: Vertical(g21)
    c: Equal(g19,g18)
    c: DistanceX(g18,g18) = 87
    c: Symmetric(g18,g19,g-1)
    c: DistanceX(g2,g20) = 4
    c: DistanceY(g2,g20) = 4
    c: DistanceX(g4,g18) = 83
    c: DistanceY(g18,g2) = 83
    c: DistanceX(g17,g18) = 13.5
    c: DistanceY(g18,g17) = 45.5192
    c: DistanceX(g16,g18) = 31.5
    c: DistanceY(g18,g16) = 59.8397
    c: DistanceX(g15,g18) = 75.5
    c: DistanceY(g18,g15) = 46.7872
    c: DistanceX(g14,g18) = 59.5
    c: DistanceY(g18,g14) = 56.7154
    c: DistanceX(g13,g18) = 75.5
    c: DistanceX(g12,g18) = 59.5
    c: DistanceY(g18,g12) = 76.5718
    c: DistanceY(g18,g13) = 66.6436
    c: Coincident(g23,g22)
    c: Equal(g6,g22)
    c: Equal(g7,g23)
    c: DistanceX(g22,g18) = 46
    c: DistanceY(g18,g22) = 54
FEATURE [Sketcher::SketchObject] Sketch058  label="BottomScrewRingSketch"
  ExternalGeometry = -> [Pocket023]
  MapMode = 5
  Placement = pos=(0,-1.11e-14,-50) rot=(1,0,0;3.14159rad)
  Support = -> [Pocket023]
  sketch-geometry (2):
    g0: Circle CenterX=0 CenterY=5.5 CenterZ=0 NormalX=0 NormalY=0 NormalZ=1 AngleXU=0 Radius=3
    g1: Circle CenterX=0 CenterY=5.5 CenterZ=0 NormalX=0 NormalY=0 NormalZ=1 AngleXU=0 Radius=3.5
  constraints (4):
    c: Coincident(g0,g-3)
    c: Coincident(g1,g0)
    c: Radius(g1) = 3.5
    c: Radius(g0) = 3
FEATURE [PartDesign::Pad] Pad038  label="BottomScrewRingPad"
  BaseFeature = -> Pocket023
  Length = 1
  Length2 = 100
  Placement = pos=(0,0,0) rot=(1,0,0;1.5708rad)
  Profile = -> Sketch058
  Type = 0
FEATURE [Sketcher::SketchObject] Sketch059  label="TopLatchesSketch"
  MapMode = 5
  Placement = pos=(0,1.07e-14,48) rot=(1,0,0;3.14159rad)
  Support = -> [Pad038]
  sketch-geometry (8):
    g0: LineSegment StartX=11 StartY=3 StartZ=0 EndX=29 EndY=3 EndZ=0
    g1: LineSegment StartX=29 StartY=3 StartZ=0 EndX=29 EndY=5 EndZ=0
    g2: LineSegment StartX=29 StartY=5 StartZ=0 EndX=11 EndY=5 EndZ=0
    g3: LineSegment StartX=11 StartY=5 StartZ=0 EndX=11 EndY=3 EndZ=0
    g4: LineSegment StartX=-29 StartY=3 StartZ=0 EndX=-11 EndY=3 EndZ=0
    g5: LineSegment StartX=-11 StartY=3 StartZ=0 EndX=-11 EndY=5 EndZ=0
    g6: LineSegment StartX=-11 StartY=5 StartZ=0 EndX=-29 EndY=5 EndZ=0
    g7: LineSegment StartX=-29 StartY=5 StartZ=0 EndX=-29 EndY=3 EndZ=0
  constraints (24):
    c: Coincident(g0,g1)
    c: Coincident(g1,g2)
    c: Coincident(g2,g3)
    c: Coincident(g3,g0)
    c: Horizontal(g0)
    c: Horizontal(g2)
    c: Vertical(g1)
    c: Vertical(g3)
    c: Coincident(g4,g5)
    c: Coincident(g5,g6)
    c: Coincident(g6,g7)
    c: Coincident(g7,g4)
    c: Horizontal(g4)
    c: Horizontal(g6)
    c: Vertical(g5)
    c: Vertical(g7)
    c: Equal(g5,g3)
    c: DistanceY(g5,g5) = 2
    c: DistanceX(g5,g-1) = 11
    c: DistanceX(g-1,g2) = 11
    c: DistanceY(g-1,g4) = 3
    c: DistanceY(g-1,g0) = 3
    c: Equal(g6,g2)
    c: DistanceX(g6,g6) = 18
FEATURE [PartDesign::Pad] Pad035  label="TopLatchesPad"
  BaseFeature = -> Pad038
  Length = 2.5
  Length2 = 100
  Placement = pos=(0,0,0) rot=(1,0,0;1.5708rad)
  Profile = -> Sketch059
  Type = 0
FEATURE [PartDesign::Pad] Pad037  label="PcbScrewHolesPad"
  BaseFeature = -> Pad035
  Length = 8
  Length2 = 100
  Placement = pos=(0,0,0) rot=(1,0,0;1.5708rad)
  Profile = -> Sketch065
  Type = 0
FEATURE [Sketcher::SketchObject] Sketch075  label="DisplayMountingPolesSketch"
  ExternalGeometry = -> [Sketch061]
  MapMode = 5
  Placement = pos=(0,-29,1e-16) rot=(-1,0,0;1.5708rad)
  Support = -> [Pad037]
  expr: Constraints[19] = (31.42 - 30.5) / 2
  sketch-geometry (8):
    g0: Circle CenterX=-19.54 CenterY=-6.62 CenterZ=0 NormalX=0 NormalY=0 NormalZ=1 AngleXU=0 Radius=1.7
    g1: Circle CenterX=10.96 CenterY=-6.62 CenterZ=0 NormalX=0 NormalY=0 NormalZ=1 AngleXU=0 Radius=1.7
    g2: Circle CenterX=-19.54 CenterY=-35.52 CenterZ=0 NormalX=0 NormalY=0 NormalZ=1 AngleXU=0 Radius=1.7
    g3: Circle CenterX=10.96 CenterY=-35.52 CenterZ=0 NormalX=0 NormalY=0 NormalZ=1 AngleXU=0 Radius=1.7
    g4: LineSegment [constr] StartX=-19.54 StartY=-6.62 StartZ=0 EndX=10.96 EndY=-6.62 EndZ=0
    g5: LineSegment [constr] StartX=10.96 StartY=-6.62 StartZ=0 EndX=10.96 EndY=-35.52 EndZ=0
    g6: LineSegment [constr] StartX=10.96 StartY=-35.52 StartZ=0 EndX=-19.54 EndY=-35.52 EndZ=0
    g7: LineSegment [constr] StartX=-19.54 StartY=-35.52 StartZ=0 EndX=-19.54 EndY=-6.62 EndZ=0
  constraints (20):
    c: Equal(g0,g2)
    c: Equal(g2,g3)
    c: Equal(g3,g1)
    c: Radius(g0) = 1.7
    c: Coincident(g4,g5)
    c: Coincident(g5,g6)
    c: Coincident(g6,g7)
    c: Coincident(g7,g4)
    c: Horizontal(g4)
    c: Horizontal(g6)
    c: Vertical(g5)
    c: Vertical(g7)
    c: Coincident(g4,g0)
    c: Coincident(g5,g3)
    c: Coincident(g4,g1)
    c: Coincident(g2,g6)
    c: DistanceX(g4,g4) = 30.5
    c: DistanceY(g5,g5) = 28.9
    c: DistanceY(g2,g-5) = 3.52
    c: DistanceX(g-5,g2) = 0.46
FEATURE [PartDesign::Pad] Pad045  label="DisplayMountingPolesPad"
  BaseFeature = -> Pad037
  Length = 2
  Length2 = 100
  Placement = pos=(0,0,0) rot=(1,0,0;1.5708rad)
  Profile = -> Sketch075
  Type = 0
FEATURE [PartDesign::Plane] DatumPlane  label="DisplayScrewPolesDatumPlane"
  Length = 120.1
  MapMode = 5
  Placement = pos=(0,-27,6e-15) rot=(-1,0,0;1.5708rad)
  ResizeMode = 0
  Support = -> [Pad045]
  Width = 121.1
FEATURE [Sketcher::SketchObject] Sketch066  label="DisplayScrewHolesSketch"
  ExternalGeometry = -> [Pad045]
  MapMode = 5
  Placement = pos=(0,-27,6e-15) rot=(-1,0,0;1.5708rad)
  Support = -> [DatumPlane]
  sketch-geometry (4):
    g0: Circle CenterX=-19.54 CenterY=-6.62 CenterZ=0 NormalX=0 NormalY=0 NormalZ=1 AngleXU=0 Radius=0.9
    g1: Circle CenterX=10.96 CenterY=-6.62 CenterZ=0 NormalX=0 NormalY=0 NormalZ=1 AngleXU=0 Radius=0.9
    g2: Circle CenterX=10.96 CenterY=-35.52 CenterZ=0 NormalX=0 NormalY=0 NormalZ=1 AngleXU=0 Radius=0.9
    g3: Circle CenterX=-19.54 CenterY=-35.52 CenterZ=0 NormalX=0 NormalY=0 NormalZ=1 AngleXU=0 Radius=0.9
  constraints (8):
    c: Equal(g3,g0)
    c: Equal(g0,g1)
    c: Equal(g1,g2)
    c: Radius(g2) = 0.9
    c: Coincident(g0,g-3)
    c: Coincident(g1,g-4)
    c: Coincident(g3,g-5)
    c: Coincident(g2,g-6)
FEATURE [PartDesign::Pocket] Pocket028  label="DisplayScrewHolesPocket"
  BaseFeature = -> Pad045
  Length = 3
  Length2 = 100
  Placement = pos=(0,0,0) rot=(1,0,0;1.5708rad)
  Profile = -> Sketch066
  Type = 0
FEATURE [Sketcher::SketchObject] Sketch078  label="TopVentHoleSketch"
  MapMode = 5
  Placement = pos=(0,1.1e-14,50) rot=(0,0,1;3.14159rad)
  sketch-geometry (21):
    g0: LineSegment StartX=-29 StartY=10.7321 StartZ=0 EndX=-30 EndY=12.4641 EndZ=0
    g1: LineSegment StartX=-30 StartY=12.4641 StartZ=0 EndX=-32 EndY=12.4641 EndZ=0
    g2: LineSegment StartX=-32 StartY=12.4641 StartZ=0 EndX=-33 EndY=10.7321 EndZ=0
    g3: LineSegment StartX=-33 StartY=10.7321 StartZ=0 EndX=-32 EndY=9 EndZ=0
    g4: LineSegment StartX=-32 StartY=9 StartZ=0 EndX=-30 EndY=9 EndZ=0
    g5: LineSegment StartX=-30 StartY=9 StartZ=0 EndX=-29 EndY=10.7321 EndZ=0
    g6: Circle [constr] CenterX=-31 CenterY=10.7321 CenterZ=0 NormalX=0 NormalY=0 NormalZ=1 AngleXU=0 Radius=2
    g7: LineSegment StartX=-26 StartY=16.1962 StartZ=0 EndX=-27 EndY=17.9282 EndZ=0
    g8: LineSegment StartX=-27 StartY=17.9282 StartZ=0 EndX=-29 EndY=17.9282 EndZ=0
    g9: LineSegment StartX=-29 StartY=17.9282 StartZ=0 EndX=-30 EndY=16.1962 EndZ=0
    g10: LineSegment StartX=-30 StartY=16.1962 StartZ=0 EndX=-29 EndY=14.4641 EndZ=0
    g11: LineSegment StartX=-29 StartY=14.4641 StartZ=0 EndX=-27 EndY=14.4641 EndZ=0
    g12: LineSegment StartX=-27 StartY=14.4641 StartZ=0 EndX=-26 EndY=16.1962 EndZ=0
    g13: Circle [constr] CenterX=-28 CenterY=16.1962 CenterZ=0 NormalX=0 NormalY=0 NormalZ=1 AngleXU=0 Radius=2
    g14: LineSegment StartX=-29 StartY=21.6603 StartZ=0 EndX=-30 EndY=23.3923 EndZ=0
    g15: LineSegment StartX=-30 StartY=23.3923 StartZ=0 EndX=-32 EndY=23.3923 EndZ=0
    g16: LineSegment StartX=-32 StartY=23.3923 StartZ=0 EndX=-33 EndY=21.6603 EndZ=0
    g17: LineSegment StartX=-33 StartY=21.6603 StartZ=0 EndX=-32 EndY=19.9282 EndZ=0
    g18: LineSegment StartX=-32 StartY=19.9282 StartZ=0 EndX=-30 EndY=19.9282 EndZ=0
    g19: LineSegment StartX=-30 StartY=19.9282 StartZ=0 EndX=-29 EndY=21.6603 EndZ=0
    g20: Circle [constr] CenterX=-31 CenterY=21.6603 CenterZ=0 NormalX=0 NormalY=0 NormalZ=1 AngleXU=0 Radius=2
  constraints (51):
    c: Coincident(g0,g1)
    c: Coincident(g1,g2)
    c: Coincident(g2,g3)
    c: Coincident(g3,g4)
    c: Coincident(g4,g5)
    c: Coincident(g5,g0)
    c: Equal(g0, g1-g5) x5
    c: PointOnObject(g0,g6)
    c: PointOnObject(g1,g6)
    c: PointOnObject(g2,g6)
    c: PointOnObject(g3,g6)
    c: PointOnObject(g4,g6)
    c: PointOnObject(g5,g6)
    c: Horizontal(g4)
    c: Radius(g6) = 2
    c: Coincident(g7,g8)
    c: Coincident(g8,g9)
    c: Coincident(g9,g10)
    c: Coincident(g10,g11)
    c: Coincident(g11,g12)
    c: Coincident(g12,g7)
    c: Equal(g7, g8-g12) x5
    c: PointOnObject(g7,g13)
    c: PointOnObject(g8,g13)
    c: PointOnObject(g9,g13)
    c: PointOnObject(g10,g13)
    c: PointOnObject(g11,g13)
    c: PointOnObject(g12,g13)
    c: Horizontal(g11)
    c: Radius(g13) = 2
    c: Coincident(g14,g15)
    c: Coincident(g15,g16)
    c: Coincident(g16,g17)
    c: Coincident(g17,g18)
    c: Coincident(g18,g19)
    c: Coincident(g19,g14)
    c: Equal(g14, g15-g19) x5
    c: PointOnObject(g14,g20)
    c: PointOnObject(g15,g20)
    c: PointOnObject(g16,g20)
    c: PointOnObject(g17,g20)
    c: PointOnObject(g18,g20)
    c: PointOnObject(g19,g20)
    c: Horizontal(g18)
    c: Radius(g20) = 2
    c: DistanceX(g18,g0) = 0
    c: DistanceX(g18,g9) = 0
    c: DistanceY(g0,g10) = 2
    c: DistanceY(g8,g18) = 2
    c: DistanceY(g-1,g4) = 9
    c: DistanceX(g4,g-1) = 30
FEATURE [PartDesign::Pocket] Pocket030  label="TopVentHolePocket"
  BaseFeature = -> Pocket028
  Length = 2
  Length2 = 100
  Placement = pos=(0,0,0) rot=(1,0,0;1.5708rad)
  Profile = -> Sketch078
  Type = 0
FEATURE [PartDesign::LinearPattern] LinearPattern  label="TopVentHolePattern"
  BaseFeature = -> Pocket030
  Direction = -> Sketch078 [H_Axis]
  Length = 59
  Occurrences = 10
  Originals = -> [Pocket030]
  Placement = pos=(0,0,0) rot=(1,0,0;1.5708rad)
FEATURE [Sketcher::SketchObject] Sketch079  label="TopDustShieldSketch"
  MapMode = 5
  Placement = pos=(0,-29,1e-16) rot=(-1,0,0;1.5708rad)
  Support = -> [LinearPattern]
  expr: Constraints[9] = 75 / 2
  sketch-geometry (4):
    g0: LineSegment StartX=-37.5 StartY=-43.9 StartZ=0 EndX=37.5 EndY=-43.9 EndZ=0
    g1: LineSegment StartX=37.5 StartY=-43.9 StartZ=0 EndX=37.5 EndY=-45.1 EndZ=0
    g2: LineSegment StartX=37.5 StartY=-45.1 StartZ=0 EndX=-37.5 EndY=-45.1 EndZ=0
    g3: LineSegment StartX=-37.5 StartY=-45.1 StartZ=0 EndX=-37.5 EndY=-43.9 EndZ=0
  constraints (12):
    c: Coincident(g0,g1)
    c: Coincident(g1,g2)
    c: Coincident(g2,g3)
    c: Coincident(g3,g0)
    c: Horizontal(g0)
    c: Horizontal(g2)
    c: Vertical(g1)
    c: Vertical(g3)
    c: DistanceX(g2,g2) = 75
    c: DistanceX(g2,g-1) = 37.5
    c: DistanceY(g1,g1) = 1.2
    c: DistanceY(g0,g-1) = 43.9
FEATURE [PartDesign::Pad] Pad047  label="TopDustShieldPad"
  BaseFeature = -> LinearPattern
  Length = 20.5
  Length2 = 100
  Placement = pos=(0,0,0) rot=(1,0,0;1.5708rad)
  Profile = -> Sketch079
  Type = 0
FEATURE [PartDesign::Chamfer] Chamfer011  label="TopDustShieldBaseChamfer"
  Base = -> Pad047 [Edge752,Edge754]
  BaseFeature = -> Pad047
  Placement = pos=(0,0,0) rot=(1,0,0;1.5708rad)
  Size = 0.9
FEATURE [PartDesign::Fillet] Fillet004  label="PcbMountingHolesFillet"
  Base = -> Chamfer011 [Edge65,Edge63,Edge18,Edge61,Edge54]
  BaseFeature = -> Chamfer011
  Placement = pos=(0,0,0) rot=(1,0,0;1.5708rad)
  Radius = 1
FEATURE [PartDesign::Fillet] Fillet005  label="DisplayMountingHolesFillet"
  Base = -> Fillet004 [Edge60,Edge61,Edge49,Edge18]
  BaseFeature = -> Fillet004
  Placement = pos=(0,0,0) rot=(1,0,0;1.5708rad)
  Radius = 1
FEATURE [PartDesign::Chamfer] Chamfer012  label="TopLatchBaseChamfer"
  Base = -> Pad044 [Edge53]
  BaseFeature = -> Pad044
  Placement = pos=(0,0,0) rot=(1,0,0;1.5708rad)
  Size = 2.99
FEATURE [PartDesign::Chamfer] Chamfer013  label="BottomLatchBaseChamfer"
  Base = -> Chamfer012 [Edge26]
  BaseFeature = -> Chamfer012
  Placement = pos=(0,0,0) rot=(1,0,0;1.5708rad)
  Size = 2.99
FEATURE [Sketcher::SketchObject] Sketch080  label="MountingHolesSketch"
  MapMode = 5
  Placement = pos=(0,0,0) rot=(1,0,0;1.5708rad)
  Support = -> [Chamfer013]
  expr: Constraints[11] = 30 - 2
  sketch-geometry (20):
    g0: LineSegment [constr] StartX=-15 StartY=32 StartZ=0 EndX=15 EndY=32 EndZ=0
    g1: LineSegment [constr] StartX=15 StartY=32 StartZ=0 EndX=15 EndY=28 EndZ=0
    g2: LineSegment [constr] StartX=15 StartY=28 StartZ=0 EndX=-15 EndY=28 EndZ=0
    g3: LineSegment [constr] StartX=-15 StartY=28 StartZ=0 EndX=-15 EndY=32 EndZ=0
    g4: Circle [constr] CenterX=-15 CenterY=30 CenterZ=0 NormalX=0 NormalY=0 NormalZ=1 AngleXU=0 Radius=2
    g5: Circle [constr] CenterX=15 CenterY=30 CenterZ=0 NormalX=0 NormalY=0 NormalZ=1 AngleXU=0 Radius=2
    g6: LineSegment StartX=-15 StartY=32 StartZ=0 EndX=15 EndY=32 EndZ=0
    g7: LineSegment StartX=-15 StartY=28 StartZ=0 EndX=15 EndY=28 EndZ=0
    g8: LineSegment [constr] StartX=-2 StartY=-15 StartZ=0 EndX=2 EndY=-15 EndZ=0
    g9: LineSegment [constr] StartX=2 StartY=-15 StartZ=0 EndX=2 EndY=-35 EndZ=0
    g10: LineSegment [constr] StartX=2 StartY=-35 StartZ=0 EndX=-2 EndY=-35 EndZ=0
    g11: LineSegment [constr] StartX=-2 StartY=-35 StartZ=0 EndX=-2 EndY=-15 EndZ=0
    g12: Circle [constr] CenterX=0 CenterY=-35 CenterZ=0 NormalX=0 NormalY=0 NormalZ=1 AngleXU=0 Radius=2
    g13: Circle [constr] CenterX=0 CenterY=-15 CenterZ=0 NormalX=0 NormalY=0 NormalZ=1 AngleXU=0 Radius=2
    g14: ArcOfCircle CenterX=15 CenterY=30 CenterZ=0 NormalX=0 NormalY=0 NormalZ=1 AngleXU=0 Radius=2 StartAngle=4.71239 EndAngle=7.85398
    g15: ArcOfCircle CenterX=-15 CenterY=30 CenterZ=0 NormalX=0 NormalY=0 NormalZ=1 AngleXU=0 Radius=2 StartAngle=1.5708 EndAngle=4.71239
    g16: LineSegment StartX=2 StartY=-15 StartZ=0 EndX=2 EndY=-35 EndZ=0
    g17: LineSegment StartX=-2 StartY=-15 StartZ=0 EndX=-2 EndY=-35 EndZ=0
    g18: ArcOfCircle CenterX=0 CenterY=-15 CenterZ=0 NormalX=0 NormalY=0 NormalZ=1 AngleXU=0 Radius=2 StartAngle=0 EndAngle=3.14159
    g19: ArcOfCircle CenterX=0 CenterY=-35 CenterZ=0 NormalX=0 NormalY=0 NormalZ=1 AngleXU=0 Radius=2 StartAngle=3.14159 EndAngle=6.28319
  constraints (55):
    c: Coincident(g0,g1)
    c: Coincident(g1,g2)
    c: Coincident(g2,g3)
    c: Coincident(g3,g0)
    c: Horizontal(g0)
    c: Horizontal(g2)
    c: Vertical(g1)
    c: Vertical(g3)
    c: DistanceX(g0,g0) = 30
    c: DistanceY(g3,g3) = 4
    c: DistanceX(g2,g-1) = 15
    c: DistanceY(g-1,g2) = 28
    c: PointOnObject(g0,g4)
    c: PointOnObject(g2,g4)
    c: PointOnObject(g4,g3)
    c: PointOnObject(g0,g5)
    c: PointOnObject(g1,g5)
    c: PointOnObject(g5,g1)
    c: Coincident(g8,g9)
    c: Coincident(g9,g10)
    c: Coincident(g10,g11)
    c: Coincident(g11,g8)
    c: Horizontal(g8)
    c: Horizontal(g10)
    c: Vertical(g9)
    c: Vertical(g11)
    c: DistanceY(g9,g9) = 20
    c: DistanceX(g8,g8) = 4
    c: DistanceX(g8,g-1) = 2
    c: DistanceY(g8,g-1) = 15
    c: PointOnObject(g10,g12)
    c: PointOnObject(g9,g12)
    c: PointOnObject(g12,g10)
    c: PointOnObject(g8,g13)
    c: PointOnObject(g13,g8)
    c: Coincident(g6,g0)
    c: Coincident(g6,g0)
    c: Coincident(g7,g2)
    c: Coincident(g1,g7)
    c: Coincident(g14,g6)
    c: Coincident(g14,g7)
    c: Tangent(g14,g5)
    c: Coincident(g15,g7)
    c: Coincident(g15,g6)
    c: Tangent(g15,g4)
    c: Coincident(g16,g8)
    c: Coincident(g17,g8)
    c: Coincident(g17,g10)
    c: Coincident(g16,g9)
    c: Coincident(g18,g17)
    c: Coincident(g18,g16)
    c: Coincident(g18,g13)
    c: Coincident(g19,g17)
    c: Coincident(g19,g16)
    c: PointOnObject(g19,g10)
FEATURE [PartDesign::Pocket] Pocket031  label="MountingHolesPocket"
  BaseFeature = -> Chamfer013
  Length = 3
  Length2 = 100
  Placement = pos=(0,0,0) rot=(1,0,0;1.5708rad)
  Profile = -> Sketch080
  Type = 0
FEATURE [Sketcher::SketchObject] Sketch081  label="CableHoleSketch"
  MapMode = 5
  Placement = pos=(0,0,0) rot=(1,0,0;1.5708rad)
  Support = -> [Pocket031]
  sketch-geometry (4):
    g0: LineSegment StartX=-15 StartY=15 StartZ=0 EndX=15 EndY=15 EndZ=0
    g1: LineSegment StartX=15 StartY=15 StartZ=0 EndX=15 EndY=-5 EndZ=0
    g2: LineSegment StartX=15 StartY=-5 StartZ=0 EndX=-15 EndY=-5 EndZ=0
    g3: LineSegment StartX=-15 StartY=-5 StartZ=0 EndX=-15 EndY=15 EndZ=0
  constraints (12):
    c: Coincident(g0,g1)
    c: Coincident(g1,g2)
    c: Coincident(g2,g3)
    c: Coincident(g3,g0)
    c: Horizontal(g0)
    c: Horizontal(g2)
    c: Vertical(g1)
    c: Vertical(g3)
    c: DistanceY(g1,g1) = 20
    c: DistanceX(g0,g0) = 30
    c: DistanceX(g0,g-1) = 15
    c: DistanceY(g1,g-1) = 5
FEATURE [PartDesign::Pocket] Pocket032  label="CableHolePocket"
  BaseFeature = -> Pocket031
  Length = 3
  Length2 = 100
  Placement = pos=(0,0,0) rot=(1,0,0;1.5708rad)
  Profile = -> Sketch081
  Type = 0
FEATURE [PartDesign::Body] Body013  label="Backplate - v5"
  Group = -> [Sketch071,Pad042,Sketch070,Pad039,Sketch069,Pad043,Sketch067,Pocket026,Sketch072,Pad040,Fillet003,Sketch073,Pocket027,Sketch074,Pad044,Chamfer012,Chamfer013,Sketch080,Pocket031,Sketch081,Pocket032]
  Origin = -> Origin021
  Tip = -> Pocket032
FEATURE [Sketcher::SketchObject] Sketch082  label="BottomVentHoleSketch"
  MapMode = 5
  Placement = pos=(0,-1.11e-14,-50) rot=(1,0,0;3.14159rad)
  Support = -> [Fillet005]
  sketch-geometry (21):
    g0: LineSegment StartX=-29 StartY=21.6603 StartZ=0 EndX=-30 EndY=23.3923 EndZ=0
    g1: LineSegment StartX=-30 StartY=23.3923 StartZ=0 EndX=-32 EndY=23.3923 EndZ=0
    g2: LineSegment StartX=-32 StartY=23.3923 StartZ=0 EndX=-33 EndY=21.6603 EndZ=0
    g3: LineSegment StartX=-33 StartY=21.6603 StartZ=0 EndX=-32 EndY=19.9282 EndZ=0
    g4: LineSegment StartX=-32 StartY=19.9282 StartZ=0 EndX=-30 EndY=19.9282 EndZ=0
    g5: LineSegment StartX=-30 StartY=19.9282 StartZ=0 EndX=-29 EndY=21.6603 EndZ=0
    g6: Circle [constr] CenterX=-31 CenterY=21.6603 CenterZ=0 NormalX=0 NormalY=0 NormalZ=1 AngleXU=0 Radius=2
    g7: LineSegment StartX=-27 StartY=14.4641 StartZ=0 EndX=-26 EndY=16.1962 EndZ=0
    g8: LineSegment StartX=-26 StartY=16.1962 StartZ=0 EndX=-27 EndY=17.9282 EndZ=0
    g9: LineSegment StartX=-27 StartY=17.9282 StartZ=0 EndX=-29 EndY=17.9282 EndZ=0
    g10: LineSegment StartX=-29 StartY=17.9282 StartZ=0 EndX=-30 EndY=16.1962 EndZ=0
    g11: LineSegment StartX=-30 StartY=16.1962 StartZ=0 EndX=-29 EndY=14.4641 EndZ=0
    g12: LineSegment StartX=-29 StartY=14.4641 StartZ=0 EndX=-27 EndY=14.4641 EndZ=0
    g13: Circle [constr] CenterX=-28 CenterY=16.1962 CenterZ=0 NormalX=0 NormalY=0 NormalZ=1 AngleXU=0 Radius=2
    g14: LineSegment [constr] StartX=-29 StartY=10.7321 StartZ=0 EndX=-30 EndY=12.4641 EndZ=0
    g15: LineSegment [constr] StartX=-30 StartY=12.4641 StartZ=0 EndX=-32 EndY=12.4641 EndZ=0
    g16: LineSegment [constr] StartX=-32 StartY=12.4641 StartZ=0 EndX=-33 EndY=10.7321 EndZ=0
    g17: LineSegment [constr] StartX=-33 StartY=10.7321 StartZ=0 EndX=-32 EndY=9 EndZ=0
    g18: LineSegment [constr] StartX=-32 StartY=9 StartZ=0 EndX=-30 EndY=9 EndZ=0
    g19: LineSegment [constr] StartX=-30 StartY=9 StartZ=0 EndX=-29 EndY=10.7321 EndZ=0
    g20: Circle [constr] CenterX=-31 CenterY=10.7321 CenterZ=0 NormalX=0 NormalY=0 NormalZ=1 AngleXU=0 Radius=2
  constraints (51):
    c: Coincident(g0,g1)
    c: Coincident(g1,g2)
    c: Coincident(g2,g3)
    c: Coincident(g3,g4)
    c: Coincident(g4,g5)
    c: Coincident(g5,g0)
    c: Equal(g0, g1-g5) x5
    c: PointOnObject(g0,g6)
    c: PointOnObject(g1,g6)
    c: PointOnObject(g2,g6)
    c: PointOnObject(g3,g6)
    c: PointOnObject(g4,g6)
    c: PointOnObject(g5,g6)
    c: Radius(g6) = 2
    c: Perpendicular(g-2,g4)
    c: Coincident(g7,g8)
    c: Coincident(g8,g9)
    c: Coincident(g9,g10)
    c: Coincident(g10,g11)
    c: Coincident(g11,g12)
    c: Coincident(g12,g7)
    c: Equal(g7, g8-g12) x5
    c: PointOnObject(g7,g13)
    c: PointOnObject(g8,g13)
    c: PointOnObject(g9,g13)
    c: PointOnObject(g10,g13)
    c: PointOnObject(g11,g13)
    c: PointOnObject(g12,g13)
    c: Perpendicular(g-2,g12)
    c: Radius(g13) = 2
    c: DistanceY(g9,g4) = 2
    c: Coincident(g14,g15)
    c: Coincident(g15,g16)
    c: Coincident(g16,g17)
    c: Coincident(g17,g18)
    c: Coincident(g18,g19)
    c: Coincident(g19,g14)
    c: Equal(g14, g15-g19) x5
    c: PointOnObject(g14,g20)
    c: PointOnObject(g15,g20)
    c: PointOnObject(g16,g20)
    c: PointOnObject(g17,g20)
    c: PointOnObject(g18,g20)
    c: PointOnObject(g19,g20)
    c: Perpendicular(g-2,g18)
    c: Radius(g20) = 2
    c: DistanceY(g14,g11) = 2
    c: DistanceX(g18,g-1) = 30
    c: DistanceY(g-1,g17) = 9
    c: DistanceX(g10,g4) = 0
    c: DistanceX(g11,g14) = 0
FEATURE [PartDesign::Pocket] Pocket033  label="BottomVentHolePocket"
  BaseFeature = -> Fillet005
  Length = 2
  Length2 = 100
  Placement = pos=(0,0,0) rot=(1,0,0;1.5708rad)
  Profile = -> Sketch082
  Type = 0
FEATURE [PartDesign::LinearPattern] LinearPattern001
  BaseFeature = -> Pocket033
  Direction = -> Sketch082 [H_Axis]
  Length = 59
  Occurrences = 10
  Originals = -> [Pocket033]
  Placement = pos=(0,0,0) rot=(1,0,0;1.5708rad)
FEATURE [PartDesign::Body] Body012  label="Housing - v5"
  Group = -> [Sketch061,Pad034,Pocket025,Sketch062,Pocket024,Pocket021,Pocket023,Pad038,Pad035,Sketch065,Pad037,Sketch060,Sketch057,Sketch058,Sketch059,Sketch075,Pad045,DatumPlane,Sketch066,Pocket028,Pocket030,LinearPattern,Pad047,Sketch078,Sketch079,Chamfer011,Fillet004,Fillet005,Sketch082,Pocket033,LinearPattern001]
  Origin = -> Origin020
  Tip = -> LinearPattern001
FEATURE [Sketcher::SketchObject] PCB_Sketch001
  sketch-geometry (32):
    g0: LineSegment StartX=-65.5 StartY=30.6 StartZ=0 EndX=-70.5 EndY=30.6 EndZ=0
    g1: LineSegment StartX=-65.5 StartY=31.6 StartZ=0 EndX=-70.5 EndY=31.6 EndZ=0
    g2: LineSegment StartX=-62.6 StartY=33.5 StartZ=0 EndX=-62.6 EndY=42.5 EndZ=0
    g3: LineSegment StartX=-63.6 StartY=33.5 StartZ=0 EndX=-63.6 EndY=42.5 EndZ=0
    g4: LineSegment StartX=-41.5 StartY=-5.5 StartZ=0 EndX=-41.5 EndY=75.5 EndZ=0
    g5: LineSegment StartX=-125.5 StartY=-8.5 StartZ=0 EndX=-44.5 EndY=-8.5 EndZ=0
    g6: LineSegment StartX=-128.5 StartY=75.5 StartZ=0 EndX=-128.5 EndY=-5.5 EndZ=0
    g7: LineSegment StartX=-125.5 StartY=78.5 StartZ=0 EndX=-44.5 EndY=78.5 EndZ=0
    g8: ArcOfCircle CenterX=-114 CenterY=59.8 CenterZ=0 NormalX=0 NormalY=0 NormalZ=1 AngleXU=0 Radius=1 StartAngle=4.71239 EndAngle=7.85398
    g9: ArcOfCircle CenterX=-114 CenterY=59.8 CenterZ=0 NormalX=0 NormalY=0 NormalZ=1 AngleXU=0 Radius=1.4 StartAngle=4.71239 EndAngle=7.85398
    g10: ArcOfCircle CenterX=-114 CenterY=61 CenterZ=0 NormalX=0 NormalY=0 NormalZ=1 AngleXU=0 Radius=0.2 StartAngle=1.5708 EndAngle=4.71239
    g11: ArcOfCircle CenterX=-114 CenterY=58.6 CenterZ=0 NormalX=0 NormalY=0 NormalZ=1 AngleXU=0 Radius=0.2 StartAngle=1.5708 EndAngle=4.71239
    g12: ArcOfCircle CenterX=-114 CenterY=66.2 CenterZ=0 NormalX=0 NormalY=0 NormalZ=1 AngleXU=0 Radius=0.2 StartAngle=1.5708 EndAngle=4.71239
    g13: ArcOfCircle CenterX=-114 CenterY=68.6 CenterZ=0 NormalX=0 NormalY=0 NormalZ=1 AngleXU=0 Radius=0.2 StartAngle=1.5708 EndAngle=4.71239
    g14: ArcOfCircle CenterX=-114 CenterY=67.4 CenterZ=0 NormalX=0 NormalY=0 NormalZ=1 AngleXU=0 Radius=1.4 StartAngle=4.71239 EndAngle=7.85398
    g15: ArcOfCircle CenterX=-114 CenterY=67.4 CenterZ=0 NormalX=0 NormalY=0 NormalZ=1 AngleXU=0 Radius=1 StartAngle=4.71239 EndAngle=7.85398
    g16: ArcOfCircle CenterX=-125.4 CenterY=67.5 CenterZ=0 NormalX=0 NormalY=0 NormalZ=1 AngleXU=0 Radius=0.2 StartAngle=3.14159 EndAngle=6.28319
    g17: ArcOfCircle CenterX=-124.2 CenterY=67.5 CenterZ=0 NormalX=0 NormalY=0 NormalZ=1 AngleXU=0 Radius=1 StartAngle=0 EndAngle=3.14159
    g18: ArcOfCircle CenterX=-123 CenterY=67.5 CenterZ=0 NormalX=0 NormalY=0 NormalZ=1 AngleXU=0 Radius=0.2 StartAngle=3.14159 EndAngle=6.28319
    g19: ArcOfCircle CenterX=-124.2 CenterY=67.5 CenterZ=0 NormalX=0 NormalY=0 NormalZ=1 AngleXU=0 Radius=1.4 StartAngle=0 EndAngle=3.14159
    g20: ArcOfCircle CenterX=-123 CenterY=59.8 CenterZ=0 NormalX=0 NormalY=0 NormalZ=1 AngleXU=0 Radius=0.2 StartAngle=0 EndAngle=3.14159
    g21: ArcOfCircle CenterX=-125.4 CenterY=59.8 CenterZ=0 NormalX=0 NormalY=0 NormalZ=1 AngleXU=0 Radius=0.2 StartAngle=0 EndAngle=3.14159
    g22: ArcOfCircle CenterX=-124.2 CenterY=59.8 CenterZ=0 NormalX=0 NormalY=0 NormalZ=1 AngleXU=0 Radius=1.4 StartAngle=3.14159 EndAngle=6.28319
    g23: ArcOfCircle CenterX=-124.2 CenterY=59.8 CenterZ=0 NormalX=0 NormalY=0 NormalZ=1 AngleXU=0 Radius=1 StartAngle=3.14159 EndAngle=6.28319
    g24: ArcOfCircle CenterX=-63.1 CenterY=42.5 CenterZ=0 NormalX=0 NormalY=0 NormalZ=1 AngleXU=0 Radius=0.5 StartAngle=0 EndAngle=3.14159
    g25: ArcOfCircle CenterX=-70.5 CenterY=31.1 CenterZ=0 NormalX=0 NormalY=0 NormalZ=1 AngleXU=0 Radius=0.5 StartAngle=1.5708 EndAngle=4.71239
    g26: ArcOfCircle CenterX=-65.5 CenterY=33.5 CenterZ=0 NormalX=0 NormalY=0 NormalZ=1 AngleXU=0 Radius=2.9 StartAngle=4.71239 EndAngle=6.28319
    g27: ArcOfCircle CenterX=-65.5 CenterY=33.5 CenterZ=0 NormalX=0 NormalY=0 NormalZ=1 AngleXU=0 Radius=1.9 StartAngle=4.71239 EndAngle=6.28319
    g28: ArcOfCircle CenterX=-44.5 CenterY=-5.5 CenterZ=0 NormalX=0 NormalY=0 NormalZ=1 AngleXU=0 Radius=3 StartAngle=4.71239 EndAngle=6.28319
    g29: ArcOfCircle CenterX=-125.5 CenterY=-5.5 CenterZ=0 NormalX=0 NormalY=0 NormalZ=1 AngleXU=0 Radius=3 StartAngle=3.14159 EndAngle=4.71239
    g30: ArcOfCircle CenterX=-44.5 CenterY=75.5 CenterZ=0 NormalX=0 NormalY=0 NormalZ=1 AngleXU=0 Radius=3 StartAngle=0 EndAngle=1.5708
    g31: ArcOfCircle CenterX=-125.5 CenterY=75.5 CenterZ=0 NormalX=0 NormalY=0 NormalZ=1 AngleXU=0 Radius=3 StartAngle=1.5708 EndAngle=3.14159
  constraints (32):
    c: Coincident(g6,g29)
    c: Coincident(g31,g6)
    c: Coincident(g22,g21)
    c: Coincident(g16,g19)
    c: Coincident(g5,g29)
    c: Coincident(g7,g31)
    c: Coincident(g23,g21)
    c: Coincident(g17,g16)
    c: Coincident(g20,g23)
    c: Coincident(g18,g17)
    c: Coincident(g20,g22)
    c: Coincident(g18,g19)
    c: Coincident(g11,g9)
    c: Coincident(g8,g11)
    c: Coincident(g10,g8)
    c: Coincident(g10,g9)
    c: Coincident(g12,g14)
    c: Coincident(g15,g12)
    c: Coincident(g15,g13)
    c: Coincident(g14,g13)
    c: Coincident(g0,g25)
    c: Coincident(g1,g25)
    c: Coincident(g26,g0)
    c: Coincident(g1,g27)
    c: Coincident(g3,g27)
    c: Coincident(g3,g24)
    c: Coincident(g2,g26)
    c: Coincident(g2,g24)
    c: Coincident(g5,g28)
    c: Coincident(g7,g30)
    c: Coincident(g4,g28)
    c: Coincident(g4,g30)
FEATURE [Part::Feature] botTracks001
  Placement = pos=(-148.5,98.5,-1.61) rot=(0,0,1;0rad)
  shape: bbox 86.65 x 86.65 x 0.04 mm, 300 faces, 0 solids (baked)
FEATURE [Part::Feature] topTracks001
  Placement = pos=(-148.5,98.5,0.01) rot=(0,0,1;0rad)
  shape: bbox 86.65 x 86.65 x 0.04 mm, 370 faces, 0 solids (baked)
FEATURE [Part::Feature] Shape011  label="C8_C_0805_2012Metric_5DE69605"
  Placement = pos=(-118.9,28.8,0) rot=(0,0,-1;1.5708rad)
  shape: bbox 1.25 x 2 x 1.25 mm, 28 faces (baked)
FEATURE [Part::Feature] Shape013  label="J4_PinHeader_1x06_P254mm_Vertical_5DECC307"
  Placement = pos=(-89.25,17.5,0) rot=(0,0,1;0rad)
  shape: bbox 2.54 x 15.24 x 11.54 mm, 148 faces (baked)
FEATURE [Part::Feature] Shape014  label="J3_PinHeader_1x04_P254mm_Vertical_5E11E2F8"
  Placement = pos=(-76.1,71.5,0) rot=(0,0,-1;1.5708rad)
  shape: bbox 10.16 x 2.54 x 11.54 mm, 100 faces (baked)
FEATURE [Part::Feature] Shape017  label="R1_A2_OPT1_R_0805_2012Metric_5DDDD022"
  Placement = pos=(-94.05,10.1,0) rot=(0,0,1;1.5708rad)
  shape: bbox 1.2 x 2 x 0.45 mm, 26 faces (baked)
FEATURE [Part::Feature] Shape010  label="R_A1_OPT1_A2_OPT1_R_0805_2012Metric_5DE69680"
  Placement = pos=(-113.8,36.675,0) rot=(0,0,-1;1.5708rad)
  shape: bbox 1.2 x 2 x 0.45 mm, 26 faces (baked)
FEATURE [Part::Feature] Shape020  label="R12_A2_OPT1_R_0805_2012Metric_5DDDCEA5"
  Placement = pos=(-106.3,7.3,-1.6) rot=(0.707107,-0.707107,0;3.14159rad)
  shape: bbox 1.2 x 2 x 0.45 mm, 26 faces (baked)
FEATURE [Part::Feature] Shape008  label="C7_C_0805_2012Metric_5DE696E0"
  Placement = pos=(-110.95,32.7,0) rot=(0,0,1;1.5708rad)
  shape: bbox 1.25 x 2 x 1.25 mm, 28 faces (baked)
FEATURE [Part::Feature] Shape018  label="R14_A2_OPT1_R_0805_2012Metric_5DDDCF05"
  Placement = pos=(-108.3,7.3,-1.6) rot=(0.707107,-0.707107,0;3.14159rad)
  shape: bbox 1.2 x 2 x 0.45 mm, 26 faces (baked)
FEATURE [Part::Feature] Shape023  label="R9_A2_OPT1_R_0805_2012Metric_5DDDCE15"
  Placement = pos=(-104.3,13.2,-1.6) rot=(0.707107,-0.707107,0;3.14159rad)
  shape: bbox 1.2 x 2 x 0.45 mm, 26 faces (baked)
FEATURE [Part::Feature] Shape  label="L1_UU9.8-10MH_5DDDFA6B"
  Placement = pos=(-69.2,59.7,0) rot=(0,0,-1;1.5708rad)
  shape: bbox 16.5 x 12 x 22 mm, 14 faces (baked)
FEATURE [Part::Feature] Shape004  label="J5_PinHeader_1x03_P254mm_Vertical_5E0765B4"
  Placement = pos=(-85.58,-1,0) rot=(0,0,1;1.5708rad)
  shape: bbox 7.62 x 2.54 x 11.54 mm, 76 faces (baked)
FEATURE [Part::Feature] Shape005  label="K1_HK4100F-DC5V-SHG_5DE08D29"
  Placement = pos=(-111.5,59.8,0) rot=(0,0,1;3.14159rad)
  shape: bbox 15.37 x 10.5 x 17.1 mm, 18 faces (baked)
FEATURE [Part::Feature] Shape009  label="R_A2_OPT1_R_0805_2012Metric_5DE696B0"
  Placement = pos=(-115.95,36.675,0) rot=(0,0,-1;1.5708rad)
  shape: bbox 1.2 x 2 x 0.45 mm, 26 faces (baked)
FEATURE [Part::Feature] Shape006  label="C1_R46KI310040M1K_5DE04E80"
  Placement = pos=(-45.3,52.4,0) rot=(0,0,1;3.14159rad)
  shape: bbox 18 x 5 x 16.1 mm, 10 faces (baked)
FEATURE [Part::Feature] Shape003  label="C9_CP_Radial_D100mm_P500mm_5E1192C5"
  Placement = pos=(-104,42.1,0) rot=(0,0,-1;1.5708rad)
  shape: bbox 12.78 x 12.36 x 12 mm, 48 faces (baked)
FEATURE [Part::Feature] Shape012  label="C6_C_0805_2012Metric_5DE69764"
  Placement = pos=(-110.95,28.425,0) rot=(0,0,1;1.5708rad)
  shape: bbox 1.25 x 2 x 1.25 mm, 28 faces (baked)
FEATURE [Part::Feature] Shape019  label="R13_A2_OPT1_R_0805_2012Metric_5DDDCED5"
  Placement = pos=(-104.3,7.3,-1.6) rot=(0.707107,-0.707107,0;3.14159rad)
  shape: bbox 1.2 x 2 x 0.45 mm, 26 faces (baked)
FEATURE [Part::Feature] Shape021  label="R11_A2_OPT1_R_0805_2012Metric_5DED0468"
  Placement = pos=(-112.3,13.2,-1.6) rot=(0.707107,0.707107,0;3.14159rad)
  shape: bbox 1.2 x 2 x 0.45 mm, 26 faces (baked)
FEATURE [Part::Feature] Shape022  label="R10_A2_OPT1_R_0805_2012Metric_5DDDCE45"
  Placement = pos=(-110.3,13.2,-1.6) rot=(0.707107,0.707107,0;3.14159rad)
  shape: bbox 1.2 x 2 x 0.45 mm, 26 faces (baked)
FEATURE [Part::Feature] _443_500DR  label="F1_0443.500DR_5DE6AED5"
  Placement = pos=(-45.7,62.41,0) rot=(0,0,1;1.5708rad)
  shape: bbox 3.43 x 10.08 x 3.05 mm, 30 faces, 5 solids (baked)
FEATURE [Part::Feature] Shape001  label="C11_C_0805_2012Metric_5E11E5EA"
  Placement = pos=(-89,-1.025,0) rot=(0,0,1;1.5708rad)
  shape: bbox 1.25 x 2 x 1.25 mm, 28 faces (baked)
FEATURE [Part::Feature] Shape002  label="C10_C_0805_2012Metric_5E11C59E"
  Placement = pos=(-77.1,74.5,0) rot=(0,0,1;3.14159rad)
  shape: bbox 2 x 1.25 x 1.25 mm, 28 faces (baked)
FEATURE [Part::Feature] Shape015  label="C5_C_0805_2012Metric_5DDDD052"
  Placement = pos=(-116.25,-2.1,0) rot=(0,0,-1;1.5708rad)
  shape: bbox 1.25 x 2 x 1.25 mm, 28 faces (baked)
FEATURE [Part::Feature] Shape016  label="R15_A2_OPT1_R_0805_2012Metric_5DDDCF35"
  Placement = pos=(-110.3,7.3,-1.6) rot=(0.707107,-0.707107,0;3.14159rad)
  shape: bbox 1.2 x 2 x 0.45 mm, 26 faces (baked)
FEATURE [Part::Feature] Shape024  label="R8_A2_OPT1_R_0805_2012Metric_5DDDCDE5"
  Placement = pos=(-114.3,7.3,-1.6) rot=(0.707107,0.707107,0;3.14159rad)
  shape: bbox 1.2 x 2 x 0.45 mm, 26 faces (baked)
FEATURE [Part::Feature] Shape025  label="R7_A2_OPT1_R_0805_2012Metric_5DDDCDB5"
  Placement = pos=(-106.3,13.2,-1.6) rot=(0.707107,0.707107,0;3.14159rad)
  shape: bbox 1.2 x 2 x 0.45 mm, 26 faces (baked)
FEATURE [Part::Feature] Pcb001
  Placement = pos=(-148.5,98.5,0) rot=(0,0,1;0rad)
  shape: bbox 87 x 87 x 1.6 mm, 81 faces (baked)
FEATURE [Part::Feature] Shape007  label="U3_SOIC_8_39x49mm_P127mm_5DE6963E"
  Placement = pos=(-114.85,30.675,0) rot=(0,0,-1;1.5708rad)
  shape: bbox 4.9 x 6 x 1.75 mm, 156 faces (baked)
FEATURE [Part::Feature] Shape029  label="R3_A2_OPT1_R_0805_2012Metric_5DDDCCAD"
  Placement = pos=(-113.5,53.2,0) rot=(0,0,1;1.5708rad)
  shape: bbox 1.2 x 2 x 0.45 mm, 26 faces (baked)
FEATURE [Part::Feature] Shape028  label="R4_A2_OPT1_R_0805_2012Metric_5DDDCCDD"
  Placement = pos=(-114.246,-2.1,0) rot=(0,0,1;1.5708rad)
  shape: bbox 1.2 x 2 x 0.45 mm, 26 faces (baked)
FEATURE [Part::Feature] Shape031  label="C4_C_0805_2012Metric_5E078AB3"
  Placement = pos=(-102.25,-3.4,0) rot=(0,0,-1;1.5708rad)
  shape: bbox 1.25 x 2 x 1.25 mm, 28 faces (baked)
FEATURE [Part::Feature] Shape032  label="C3_C_0805_2012Metric_5E078A4F"
  Placement = pos=(-104.25,-3.4,0) rot=(0,0,-1;1.5708rad)
  shape: bbox 1.25 x 2 x 1.25 mm, 28 faces (baked)
FEATURE [Part::Feature] Shape033  label="U2_SOIC_8_39x49mm_P127mm_5DE697C4"
  Placement = pos=(-123,30.65,0) rot=(0,0,-1;1.5708rad)
  shape: bbox 4.9 x 6 x 1.75 mm, 156 faces (baked)
FEATURE [Part::Feature] Shape038  label="Q1_SS8050-G_5DDDC766"
  Placement = pos=(-95.05,5.7,0) rot=(0,0,-1;1.5708rad)
  shape: bbox 2.9 x 2.4 x 1.15 mm, 63 faces (baked)
FEATURE [Part::Feature] Shape039  label="D1_BAV170HMFHT116_5DDDC8D7"
  Placement = pos=(-123,53.2,0) rot=(0,0,1;3.14159rad)
  shape: bbox 2.4 x 2.9 x 1.15 mm, 63 faces (baked)
FEATURE [Part::Feature] Shape027  label="R5_A2_OPT1_R_0805_2012Metric_5DDDCD0D"
  Placement = pos=(-112.3,7.3,-1.6) rot=(0.707107,-0.707107,0;3.14159rad)
  shape: bbox 1.2 x 2 x 0.45 mm, 26 faces (baked)
FEATURE [Part::Feature] Shape030  label="R2_A2_OPT1_R_0805_2012Metric_5DDDCC7D"
  Placement = pos=(-96.05,10.1,0) rot=(0,0,-1;1.5708rad)
  shape: bbox 1.2 x 2 x 0.45 mm, 26 faces (baked)
FEATURE [Part::Feature] mkds_1_5_2  label="J1_mkds_1,5-2_5DDDC8A4"
  Placement = pos=(-58.1,71.7,0) rot=(0,0,-1;1.5708rad)
  shape: bbox 6.43 x 3.937 x 3.86 mm, 1658 faces, 0 solids (baked)
FEATURE [Part::Feature] Shape026  label="R6_A2_OPT1_R_0805_2012Metric_5DDDCD3D"
  Placement = pos=(-108.3,13.2,-1.6) rot=(0.707107,0.707107,0;3.14159rad)
  shape: bbox 1.2 x 2 x 0.45 mm, 26 faces (baked)
FEATURE [App::Part] Bot001
  Group = -> [Shape016,Shape018,Shape019,Shape020,Shape021,Shape022,Shape023,Shape024,Shape025,Shape026,Shape027]
  Origin = -> Origin024
FEATURE [Part::Feature] Shape036  label="Q3_AO3480_5DDDC982"
  Placement = pos=(-117.7,53.2,0) rot=(0,0,1;3.14159rad)
  shape: bbox 2.8 x 2.95 x 1.25 mm, 63 faces (baked)
FEATURE [Part::Feature] Shape037  label="Q2_SS8050-G_5DDDC7F3"
  Placement = pos=(-95.05,14.5,0) rot=(0,0,1;1.5708rad)
  shape: bbox 2.9 x 2.4 x 1.15 mm, 63 faces (baked)
FEATURE [Part::Feature] Shape035  label="C2_CP_Radial_D100mm_P500mm_5DDDCA77"
  Placement = pos=(-104,48.4,0) rot=(0,0,1;1.5708rad)
  shape: bbox 12.78 x 12.36 x 12 mm, 48 faces (baked)
FEATURE [Part::Feature] Shape034  label="RV1_RV_Disc_D12mm_W67mm_P75mm_5DE68EBF"
  Placement = pos=(-52.7,59.8,0) rot=(0,0,1;3.14159rad)
  shape: bbox 12 x 6.7 x 15.03 mm, 11 faces (baked)
FEATURE [App::Part] Top001
  Group = -> [Shape,Shape001,Shape002,Shape003,Shape004,Shape005,Shape006,Shape007,Shape008,Shape009,Shape010,Shape011,Shape012,Shape013,Shape014,_443_500DR,Shape015,Shape017,Shape028,Shape029,Shape030,Shape031,Shape032,Shape033,Shape034,Shape035,mkds_1_5_2,Shape036,Shape037,Shape038,Shape039]
  Origin = -> Origin023
FEATURE [App::Part] Step_Models001
  Group = -> [Top001,Bot001]
  Origin = -> Origin026
FEATURE [PartDesign::CoordinateSystem] Local_CS001
  AttacherType = Attacher::AttachEngine3D
FEATURE [App::Part] Board_Geoms001
  Group = -> [Local_CS001,Pcb001,PCB_Sketch001,topTracks001,botTracks001]
  Origin = -> Origin022
FEATURE [App::Part] Board001  label="esp-thermostat"
  Group = -> [Board_Geoms001,Step_Models001]
  Origin = -> Origin025
  Placement = pos=(-85,-18,-35) rot=(0,0.707107,0.707107;3.14159rad)
FEATURE [Mesh::Feature] Mesh010  label="Backplate - v5 (Meshed)"
FEATURE [Mesh::Feature] Mesh  label="Housing - v5 (Meshed)"
FEATURE [Mesh::Feature] Mesh011  label="Plus button (Meshed)"
FEATURE [Mesh::Feature] Mesh012  label="Minus button (Meshed)"
FEATURE [Mesh::Feature] Mesh013  label="Left button (Meshed)"
FEATURE [Mesh::Feature] Mesh014  label="Right button (Meshed)"
FEATURE [Mesh::Feature] Mesh015  label="Menu button (Meshed)"
FEATURE [Mesh::Feature] Mesh016  label="Boost button (Meshed)"
FEATURE [PartDesign::Body] Body011  label="Backplate"
  Group = -> [Sketch045,Pad027,Sketch046,Pad028,Sketch047,Pad029,Sketch048,Pocket017,Sketch049,Pad030,Fillet002,Pad031,Sketch050,Pocket018,Sketch051]
  Origin = -> Origin019
  Tip = -> Pocket018
FEATURE [PartDesign::Pocket] Pocket018
  BaseFeature = -> Pad031
  Length = 3
  Length2 = 100
  Placement = pos=(0,0,0) rot=(1,0,0;1.5708rad)
  Profile = -> Sketch050
  Type = 0
FEATURE [Sketcher::SketchObject] Sketch051
  ExternalGeometry = -> [Pocket018]
  MapMode = 5
  Placement = pos=(0,-4.66e-14,-55.95) rot=(0,0,1;3.14159rad)
  Support = -> [Pocket018]
  sketch-geometry (1):
    g0: Circle CenterX=0 CenterY=5.5 CenterZ=0 NormalX=0 NormalY=0 NormalZ=1 AngleXU=0 Radius=2
  constraints (2):
    c: Coincident(g0,g-3)
    c: Radius(g0) = 2
FEATURE [PartDesign::Pad] Pad031
  BaseFeature = -> Fillet002
  Length = 1
  Length2 = 100
  Placement = pos=(0,0,0) rot=(1,0,0;1.5708rad)
  Profile = -> Sketch051
  Type = 0
note: 6 file-system paths scrubbed to <path> (originals preserved in the JSON sidecar)
